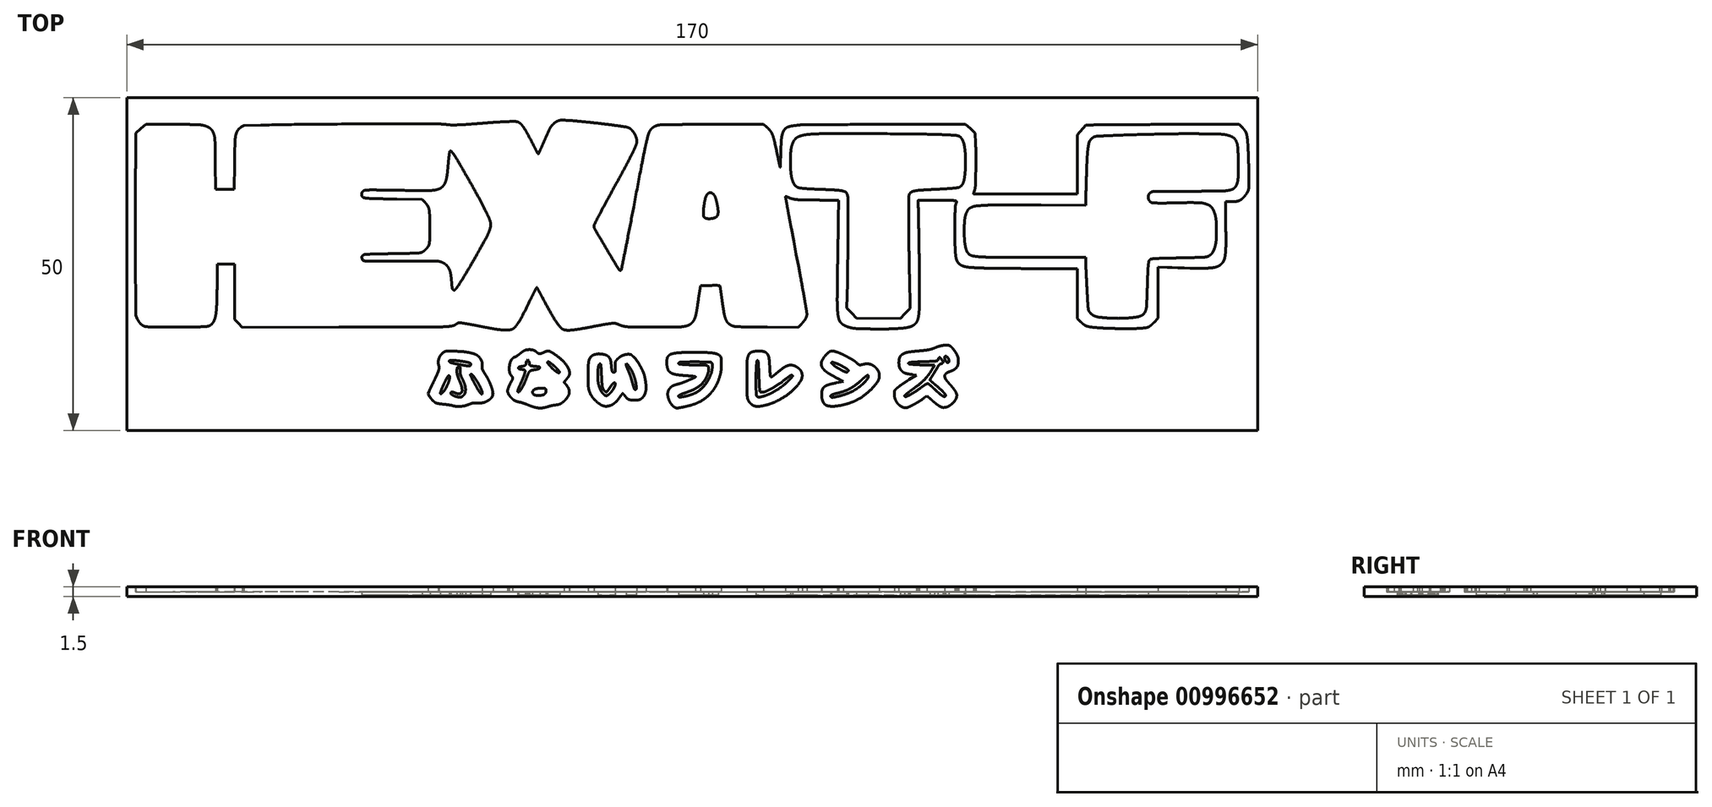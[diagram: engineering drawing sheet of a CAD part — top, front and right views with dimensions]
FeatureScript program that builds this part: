
annotation { "Feature Type Name" : "Feature", "Feature Type Description" : "" }
export const myFeature = defineFeature(function(context is Context, id is Id, definition is map)
    precondition{}
    {
        {
            var Q0;
            Q0=qCreatedBy(makeId("Top.planeOp"),FACE);
            var sketch = newSketch(context, id + "F0", { "sketchPlane" : qUnion([Q0])});
            skArc(sketch, "E0", {"start": v(-16.39, 21.41) * mm, "mid": v(-15.05, 21.27) * mm, "end": v(-13.72, 21.12) * mm});
            skArc(sketch, "E1", {"start": v(-13.72, 21.12) * mm, "mid": v(-12.67, 21) * mm, "end": v(-11.61, 20.86) * mm});
            skArc(sketch, "E2", {"start": v(-11.61, 20.86) * mm, "mid": v(-10.8, 20.74) * mm, "end": v(-9.97, 20.62) * mm});
            skArc(sketch, "E3", {"start": v(-9.97, 20.62) * mm, "mid": v(-9.73, 20.56) * mm, "end": v(-9.5, 20.47) * mm});
            skArc(sketch, "E4", {"start": v(-9.5, 20.47) * mm, "mid": v(-9.28, 20.34) * mm, "end": v(-9.1, 20.17) * mm});
            skArc(sketch, "E5", {"start": v(-9.1, 20.17) * mm, "mid": v(-8.9, 19.95) * mm, "end": v(-8.73, 19.7) * mm});
            skArc(sketch, "E6", {"start": v(-8.73, 19.7) * mm, "mid": v(-8.58, 19.45) * mm, "end": v(-8.45, 19.17) * mm});
            skArc(sketch, "E7", {"start": v(-8.45, 19.17) * mm, "mid": v(-8.37, 18.9) * mm, "end": v(-8.33, 18.63) * mm});
            skArc(sketch, "E8", {"start": v(-8.33, 18.63) * mm, "mid": v(-8.32, 18.52) * mm, "end": v(-8.32, 18.42) * mm});
            skArc(sketch, "E9", {"start": v(-8.32, 18.42) * mm, "mid": v(-8.32, 18.33) * mm, "end": v(-8.33, 18.24) * mm});
            skArc(sketch, "E10", {"start": v(-8.33, 18.24) * mm, "mid": v(-8.36, 18.14) * mm, "end": v(-8.38, 18.04) * mm});
            skArc(sketch, "E11", {"start": v(-8.38, 18.04) * mm, "mid": v(-8.43, 17.9) * mm, "end": v(-8.48, 17.77) * mm});
            skArc(sketch, "E12", {"start": v(-8.48, 17.77) * mm, "mid": v(-8.64, 17.4) * mm, "end": v(-8.8, 17.04) * mm});
            skArc(sketch, "E13", {"start": v(-8.8, 17.04) * mm, "mid": v(-9.11, 16.42) * mm, "end": v(-9.43, 15.8) * mm});
            skArc(sketch, "E14", {"start": v(-9.43, 15.8) * mm, "mid": v(-9.8, 15.06) * mm, "end": v(-10.2, 14.33) * mm});
            skArc(sketch, "E15", {"start": v(-10.2, 14.33) * mm, "mid": v(-10.61, 13.55) * mm, "end": v(-11.04, 12.77) * mm});
            skArc(sketch, "E16", {"start": v(-11.04, 12.77) * mm, "mid": v(-11.9, 11.22) * mm, "end": v(-12.74, 9.67) * mm});
            skArc(sketch, "E17", {"start": v(-12.74, 9.67) * mm, "mid": v(-13.3, 8.62) * mm, "end": v(-13.86, 7.57) * mm});
            skArc(sketch, "E18", {"start": v(-13.86, 7.57) * mm, "mid": v(-14.27, 6.8) * mm, "end": v(-14.67, 6.02) * mm});
            skArc(sketch, "E19", {"start": v(-14.67, 6.02) * mm, "mid": v(-14.73, 5.88) * mm, "end": v(-14.74, 5.72) * mm});
            skArc(sketch, "E20", {"start": v(-14.74, 5.72) * mm, "mid": v(-14.7, 5.46) * mm, "end": v(-14.6, 5.22) * mm});
            skArc(sketch, "E21", {"start": v(-14.6, 5.22) * mm, "mid": v(-13.73, 3.73) * mm, "end": v(-12.84, 2.24) * mm});
            skArc(sketch, "E22", {"start": v(-12.84, 2.24) * mm, "mid": v(-11.93, 0.71) * mm, "end": v(-11.02, -0.8) * mm});
            skArc(sketch, "E23", {"start": v(-11.02, -0.8) * mm, "mid": v(-10.9, -0.91) * mm, "end": v(-10.76, -0.95) * mm});
            skArc(sketch, "E24", {"start": v(-10.76, -0.95) * mm, "mid": v(-10.7, -0.93) * mm, "end": v(-10.66, -0.87) * mm});
            skArc(sketch, "E25", {"start": v(-10.66, -0.87) * mm, "mid": v(-10.44, 0.14) * mm, "end": v(-10.24, 1.15) * mm});
            skArc(sketch, "E26", {"start": v(-10.24, 1.15) * mm, "mid": v(-9.95, 2.55) * mm, "end": v(-9.68, 3.94) * mm});
            skArc(sketch, "E27", {"start": v(-9.68, 3.94) * mm, "mid": v(-9.23, 6.26) * mm, "end": v(-8.8, 8.58) * mm});
            skArc(sketch, "E28", {"start": v(-8.8, 8.58) * mm, "mid": v(-8.22, 11.62) * mm, "end": v(-7.63, 14.66) * mm});
            skArc(sketch, "E29", {"start": v(-7.63, 14.66) * mm, "mid": v(-7.35, 16.1) * mm, "end": v(-7.05, 17.54) * mm});
            skArc(sketch, "E30", {"start": v(-7.05, 17.54) * mm, "mid": v(-6.87, 18.38) * mm, "end": v(-6.66, 19.23) * mm});
            skArc(sketch, "E31", {"start": v(-6.66, 19.23) * mm, "mid": v(-6.54, 19.62) * mm, "end": v(-6.37, 20) * mm});
            skArc(sketch, "E32", {"start": v(-6.37, 20) * mm, "mid": v(-6.26, 20.16) * mm, "end": v(-6.14, 20.31) * mm});
            skArc(sketch, "E33", {"start": v(-6.14, 20.31) * mm, "mid": v(-6, 20.45) * mm, "end": v(-5.85, 20.57) * mm});
            skArc(sketch, "E34", {"start": v(-5.85, 20.57) * mm, "mid": v(-5.67, 20.68) * mm, "end": v(-5.49, 20.77) * mm});
            skArc(sketch, "E35", {"start": v(-5.49, 20.77) * mm, "mid": v(-5.28, 20.84) * mm, "end": v(-5.07, 20.9) * mm});
            skArc(sketch, "E36", {"start": v(-5.07, 20.9) * mm, "mid": v(-4.86, 20.93) * mm, "end": v(-4.64, 20.94) * mm});
            skArc(sketch, "E37", {"start": v(-4.64, 20.94) * mm, "mid": v(-3.87, 20.96) * mm, "end": v(-3.1, 20.97) * mm});
            skArc(sketch, "E38", {"start": v(-3.1, 20.97) * mm, "mid": v(-1.96, 20.98) * mm, "end": v(-0.81, 21) * mm});
            skArc(sketch, "E39", {"start": v(-0.81, 21) * mm, "mid": v(1.12, 21) * mm, "end": v(3.05, 21.01) * mm});
            skLineSegment(sketch, "E40", {"start": v(3.05, 21.01) * mm, "end": v(10.73, 21.04) * mm});
            skLineSegment(sketch, "E41", {"start": v(10.73, 21.04) * mm, "end": v(11.19, 20.64) * mm});
            skArc(sketch, "E42", {"start": v(11.19, 20.64) * mm, "mid": v(11.47, 20.36) * mm, "end": v(11.73, 20.06) * mm});
            skArc(sketch, "E43", {"start": v(11.73, 20.06) * mm, "mid": v(11.92, 19.77) * mm, "end": v(12.07, 19.45) * mm});
            skArc(sketch, "E44", {"start": v(12.07, 19.45) * mm, "mid": v(12.23, 19) * mm, "end": v(12.36, 18.52) * mm});
            skArc(sketch, "E45", {"start": v(12.36, 18.52) * mm, "mid": v(12.58, 17.5) * mm, "end": v(12.8, 16.48) * mm});
            skArc(sketch, "E46", {"start": v(12.8, 16.48) * mm, "mid": v(12.89, 16.08) * mm, "end": v(12.97, 15.67) * mm});
            skArc(sketch, "E47", {"start": v(12.97, 15.67) * mm, "mid": v(13.04, 15.35) * mm, "end": v(13.12, 15.03) * mm});
            skArc(sketch, "E48", {"start": v(13.12, 15.03) * mm, "mid": v(13.17, 14.8) * mm, "end": v(13.23, 14.55) * mm});
            skArc(sketch, "E49", {"start": v(13.23, 14.55) * mm, "mid": v(13.24, 14.54) * mm, "end": v(13.25, 14.55) * mm});
            skArc(sketch, "E50", {"start": v(13.25, 14.55) * mm, "mid": v(13.26, 14.63) * mm, "end": v(13.26, 14.7) * mm});
            skArc(sketch, "E51", {"start": v(13.26, 14.7) * mm, "mid": v(13.27, 15) * mm, "end": v(13.28, 15.29) * mm});
            skArc(sketch, "E52", {"start": v(13.28, 15.29) * mm, "mid": v(13.29, 15.63) * mm, "end": v(13.3, 15.98) * mm});
            skArc(sketch, "E53", {"start": v(13.3, 15.98) * mm, "mid": v(13.31, 16.37) * mm, "end": v(13.32, 16.76) * mm});
            skArc(sketch, "E54", {"start": v(13.32, 16.76) * mm, "mid": v(13.35, 17.49) * mm, "end": v(13.38, 18.21) * mm});
            skArc(sketch, "E55", {"start": v(13.38, 18.21) * mm, "mid": v(13.4, 18.6) * mm, "end": v(13.45, 19) * mm});
            skArc(sketch, "E56", {"start": v(13.45, 19) * mm, "mid": v(13.5, 19.26) * mm, "end": v(13.55, 19.52) * mm});
            skArc(sketch, "E57", {"start": v(13.55, 19.52) * mm, "mid": v(13.63, 19.75) * mm, "end": v(13.73, 19.98) * mm});
            skArc(sketch, "E58", {"start": v(13.73, 19.98) * mm, "mid": v(13.85, 20.18) * mm, "end": v(14, 20.35) * mm});
            skArc(sketch, "E59", {"start": v(14, 20.35) * mm, "mid": v(14.17, 20.5) * mm, "end": v(14.36, 20.6) * mm});
            skArc(sketch, "E60", {"start": v(14.36, 20.6) * mm, "mid": v(14.64, 20.7) * mm, "end": v(14.94, 20.76) * mm});
            skArc(sketch, "E61", {"start": v(14.94, 20.76) * mm, "mid": v(15.46, 20.83) * mm, "end": v(15.99, 20.9) * mm});
            skArc(sketch, "E62", {"start": v(15.99, 20.9) * mm, "mid": v(16.28, 20.93) * mm, "end": v(16.58, 20.94) * mm});
            skArc(sketch, "E63", {"start": v(16.58, 20.94) * mm, "mid": v(18.06, 20.95) * mm, "end": v(19.55, 20.96) * mm});
            skArc(sketch, "E64", {"start": v(19.55, 20.96) * mm, "mid": v(21.5, 20.98) * mm, "end": v(23.44, 20.99) * mm});
            skArc(sketch, "E65", {"start": v(23.44, 20.99) * mm, "mid": v(26.15, 21) * mm, "end": v(28.87, 21) * mm});
            skLineSegment(sketch, "E66", {"start": v(28.87, 21) * mm, "end": v(41.08, 21.04) * mm});
            skLineSegment(sketch, "E67", {"start": v(41.08, 21.04) * mm, "end": v(41.82, 20.37) * mm});
            skLineSegment(sketch, "E68", {"start": v(41.82, 20.37) * mm, "end": v(42.57, 19.7) * mm});
            skLineSegment(sketch, "E69", {"start": v(42.57, 19.7) * mm, "end": v(42.62, 18.14) * mm});
            skArc(sketch, "E70", {"start": v(42.62, 18.14) * mm, "mid": v(42.63, 17.76) * mm, "end": v(42.64, 17.37) * mm});
            skArc(sketch, "E71", {"start": v(42.64, 17.37) * mm, "mid": v(42.64, 16.84) * mm, "end": v(42.65, 16.3) * mm});
            skArc(sketch, "E72", {"start": v(42.65, 16.3) * mm, "mid": v(42.65, 15.72) * mm, "end": v(42.65, 15.14) * mm});
            skArc(sketch, "E73", {"start": v(42.65, 15.14) * mm, "mid": v(42.64, 14.6) * mm, "end": v(42.64, 14.06) * mm});
            skArc(sketch, "E74", {"start": v(42.64, 14.06) * mm, "mid": v(42.63, 13.3) * mm, "end": v(42.62, 12.54) * mm});
            skArc(sketch, "E75", {"start": v(42.62, 12.54) * mm, "mid": v(42.6, 12.2) * mm, "end": v(42.59, 11.86) * mm});
            skArc(sketch, "E76", {"start": v(42.59, 11.86) * mm, "mid": v(42.57, 11.65) * mm, "end": v(42.54, 11.44) * mm});
            skArc(sketch, "E77", {"start": v(42.54, 11.44) * mm, "mid": v(42.5, 11.26) * mm, "end": v(42.46, 11.09) * mm});
            skArc(sketch, "E78", {"start": v(42.46, 11.09) * mm, "mid": v(42.43, 11) * mm, "end": v(42.4, 10.91) * mm});
            skArc(sketch, "E79", {"start": v(42.4, 10.91) * mm, "mid": v(42.37, 10.83) * mm, "end": v(42.35, 10.75) * mm});
            skArc(sketch, "E80", {"start": v(42.35, 10.75) * mm, "mid": v(42.33, 10.69) * mm, "end": v(42.31, 10.62) * mm});
            skArc(sketch, "E81", {"start": v(42.31, 10.62) * mm, "mid": v(42.3, 10.6) * mm, "end": v(42.3, 10.58) * mm});
            skArc(sketch, "E82", {"start": v(42.3, 10.58) * mm, "mid": v(42.31, 10.57) * mm, "end": v(42.33, 10.56) * mm});
            skArc(sketch, "E83", {"start": v(42.33, 10.56) * mm, "mid": v(43.46, 10.55) * mm, "end": v(44.6, 10.54) * mm});
            skArc(sketch, "E84", {"start": v(44.6, 10.54) * mm, "mid": v(45.86, 10.54) * mm, "end": v(47.12, 10.53) * mm});
            skArc(sketch, "E85", {"start": v(47.12, 10.53) * mm, "mid": v(48.61, 10.53) * mm, "end": v(50.11, 10.53) * mm});
            skLineSegment(sketch, "E86", {"start": v(50.11, 10.53) * mm, "end": v(57.92, 10.53) * mm});
            skLineSegment(sketch, "E87", {"start": v(57.92, 10.53) * mm, "end": v(57.92, 14.98) * mm});
            skLineSegment(sketch, "E88", {"start": v(57.92, 14.98) * mm, "end": v(57.92, 19.43) * mm});
            skLineSegment(sketch, "E89", {"start": v(57.92, 19.43) * mm, "end": v(58.56, 20.15) * mm});
            skLineSegment(sketch, "E90", {"start": v(58.56, 20.15) * mm, "end": v(59.2, 20.88) * mm});
            skLineSegment(sketch, "E91", {"start": v(59.2, 20.88) * mm, "end": v(60.08, 20.92) * mm});
            skArc(sketch, "E92", {"start": v(60.08, 20.92) * mm, "mid": v(60.4, 20.93) * mm, "end": v(60.73, 20.93) * mm});
            skArc(sketch, "E93", {"start": v(60.73, 20.93) * mm, "mid": v(62.28, 20.95) * mm, "end": v(63.83, 20.96) * mm});
            skArc(sketch, "E94", {"start": v(63.83, 20.96) * mm, "mid": v(65.65, 20.97) * mm, "end": v(67.46, 20.98) * mm});
            skArc(sketch, "E95", {"start": v(67.46, 20.98) * mm, "mid": v(69.53, 21) * mm, "end": v(71.6, 21) * mm});
            skLineSegment(sketch, "E96", {"start": v(71.6, 21) * mm, "end": v(82.25, 21.05) * mm});
            skLineSegment(sketch, "E97", {"start": v(82.25, 21.05) * mm, "end": v(82.7, 20.57) * mm});
            skArc(sketch, "E98", {"start": v(82.7, 20.57) * mm, "mid": v(82.87, 20.36) * mm, "end": v(83.04, 20.15) * mm});
            skArc(sketch, "E99", {"start": v(83.04, 20.15) * mm, "mid": v(83.15, 19.98) * mm, "end": v(83.25, 19.8) * mm});
            skArc(sketch, "E100", {"start": v(83.25, 19.8) * mm, "mid": v(83.32, 19.62) * mm, "end": v(83.37, 19.42) * mm});
            skArc(sketch, "E101", {"start": v(83.37, 19.42) * mm, "mid": v(83.42, 19.16) * mm, "end": v(83.46, 18.9) * mm});
            skArc(sketch, "E102", {"start": v(83.46, 18.9) * mm, "mid": v(83.5, 18.42) * mm, "end": v(83.54, 17.94) * mm});
            skArc(sketch, "E103", {"start": v(83.54, 17.94) * mm, "mid": v(83.58, 17.18) * mm, "end": v(83.61, 16.43) * mm});
            skArc(sketch, "E104", {"start": v(83.61, 16.43) * mm, "mid": v(83.64, 15.59) * mm, "end": v(83.67, 14.75) * mm});
            skArc(sketch, "E105", {"start": v(83.67, 14.75) * mm, "mid": v(83.68, 13.95) * mm, "end": v(83.69, 13.14) * mm});
            skArc(sketch, "E106", {"start": v(83.69, 13.14) * mm, "mid": v(83.69, 12.54) * mm, "end": v(83.69, 11.93) * mm});
            skArc(sketch, "E107", {"start": v(83.69, 11.93) * mm, "mid": v(83.68, 11.7) * mm, "end": v(83.67, 11.46) * mm});
            skArc(sketch, "E108", {"start": v(83.67, 11.46) * mm, "mid": v(83.65, 11.32) * mm, "end": v(83.63, 11.18) * mm});
            skArc(sketch, "E109", {"start": v(83.63, 11.18) * mm, "mid": v(83.59, 11.05) * mm, "end": v(83.53, 10.93) * mm});
            skArc(sketch, "E110", {"start": v(83.53, 10.93) * mm, "mid": v(83.42, 10.72) * mm, "end": v(83.3, 10.52) * mm});
            skArc(sketch, "E111", {"start": v(83.3, 10.52) * mm, "mid": v(83.14, 10.32) * mm, "end": v(82.98, 10.13) * mm});
            skArc(sketch, "E112", {"start": v(82.98, 10.13) * mm, "mid": v(82.82, 9.96) * mm, "end": v(82.65, 9.8) * mm});
            skArc(sketch, "E113", {"start": v(82.65, 9.8) * mm, "mid": v(82.5, 9.69) * mm, "end": v(82.33, 9.6) * mm});
            skArc(sketch, "E114", {"start": v(82.33, 9.6) * mm, "mid": v(82.22, 9.54) * mm, "end": v(82.1, 9.49) * mm});
            skArc(sketch, "E115", {"start": v(82.1, 9.49) * mm, "mid": v(82, 9.46) * mm, "end": v(81.89, 9.44) * mm});
            skArc(sketch, "E116", {"start": v(81.89, 9.44) * mm, "mid": v(81.75, 9.42) * mm, "end": v(81.6, 9.41) * mm});
            skArc(sketch, "E117", {"start": v(81.6, 9.41) * mm, "mid": v(81.34, 9.41) * mm, "end": v(81.07, 9.4) * mm});
            skLineSegment(sketch, "E118", {"start": v(81.07, 9.4) * mm, "end": v(80.17, 9.4) * mm});
            skLineSegment(sketch, "E119", {"start": v(80.17, 9.4) * mm, "end": v(80.22, 5.86) * mm});
            skArc(sketch, "E120", {"start": v(80.22, 5.86) * mm, "mid": v(80.23, 4.63) * mm, "end": v(80.24, 3.4) * mm});
            skArc(sketch, "E121", {"start": v(80.24, 3.4) * mm, "mid": v(80.23, 2.75) * mm, "end": v(80.2, 2.1) * mm});
            skArc(sketch, "E122", {"start": v(80.2, 2.1) * mm, "mid": v(80.18, 1.68) * mm, "end": v(80.12, 1.26) * mm});
            skArc(sketch, "E123", {"start": v(80.12, 1.26) * mm, "mid": v(80.06, 0.94) * mm, "end": v(79.96, 0.62) * mm});
            skArc(sketch, "E124", {"start": v(79.96, 0.62) * mm, "mid": v(79.88, 0.45) * mm, "end": v(79.78, 0.29) * mm});
            skArc(sketch, "E125", {"start": v(79.78, 0.29) * mm, "mid": v(79.66, 0.13) * mm, "end": v(79.52, -0.02) * mm});
            skArc(sketch, "E126", {"start": v(79.52, -0.02) * mm, "mid": v(79.36, -0.14) * mm, "end": v(79.2, -0.26) * mm});
            skArc(sketch, "E127", {"start": v(79.2, -0.26) * mm, "mid": v(79.01, -0.35) * mm, "end": v(78.82, -0.42) * mm});
            skArc(sketch, "E128", {"start": v(78.82, -0.42) * mm, "mid": v(78.53, -0.5) * mm, "end": v(78.24, -0.54) * mm});
            skArc(sketch, "E129", {"start": v(78.24, -0.54) * mm, "mid": v(77.82, -0.59) * mm, "end": v(77.4, -0.61) * mm});
            skArc(sketch, "E130", {"start": v(77.4, -0.61) * mm, "mid": v(76.86, -0.63) * mm, "end": v(76.3, -0.63) * mm});
            skArc(sketch, "E131", {"start": v(76.3, -0.63) * mm, "mid": v(75.58, -0.62) * mm, "end": v(74.86, -0.6) * mm});
            skArc(sketch, "E132", {"start": v(74.86, -0.6) * mm, "mid": v(74.42, -0.59) * mm, "end": v(73.99, -0.57) * mm});
            skArc(sketch, "E133", {"start": v(73.99, -0.57) * mm, "mid": v(73.5, -0.56) * mm, "end": v(73.03, -0.54) * mm});
            skArc(sketch, "E134", {"start": v(73.03, -0.54) * mm, "mid": v(72.58, -0.53) * mm, "end": v(72.13, -0.51) * mm});
            skArc(sketch, "E135", {"start": v(72.13, -0.51) * mm, "mid": v(71.78, -0.5) * mm, "end": v(71.44, -0.49) * mm});
            skLineSegment(sketch, "E136", {"start": v(71.44, -0.49) * mm, "end": v(70.03, -0.44) * mm});
            skLineSegment(sketch, "E137", {"start": v(70.03, -0.44) * mm, "end": v(70.03, -4.29) * mm});
            skLineSegment(sketch, "E138", {"start": v(70.03, -4.29) * mm, "end": v(70.03, -8.13) * mm});
            skLineSegment(sketch, "E139", {"start": v(70.03, -8.13) * mm, "end": v(69.45, -8.74) * mm});
            skArc(sketch, "E140", {"start": v(69.45, -8.74) * mm, "mid": v(69.33, -8.86) * mm, "end": v(69.2, -8.98) * mm});
            skArc(sketch, "E141", {"start": v(69.2, -8.98) * mm, "mid": v(69.09, -9.1) * mm, "end": v(68.96, -9.2) * mm});
            skArc(sketch, "E142", {"start": v(68.96, -9.2) * mm, "mid": v(68.86, -9.29) * mm, "end": v(68.75, -9.37) * mm});
            skArc(sketch, "E143", {"start": v(68.75, -9.37) * mm, "mid": v(68.69, -9.42) * mm, "end": v(68.62, -9.45) * mm});
            skArc(sketch, "E144", {"start": v(68.62, -9.45) * mm, "mid": v(68.4, -9.52) * mm, "end": v(68.19, -9.57) * mm});
            skArc(sketch, "E145", {"start": v(68.19, -9.57) * mm, "mid": v(67.85, -9.61) * mm, "end": v(67.52, -9.64) * mm});
            skArc(sketch, "E146", {"start": v(67.52, -9.64) * mm, "mid": v(67.05, -9.67) * mm, "end": v(66.58, -9.69) * mm});
            skArc(sketch, "E147", {"start": v(66.58, -9.69) * mm, "mid": v(65.92, -9.7) * mm, "end": v(65.26, -9.7) * mm});
            skArc(sketch, "E148", {"start": v(65.26, -9.7) * mm, "mid": v(64.18, -9.7) * mm, "end": v(63.1, -9.67) * mm});
            skArc(sketch, "E149", {"start": v(63.1, -9.67) * mm, "mid": v(62.18, -9.64) * mm, "end": v(61.28, -9.58) * mm});
            skArc(sketch, "E150", {"start": v(61.28, -9.58) * mm, "mid": v(60.56, -9.53) * mm, "end": v(59.86, -9.45) * mm});
            skArc(sketch, "E151", {"start": v(59.86, -9.45) * mm, "mid": v(59.5, -9.39) * mm, "end": v(59.18, -9.27) * mm});
            skArc(sketch, "E152", {"start": v(59.18, -9.27) * mm, "mid": v(59.1, -9.23) * mm, "end": v(59.02, -9.19) * mm});
            skArc(sketch, "E153", {"start": v(59.02, -9.19) * mm, "mid": v(58.92, -9.11) * mm, "end": v(58.81, -9.04) * mm});
            skArc(sketch, "E154", {"start": v(58.81, -9.04) * mm, "mid": v(58.7, -8.95) * mm, "end": v(58.6, -8.86) * mm});
            skArc(sketch, "E155", {"start": v(58.6, -8.86) * mm, "mid": v(58.49, -8.76) * mm, "end": v(58.39, -8.67) * mm});
            skLineSegment(sketch, "E156", {"start": v(58.39, -8.67) * mm, "end": v(57.92, -8.2) * mm});
            skLineSegment(sketch, "E157", {"start": v(57.92, -8.2) * mm, "end": v(57.92, -4.44) * mm});
            skLineSegment(sketch, "E158", {"start": v(57.92, -4.44) * mm, "end": v(57.92, -0.67) * mm});
            skLineSegment(sketch, "E159", {"start": v(57.92, -0.67) * mm, "end": v(51.95, -0.67) * mm});
            skArc(sketch, "E160", {"start": v(51.95, -0.67) * mm, "mid": v(50.73, -0.67) * mm, "end": v(49.51, -0.66) * mm});
            skArc(sketch, "E161", {"start": v(49.51, -0.66) * mm, "mid": v(48.32, -0.66) * mm, "end": v(47.13, -0.65) * mm});
            skArc(sketch, "E162", {"start": v(47.13, -0.65) * mm, "mid": v(46.1, -0.64) * mm, "end": v(45.07, -0.63) * mm});
            skArc(sketch, "E163", {"start": v(45.07, -0.63) * mm, "mid": v(44.5, -0.62) * mm, "end": v(43.92, -0.6) * mm});
            skArc(sketch, "E164", {"start": v(43.92, -0.6) * mm, "mid": v(42.95, -0.57) * mm, "end": v(42, -0.51) * mm});
            skArc(sketch, "E165", {"start": v(42, -0.51) * mm, "mid": v(41.47, -0.46) * mm, "end": v(40.96, -0.37) * mm});
            skArc(sketch, "E166", {"start": v(40.96, -0.37) * mm, "mid": v(40.64, -0.26) * mm, "end": v(40.33, -0.11) * mm});
            skArc(sketch, "E167", {"start": v(40.33, -0.11) * mm, "mid": v(40.1, 0.07) * mm, "end": v(39.91, 0.3) * mm});
            skArc(sketch, "E168", {"start": v(39.91, 0.3) * mm, "mid": v(39.81, 0.5) * mm, "end": v(39.74, 0.7) * mm});
            skArc(sketch, "E169", {"start": v(39.74, 0.7) * mm, "mid": v(39.68, 0.92) * mm, "end": v(39.63, 1.16) * mm});
            skArc(sketch, "E170", {"start": v(39.63, 1.16) * mm, "mid": v(39.59, 1.52) * mm, "end": v(39.56, 1.89) * mm});
            skArc(sketch, "E171", {"start": v(39.56, 1.89) * mm, "mid": v(39.53, 2.57) * mm, "end": v(39.5, 3.25) * mm});
            skArc(sketch, "E172", {"start": v(39.5, 3.25) * mm, "mid": v(39.47, 4.22) * mm, "end": v(39.46, 5.19) * mm});
            skArc(sketch, "E173", {"start": v(39.46, 5.19) * mm, "mid": v(39.47, 6.13) * mm, "end": v(39.5, 7.07) * mm});
            skArc(sketch, "E174", {"start": v(39.5, 7.07) * mm, "mid": v(39.53, 7.89) * mm, "end": v(39.58, 8.7) * mm});
            skArc(sketch, "E175", {"start": v(39.58, 8.7) * mm, "mid": v(39.62, 8.97) * mm, "end": v(39.72, 9.21) * mm});
            skArc(sketch, "E176", {"start": v(39.72, 9.21) * mm, "mid": v(39.74, 9.25) * mm, "end": v(39.75, 9.29) * mm});
            skArc(sketch, "E177", {"start": v(39.75, 9.29) * mm, "mid": v(39.76, 9.32) * mm, "end": v(39.76, 9.35) * mm});
            skArc(sketch, "E178", {"start": v(39.76, 9.35) * mm, "mid": v(39.75, 9.38) * mm, "end": v(39.74, 9.4) * mm});
            skArc(sketch, "E179", {"start": v(39.74, 9.4) * mm, "mid": v(39.71, 9.44) * mm, "end": v(39.68, 9.47) * mm});
            skArc(sketch, "E180", {"start": v(39.68, 9.47) * mm, "mid": v(39.62, 9.52) * mm, "end": v(39.54, 9.54) * mm});
            skArc(sketch, "E181", {"start": v(39.54, 9.54) * mm, "mid": v(39.33, 9.56) * mm, "end": v(39.11, 9.57) * mm});
            skArc(sketch, "E182", {"start": v(39.11, 9.57) * mm, "mid": v(38.74, 9.58) * mm, "end": v(38.37, 9.6) * mm});
            skArc(sketch, "E183", {"start": v(38.37, 9.6) * mm, "mid": v(37.55, 9.6) * mm, "end": v(36.73, 9.6) * mm});
            skArc(sketch, "E184", {"start": v(36.73, 9.6) * mm, "mid": v(35.83, 9.61) * mm, "end": v(34.93, 9.62) * mm});
            skArc(sketch, "E185", {"start": v(34.93, 9.62) * mm, "mid": v(34.61, 9.62) * mm, "end": v(34.3, 9.6) * mm});
            skArc(sketch, "E186", {"start": v(34.3, 9.6) * mm, "mid": v(34.14, 9.6) * mm, "end": v(33.98, 9.58) * mm});
            skArc(sketch, "E187", {"start": v(33.98, 9.58) * mm, "mid": v(33.94, 9.55) * mm, "end": v(33.93, 9.5) * mm});
            skArc(sketch, "E188", {"start": v(33.93, 9.5) * mm, "mid": v(33.97, 9.35) * mm, "end": v(33.98, 9.2) * mm});
            skArc(sketch, "E189", {"start": v(33.98, 9.2) * mm, "mid": v(34.02, 7.57) * mm, "end": v(34.05, 5.93) * mm});
            skArc(sketch, "E190", {"start": v(34.05, 5.93) * mm, "mid": v(34.09, 4.16) * mm, "end": v(34.12, 2.39) * mm});
            skArc(sketch, "E191", {"start": v(34.12, 2.39) * mm, "mid": v(34.14, 0.5) * mm, "end": v(34.16, -1.4) * mm});
            skArc(sketch, "E192", {"start": v(34.16, -1.4) * mm, "mid": v(34.17, -3.38) * mm, "end": v(34.18, -5.36) * mm});
            skArc(sketch, "E193", {"start": v(34.18, -5.36) * mm, "mid": v(34.16, -6.27) * mm, "end": v(34.11, -7.2) * mm});
            skArc(sketch, "E194", {"start": v(34.11, -7.2) * mm, "mid": v(34.05, -7.73) * mm, "end": v(33.95, -8.25) * mm});
            skArc(sketch, "E195", {"start": v(33.95, -8.25) * mm, "mid": v(33.82, -8.6) * mm, "end": v(33.61, -8.9) * mm});
            skArc(sketch, "E196", {"start": v(33.61, -8.9) * mm, "mid": v(33.42, -9.09) * mm, "end": v(33.2, -9.24) * mm});
            skArc(sketch, "E197", {"start": v(33.2, -9.24) * mm, "mid": v(32.92, -9.37) * mm, "end": v(32.64, -9.47) * mm});
            skArc(sketch, "E198", {"start": v(32.64, -9.47) * mm, "mid": v(32.24, -9.55) * mm, "end": v(31.83, -9.6) * mm});
            skArc(sketch, "E199", {"start": v(31.83, -9.6) * mm, "mid": v(31.17, -9.67) * mm, "end": v(30.51, -9.7) * mm});
            skArc(sketch, "E200", {"start": v(30.51, -9.7) * mm, "mid": v(29.72, -9.74) * mm, "end": v(28.93, -9.76) * mm});
            skArc(sketch, "E201", {"start": v(28.93, -9.76) * mm, "mid": v(27.9, -9.76) * mm, "end": v(26.87, -9.75) * mm});
            skArc(sketch, "E202", {"start": v(26.87, -9.75) * mm, "mid": v(25.89, -9.73) * mm, "end": v(24.9, -9.7) * mm});
            skArc(sketch, "E203", {"start": v(24.9, -9.7) * mm, "mid": v(24.46, -9.67) * mm, "end": v(24.03, -9.6) * mm});
            skArc(sketch, "E204", {"start": v(24.03, -9.6) * mm, "mid": v(23.78, -9.55) * mm, "end": v(23.53, -9.48) * mm});
            skArc(sketch, "E205", {"start": v(23.53, -9.48) * mm, "mid": v(23.29, -9.4) * mm, "end": v(23.05, -9.29) * mm});
            skArc(sketch, "E206", {"start": v(23.05, -9.29) * mm, "mid": v(22.84, -9.18) * mm, "end": v(22.64, -9.06) * mm});
            skArc(sketch, "E207", {"start": v(22.64, -9.06) * mm, "mid": v(22.5, -8.95) * mm, "end": v(22.37, -8.83) * mm});
            skArc(sketch, "E208", {"start": v(22.37, -8.83) * mm, "mid": v(22.15, -8.51) * mm, "end": v(22.03, -8.15) * mm});
            skArc(sketch, "E209", {"start": v(22.03, -8.15) * mm, "mid": v(21.92, -7.58) * mm, "end": v(21.86, -7) * mm});
            skArc(sketch, "E210", {"start": v(21.86, -7) * mm, "mid": v(21.82, -6.02) * mm, "end": v(21.8, -5.03) * mm});
            skArc(sketch, "E211", {"start": v(21.8, -5.03) * mm, "mid": v(21.83, -3) * mm, "end": v(21.85, -0.95) * mm});
            skArc(sketch, "E212", {"start": v(21.85, -0.95) * mm, "mid": v(21.87, 0.08) * mm, "end": v(21.89, 1.12) * mm});
            skArc(sketch, "E213", {"start": v(21.89, 1.12) * mm, "mid": v(21.9, 2.22) * mm, "end": v(21.93, 3.32) * mm});
            skArc(sketch, "E214", {"start": v(21.93, 3.32) * mm, "mid": v(21.94, 4.33) * mm, "end": v(21.96, 5.34) * mm});
            skArc(sketch, "E215", {"start": v(21.96, 5.34) * mm, "mid": v(21.97, 6.05) * mm, "end": v(21.98, 6.77) * mm});
            skLineSegment(sketch, "E216", {"start": v(21.98, 6.77) * mm, "end": v(22.03, 9.62) * mm});
            skLineSegment(sketch, "E217", {"start": v(22.03, 9.62) * mm, "end": v(19.23, 9.62) * mm});
            skArc(sketch, "E218", {"start": v(19.23, 9.62) * mm, "mid": v(18.14, 9.62) * mm, "end": v(17.04, 9.63) * mm});
            skArc(sketch, "E219", {"start": v(17.04, 9.63) * mm, "mid": v(16.47, 9.65) * mm, "end": v(15.9, 9.69) * mm});
            skArc(sketch, "E220", {"start": v(15.9, 9.69) * mm, "mid": v(15.52, 9.73) * mm, "end": v(15.15, 9.79) * mm});
            skArc(sketch, "E221", {"start": v(15.15, 9.79) * mm, "mid": v(14.86, 9.87) * mm, "end": v(14.57, 9.98) * mm});
            skArc(sketch, "E222", {"start": v(14.57, 9.98) * mm, "mid": v(14.48, 10.02) * mm, "end": v(14.39, 10.06) * mm});
            skArc(sketch, "E223", {"start": v(14.39, 10.06) * mm, "mid": v(14.3, 10.1) * mm, "end": v(14.22, 10.12) * mm});
            skArc(sketch, "E224", {"start": v(14.22, 10.12) * mm, "mid": v(14.15, 10.14) * mm, "end": v(14.08, 10.16) * mm});
            skArc(sketch, "E225", {"start": v(14.08, 10.16) * mm, "mid": v(14.07, 10.17) * mm, "end": v(14.05, 10.16) * mm});
            skArc(sketch, "E226", {"start": v(14.05, 10.16) * mm, "mid": v(14.04, 10.14) * mm, "end": v(14.03, 10.11) * mm});
            skArc(sketch, "E227", {"start": v(14.03, 10.11) * mm, "mid": v(14.16, 9.43) * mm, "end": v(14.28, 8.74) * mm});
            skArc(sketch, "E228", {"start": v(14.28, 8.74) * mm, "mid": v(14.42, 7.98) * mm, "end": v(14.56, 7.21) * mm});
            skArc(sketch, "E229", {"start": v(14.56, 7.21) * mm, "mid": v(14.73, 6.3) * mm, "end": v(14.9, 5.4) * mm});
            skArc(sketch, "E230", {"start": v(14.9, 5.4) * mm, "mid": v(15.08, 4.43) * mm, "end": v(15.27, 3.45) * mm});
            skArc(sketch, "E231", {"start": v(15.27, 3.45) * mm, "mid": v(15.45, 2.47) * mm, "end": v(15.64, 1.5) * mm});
            skArc(sketch, "E232", {"start": v(15.64, 1.5) * mm, "mid": v(15.8, 0.63) * mm, "end": v(15.97, -0.23) * mm});
            skArc(sketch, "E233", {"start": v(15.97, -0.23) * mm, "mid": v(16.07, -0.77) * mm, "end": v(16.17, -1.3) * mm});
            skArc(sketch, "E234", {"start": v(16.17, -1.3) * mm, "mid": v(16.37, -2.39) * mm, "end": v(16.57, -3.47) * mm});
            skArc(sketch, "E235", {"start": v(16.57, -3.47) * mm, "mid": v(16.75, -4.46) * mm, "end": v(16.92, -5.44) * mm});
            skArc(sketch, "E236", {"start": v(16.92, -5.44) * mm, "mid": v(17.07, -6.3) * mm, "end": v(17.21, -7.15) * mm});
            skArc(sketch, "E237", {"start": v(17.21, -7.15) * mm, "mid": v(17.24, -7.35) * mm, "end": v(17.25, -7.56) * mm});
            skArc(sketch, "E238", {"start": v(17.25, -7.56) * mm, "mid": v(17.23, -7.72) * mm, "end": v(17.2, -7.87) * mm});
            skArc(sketch, "E239", {"start": v(17.2, -7.87) * mm, "mid": v(17.14, -8.04) * mm, "end": v(17.06, -8.2) * mm});
            skArc(sketch, "E240", {"start": v(17.06, -8.2) * mm, "mid": v(16.94, -8.4) * mm, "end": v(16.81, -8.57) * mm});
            skArc(sketch, "E241", {"start": v(16.81, -8.57) * mm, "mid": v(16.63, -8.78) * mm, "end": v(16.45, -8.98) * mm});
            skLineSegment(sketch, "E242", {"start": v(16.45, -8.98) * mm, "end": v(15.96, -9.5) * mm});
            skLineSegment(sketch, "E243", {"start": v(15.96, -9.5) * mm, "end": v(11.3, -9.47) * mm});
            skArc(sketch, "E244", {"start": v(11.3, -9.47) * mm, "mid": v(10.04, -9.46) * mm, "end": v(8.77, -9.45) * mm});
            skArc(sketch, "E245", {"start": v(8.77, -9.45) * mm, "mid": v(8.1, -9.44) * mm, "end": v(7.44, -9.43) * mm});
            skArc(sketch, "E246", {"start": v(7.44, -9.43) * mm, "mid": v(7.03, -9.42) * mm, "end": v(6.62, -9.4) * mm});
            skArc(sketch, "E247", {"start": v(6.62, -9.4) * mm, "mid": v(6.43, -9.38) * mm, "end": v(6.25, -9.34) * mm});
            skArc(sketch, "E248", {"start": v(6.25, -9.34) * mm, "mid": v(5.88, -9.2) * mm, "end": v(5.55, -9) * mm});
            skArc(sketch, "E249", {"start": v(5.55, -9) * mm, "mid": v(5.3, -8.74) * mm, "end": v(5.11, -8.44) * mm});
            skArc(sketch, "E250", {"start": v(5.11, -8.44) * mm, "mid": v(4.93, -7.94) * mm, "end": v(4.8, -7.42) * mm});
            skArc(sketch, "E251", {"start": v(4.8, -7.42) * mm, "mid": v(4.63, -6.34) * mm, "end": v(4.47, -5.26) * mm});
            skArc(sketch, "E252", {"start": v(4.47, -5.26) * mm, "mid": v(4.42, -4.9) * mm, "end": v(4.37, -4.55) * mm});
            skArc(sketch, "E253", {"start": v(4.37, -4.55) * mm, "mid": v(4.33, -4.24) * mm, "end": v(4.28, -3.93) * mm});
            skArc(sketch, "E254", {"start": v(4.28, -3.93) * mm, "mid": v(4.24, -3.67) * mm, "end": v(4.2, -3.4) * mm});
            skArc(sketch, "E255", {"start": v(4.2, -3.4) * mm, "mid": v(4.2, -3.36) * mm, "end": v(4.18, -3.31) * mm});
            skArc(sketch, "E256", {"start": v(4.18, -3.31) * mm, "mid": v(4.16, -3.27) * mm, "end": v(4.11, -3.24) * mm});
            skArc(sketch, "E257", {"start": v(4.11, -3.24) * mm, "mid": v(4.02, -3.22) * mm, "end": v(3.93, -3.21) * mm});
            skArc(sketch, "E258", {"start": v(3.93, -3.21) * mm, "mid": v(3.75, -3.2) * mm, "end": v(3.57, -3.2) * mm});
            skArc(sketch, "E259", {"start": v(3.57, -3.2) * mm, "mid": v(3.13, -3.2) * mm, "end": v(2.7, -3.2) * mm});
            skLineSegment(sketch, "E260", {"start": v(2.7, -3.2) * mm, "end": v(1.25, -3.23) * mm});
            skLineSegment(sketch, "E261", {"start": v(1.25, -3.23) * mm, "end": v(0.96, -5.19) * mm});
            skArc(sketch, "E262", {"start": v(0.96, -5.19) * mm, "mid": v(0.85, -5.94) * mm, "end": v(0.74, -6.7) * mm});
            skArc(sketch, "E263", {"start": v(0.74, -6.7) * mm, "mid": v(0.68, -7.06) * mm, "end": v(0.6, -7.42) * mm});
            skArc(sketch, "E264", {"start": v(0.6, -7.42) * mm, "mid": v(0.56, -7.66) * mm, "end": v(0.5, -7.88) * mm});
            skArc(sketch, "E265", {"start": v(0.5, -7.88) * mm, "mid": v(0.43, -8.08) * mm, "end": v(0.35, -8.27) * mm});
            skArc(sketch, "E266", {"start": v(0.35, -8.27) * mm, "mid": v(0.22, -8.51) * mm, "end": v(0.06, -8.74) * mm});
            skArc(sketch, "E267", {"start": v(0.06, -8.74) * mm, "mid": v(-0.11, -8.91) * mm, "end": v(-0.31, -9.06) * mm});
            skArc(sketch, "E268", {"start": v(-0.31, -9.06) * mm, "mid": v(-0.56, -9.19) * mm, "end": v(-0.82, -9.28) * mm});
            skArc(sketch, "E269", {"start": v(-0.82, -9.28) * mm, "mid": v(-1.16, -9.36) * mm, "end": v(-1.51, -9.42) * mm});
            skArc(sketch, "E270", {"start": v(-1.51, -9.42) * mm, "mid": v(-1.95, -9.46) * mm, "end": v(-2.4, -9.48) * mm});
            skArc(sketch, "E271", {"start": v(-2.4, -9.48) * mm, "mid": v(-3.99, -9.48) * mm, "end": v(-5.58, -9.49) * mm});
            skArc(sketch, "E272", {"start": v(-5.58, -9.49) * mm, "mid": v(-7.15, -9.48) * mm, "end": v(-8.73, -9.48) * mm});
            skArc(sketch, "E273", {"start": v(-8.73, -9.48) * mm, "mid": v(-9.25, -9.46) * mm, "end": v(-9.76, -9.42) * mm});
            skArc(sketch, "E274", {"start": v(-9.76, -9.42) * mm, "mid": v(-9.92, -9.4) * mm, "end": v(-10.08, -9.38) * mm});
            skArc(sketch, "E275", {"start": v(-10.08, -9.38) * mm, "mid": v(-10.23, -9.35) * mm, "end": v(-10.37, -9.32) * mm});
            skArc(sketch, "E276", {"start": v(-10.37, -9.32) * mm, "mid": v(-10.5, -9.28) * mm, "end": v(-10.64, -9.24) * mm});
            skArc(sketch, "E277", {"start": v(-10.64, -9.24) * mm, "mid": v(-10.76, -9.2) * mm, "end": v(-10.88, -9.15) * mm});
            skArc(sketch, "E278", {"start": v(-10.88, -9.15) * mm, "mid": v(-10.98, -9.1) * mm, "end": v(-11.08, -9.07) * mm});
            skArc(sketch, "E279", {"start": v(-11.08, -9.07) * mm, "mid": v(-11.18, -9.03) * mm, "end": v(-11.27, -9) * mm});
            skArc(sketch, "E280", {"start": v(-11.27, -9) * mm, "mid": v(-11.36, -8.96) * mm, "end": v(-11.45, -8.93) * mm});
            skArc(sketch, "E281", {"start": v(-11.45, -8.93) * mm, "mid": v(-11.5, -8.91) * mm, "end": v(-11.56, -8.9) * mm});
            skArc(sketch, "E282", {"start": v(-11.56, -8.9) * mm, "mid": v(-11.72, -8.88) * mm, "end": v(-11.88, -8.89) * mm});
            skArc(sketch, "E283", {"start": v(-11.88, -8.89) * mm, "mid": v(-12.24, -8.93) * mm, "end": v(-12.6, -8.98) * mm});
            skArc(sketch, "E284", {"start": v(-12.6, -8.98) * mm, "mid": v(-13.1, -9.06) * mm, "end": v(-13.6, -9.14) * mm});
            skArc(sketch, "E285", {"start": v(-13.6, -9.14) * mm, "mid": v(-14.31, -9.27) * mm, "end": v(-15.02, -9.41) * mm});
            skArc(sketch, "E286", {"start": v(-15.02, -9.41) * mm, "mid": v(-15.9, -9.58) * mm, "end": v(-16.78, -9.74) * mm});
            skArc(sketch, "E287", {"start": v(-16.78, -9.74) * mm, "mid": v(-17.32, -9.83) * mm, "end": v(-17.86, -9.9) * mm});
            skArc(sketch, "E288", {"start": v(-17.86, -9.9) * mm, "mid": v(-18.23, -9.93) * mm, "end": v(-18.6, -9.95) * mm});
            skArc(sketch, "E289", {"start": v(-18.6, -9.95) * mm, "mid": v(-18.9, -9.93) * mm, "end": v(-19.18, -9.89) * mm});
            skArc(sketch, "E290", {"start": v(-19.18, -9.89) * mm, "mid": v(-19.47, -9.78) * mm, "end": v(-19.72, -9.58) * mm});
            skArc(sketch, "E291", {"start": v(-19.72, -9.58) * mm, "mid": v(-20.05, -9.2) * mm, "end": v(-20.36, -8.79) * mm});
            skArc(sketch, "E292", {"start": v(-20.36, -8.79) * mm, "mid": v(-20.8, -8.12) * mm, "end": v(-21.2, -7.42) * mm});
            skArc(sketch, "E293", {"start": v(-21.2, -7.42) * mm, "mid": v(-21.86, -6.23) * mm, "end": v(-22.5, -5.03) * mm});
            skArc(sketch, "E294", {"start": v(-22.5, -5.03) * mm, "mid": v(-22.66, -4.74) * mm, "end": v(-22.82, -4.46) * mm});
            skArc(sketch, "E295", {"start": v(-22.82, -4.46) * mm, "mid": v(-22.95, -4.21) * mm, "end": v(-23.08, -3.97) * mm});
            skArc(sketch, "E296", {"start": v(-23.08, -3.97) * mm, "mid": v(-23.2, -3.75) * mm, "end": v(-23.32, -3.54) * mm});
            skArc(sketch, "E297", {"start": v(-23.32, -3.54) * mm, "mid": v(-23.33, -3.52) * mm, "end": v(-23.35, -3.5) * mm});
            skArc(sketch, "E298", {"start": v(-23.35, -3.5) * mm, "mid": v(-23.37, -3.5) * mm, "end": v(-23.38, -3.52) * mm});
            skArc(sketch, "E299", {"start": v(-23.38, -3.52) * mm, "mid": v(-23.53, -3.8) * mm, "end": v(-23.67, -4.07) * mm});
            skArc(sketch, "E300", {"start": v(-23.67, -4.07) * mm, "mid": v(-23.83, -4.39) * mm, "end": v(-24, -4.7) * mm});
            skArc(sketch, "E301", {"start": v(-24, -4.7) * mm, "mid": v(-24.18, -5.09) * mm, "end": v(-24.37, -5.47) * mm});
            skArc(sketch, "E302", {"start": v(-24.37, -5.47) * mm, "mid": v(-24.9, -6.56) * mm, "end": v(-25.46, -7.65) * mm});
            skArc(sketch, "E303", {"start": v(-25.46, -7.65) * mm, "mid": v(-25.79, -8.26) * mm, "end": v(-26.14, -8.85) * mm});
            skArc(sketch, "E304", {"start": v(-26.14, -8.85) * mm, "mid": v(-26.4, -9.2) * mm, "end": v(-26.68, -9.53) * mm});
            skArc(sketch, "E305", {"start": v(-26.68, -9.53) * mm, "mid": v(-26.9, -9.72) * mm, "end": v(-27.17, -9.83) * mm});
            skArc(sketch, "E306", {"start": v(-27.17, -9.83) * mm, "mid": v(-27.36, -9.87) * mm, "end": v(-27.55, -9.9) * mm});
            skArc(sketch, "E307", {"start": v(-27.55, -9.9) * mm, "mid": v(-27.83, -9.9) * mm, "end": v(-28.12, -9.9) * mm});
            skArc(sketch, "E308", {"start": v(-28.12, -9.9) * mm, "mid": v(-28.44, -9.9) * mm, "end": v(-28.76, -9.88) * mm});
            skArc(sketch, "E309", {"start": v(-28.76, -9.88) * mm, "mid": v(-29.08, -9.85) * mm, "end": v(-29.4, -9.8) * mm});
            skArc(sketch, "E310", {"start": v(-29.4, -9.8) * mm, "mid": v(-29.6, -9.77) * mm, "end": v(-29.8, -9.74) * mm});
            skArc(sketch, "E311", {"start": v(-29.8, -9.74) * mm, "mid": v(-30.16, -9.67) * mm, "end": v(-30.53, -9.6) * mm});
            skArc(sketch, "E312", {"start": v(-30.53, -9.6) * mm, "mid": v(-30.95, -9.52) * mm, "end": v(-31.37, -9.44) * mm});
            skArc(sketch, "E313", {"start": v(-31.37, -9.44) * mm, "mid": v(-31.8, -9.36) * mm, "end": v(-32.24, -9.27) * mm});
            skArc(sketch, "E314", {"start": v(-32.24, -9.27) * mm, "mid": v(-32.67, -9.19) * mm, "end": v(-33.1, -9.1) * mm});
            skArc(sketch, "E315", {"start": v(-33.1, -9.1) * mm, "mid": v(-33.49, -9.04) * mm, "end": v(-33.88, -8.97) * mm});
            skArc(sketch, "E316", {"start": v(-33.88, -8.97) * mm, "mid": v(-34.2, -8.91) * mm, "end": v(-34.54, -8.86) * mm});
            skArc(sketch, "E317", {"start": v(-34.54, -8.86) * mm, "mid": v(-34.67, -8.84) * mm, "end": v(-34.8, -8.84) * mm});
            skArc(sketch, "E318", {"start": v(-34.8, -8.84) * mm, "mid": v(-34.92, -8.84) * mm, "end": v(-35.04, -8.84) * mm});
            skArc(sketch, "E319", {"start": v(-35.04, -8.84) * mm, "mid": v(-35.12, -8.85) * mm, "end": v(-35.2, -8.86) * mm});
            skArc(sketch, "E320", {"start": v(-35.2, -8.86) * mm, "mid": v(-35.26, -8.88) * mm, "end": v(-35.32, -8.91) * mm});
            skArc(sketch, "E321", {"start": v(-35.32, -8.91) * mm, "mid": v(-35.39, -8.96) * mm, "end": v(-35.45, -9.02) * mm});
            skArc(sketch, "E322", {"start": v(-35.45, -9.02) * mm, "mid": v(-35.58, -9.11) * mm, "end": v(-35.72, -9.19) * mm});
            skArc(sketch, "E323", {"start": v(-35.72, -9.19) * mm, "mid": v(-35.88, -9.25) * mm, "end": v(-36.05, -9.3) * mm});
            skArc(sketch, "E324", {"start": v(-36.05, -9.3) * mm, "mid": v(-36.3, -9.34) * mm, "end": v(-36.54, -9.36) * mm});
            skArc(sketch, "E325", {"start": v(-36.54, -9.36) * mm, "mid": v(-36.96, -9.4) * mm, "end": v(-37.38, -9.42) * mm});
            skArc(sketch, "E326", {"start": v(-37.38, -9.42) * mm, "mid": v(-37.8, -9.44) * mm, "end": v(-38.21, -9.45) * mm});
            skArc(sketch, "E327", {"start": v(-38.21, -9.45) * mm, "mid": v(-40.33, -9.46) * mm, "end": v(-42.45, -9.47) * mm});
            skArc(sketch, "E328", {"start": v(-42.45, -9.47) * mm, "mid": v(-44.93, -9.48) * mm, "end": v(-47.4, -9.48) * mm});
            skArc(sketch, "E329", {"start": v(-47.4, -9.48) * mm, "mid": v(-50.24, -9.49) * mm, "end": v(-53.07, -9.49) * mm});
            skLineSegment(sketch, "E330", {"start": v(-53.07, -9.49) * mm, "end": v(-67.63, -9.5) * mm});
            skLineSegment(sketch, "E331", {"start": v(-67.63, -9.5) * mm, "end": v(-68.2, -8.91) * mm});
            skLineSegment(sketch, "E332", {"start": v(-68.2, -8.91) * mm, "end": v(-68.78, -8.34) * mm});
            skLineSegment(sketch, "E333", {"start": v(-68.78, -8.34) * mm, "end": v(-68.78, -4.15) * mm});
            skLineSegment(sketch, "E334", {"start": v(-68.78, -4.15) * mm, "end": v(-68.78, 0.03) * mm});
            skLineSegment(sketch, "E335", {"start": v(-68.78, 0.03) * mm, "end": v(-70.07, 0.03) * mm});
            skLineSegment(sketch, "E336", {"start": v(-70.07, 0.03) * mm, "end": v(-71.35, 0.03) * mm});
            skLineSegment(sketch, "E337", {"start": v(-71.35, 0.03) * mm, "end": v(-71.4, -3.14) * mm});
            skArc(sketch, "E338", {"start": v(-71.4, -3.14) * mm, "mid": v(-71.42, -4.4) * mm, "end": v(-71.45, -5.67) * mm});
            skArc(sketch, "E339", {"start": v(-71.45, -5.67) * mm, "mid": v(-71.48, -6.35) * mm, "end": v(-71.53, -7.04) * mm});
            skArc(sketch, "E340", {"start": v(-71.53, -7.04) * mm, "mid": v(-71.59, -7.48) * mm, "end": v(-71.67, -7.92) * mm});
            skArc(sketch, "E341", {"start": v(-71.67, -7.92) * mm, "mid": v(-71.77, -8.26) * mm, "end": v(-71.9, -8.58) * mm});
            skArc(sketch, "E342", {"start": v(-71.9, -8.58) * mm, "mid": v(-71.97, -8.7) * mm, "end": v(-72.05, -8.83) * mm});
            skArc(sketch, "E343", {"start": v(-72.05, -8.83) * mm, "mid": v(-72.12, -8.93) * mm, "end": v(-72.2, -9.03) * mm});
            skArc(sketch, "E344", {"start": v(-72.2, -9.03) * mm, "mid": v(-72.3, -9.1) * mm, "end": v(-72.39, -9.17) * mm});
            skArc(sketch, "E345", {"start": v(-72.39, -9.17) * mm, "mid": v(-72.48, -9.23) * mm, "end": v(-72.59, -9.28) * mm});
            skArc(sketch, "E346", {"start": v(-72.59, -9.28) * mm, "mid": v(-72.83, -9.35) * mm, "end": v(-73.09, -9.38) * mm});
            skArc(sketch, "E347", {"start": v(-73.09, -9.38) * mm, "mid": v(-73.7, -9.42) * mm, "end": v(-74.33, -9.45) * mm});
            skArc(sketch, "E348", {"start": v(-74.33, -9.45) * mm, "mid": v(-75.18, -9.47) * mm, "end": v(-76.04, -9.48) * mm});
            skArc(sketch, "E349", {"start": v(-76.04, -9.48) * mm, "mid": v(-77.24, -9.48) * mm, "end": v(-78.44, -9.48) * mm});
            skArc(sketch, "E350", {"start": v(-78.44, -9.48) * mm, "mid": v(-79.62, -9.47) * mm, "end": v(-80.79, -9.46) * mm});
            skArc(sketch, "E351", {"start": v(-80.79, -9.46) * mm, "mid": v(-81.22, -9.45) * mm, "end": v(-81.66, -9.44) * mm});
            skArc(sketch, "E352", {"start": v(-81.66, -9.44) * mm, "mid": v(-81.9, -9.42) * mm, "end": v(-82.13, -9.4) * mm});
            skArc(sketch, "E353", {"start": v(-82.13, -9.4) * mm, "mid": v(-82.29, -9.36) * mm, "end": v(-82.43, -9.31) * mm});
            skArc(sketch, "E354", {"start": v(-82.43, -9.31) * mm, "mid": v(-82.58, -9.23) * mm, "end": v(-82.72, -9.13) * mm});
            skArc(sketch, "E355", {"start": v(-82.72, -9.13) * mm, "mid": v(-82.86, -9.02) * mm, "end": v(-82.98, -8.89) * mm});
            skArc(sketch, "E356", {"start": v(-82.98, -8.89) * mm, "mid": v(-83.11, -8.73) * mm, "end": v(-83.22, -8.56) * mm});
            skArc(sketch, "E357", {"start": v(-83.22, -8.56) * mm, "mid": v(-83.34, -8.37) * mm, "end": v(-83.44, -8.16) * mm});
            skLineSegment(sketch, "E358", {"start": v(-83.44, -8.16) * mm, "end": v(-83.66, -7.7) * mm});
            skLineSegment(sketch, "E359", {"start": v(-83.66, -7.7) * mm, "end": v(-83.68, 1.7) * mm});
            skArc(sketch, "E360", {"start": v(-83.68, 1.7) * mm, "mid": v(-83.69, 3.67) * mm, "end": v(-83.69, 5.63) * mm});
            skArc(sketch, "E361", {"start": v(-83.69, 5.63) * mm, "mid": v(-83.69, 7.62) * mm, "end": v(-83.68, 9.62) * mm});
            skArc(sketch, "E362", {"start": v(-83.68, 9.62) * mm, "mid": v(-83.68, 11.38) * mm, "end": v(-83.67, 13.15) * mm});
            skArc(sketch, "E363", {"start": v(-83.67, 13.15) * mm, "mid": v(-83.67, 14.28) * mm, "end": v(-83.66, 15.41) * mm});
            skLineSegment(sketch, "E364", {"start": v(-83.66, 15.41) * mm, "end": v(-83.6, 19.7) * mm});
            skLineSegment(sketch, "E365", {"start": v(-83.6, 19.7) * mm, "end": v(-82.86, 20.37) * mm});
            skLineSegment(sketch, "E366", {"start": v(-82.86, 20.37) * mm, "end": v(-82.12, 21.04) * mm});
            skLineSegment(sketch, "E367", {"start": v(-82.12, 21.04) * mm, "end": v(-78.02, 21.01) * mm});
            skArc(sketch, "E368", {"start": v(-78.02, 21.01) * mm, "mid": v(-76.72, 21) * mm, "end": v(-75.42, 21) * mm});
            skArc(sketch, "E369", {"start": v(-75.42, 21) * mm, "mid": v(-74.92, 20.98) * mm, "end": v(-74.42, 20.97) * mm});
            skArc(sketch, "E370", {"start": v(-74.42, 20.97) * mm, "mid": v(-74.13, 20.95) * mm, "end": v(-73.83, 20.92) * mm});
            skArc(sketch, "E371", {"start": v(-73.83, 20.92) * mm, "mid": v(-73.6, 20.88) * mm, "end": v(-73.37, 20.83) * mm});
            skArc(sketch, "E372", {"start": v(-73.37, 20.83) * mm, "mid": v(-73.06, 20.73) * mm, "end": v(-72.75, 20.6) * mm});
            skArc(sketch, "E373", {"start": v(-72.75, 20.6) * mm, "mid": v(-72.53, 20.47) * mm, "end": v(-72.33, 20.3) * mm});
            skArc(sketch, "E374", {"start": v(-72.33, 20.3) * mm, "mid": v(-72.17, 20.11) * mm, "end": v(-72.04, 19.9) * mm});
            skArc(sketch, "E375", {"start": v(-72.04, 19.9) * mm, "mid": v(-71.92, 19.59) * mm, "end": v(-71.82, 19.28) * mm});
            skArc(sketch, "E376", {"start": v(-71.82, 19.28) * mm, "mid": v(-71.78, 19.08) * mm, "end": v(-71.76, 18.89) * mm});
            skArc(sketch, "E377", {"start": v(-71.76, 18.89) * mm, "mid": v(-71.73, 18.56) * mm, "end": v(-71.72, 18.24) * mm});
            skArc(sketch, "E378", {"start": v(-71.72, 18.24) * mm, "mid": v(-71.7, 17.7) * mm, "end": v(-71.7, 17.17) * mm});
            skArc(sketch, "E379", {"start": v(-71.7, 17.17) * mm, "mid": v(-71.68, 16.1) * mm, "end": v(-71.67, 15.03) * mm});
            skLineSegment(sketch, "E380", {"start": v(-71.67, 15.03) * mm, "end": v(-71.64, 11.23) * mm});
            skLineSegment(sketch, "E381", {"start": v(-71.64, 11.23) * mm, "end": v(-70.23, 11.25) * mm});
            skLineSegment(sketch, "E382", {"start": v(-70.23, 11.25) * mm, "end": v(-68.82, 11.26) * mm});
            skLineSegment(sketch, "E383", {"start": v(-68.82, 11.26) * mm, "end": v(-68.78, 15.04) * mm});
            skArc(sketch, "E384", {"start": v(-68.78, 15.04) * mm, "mid": v(-68.77, 16.08) * mm, "end": v(-68.75, 17.1) * mm});
            skArc(sketch, "E385", {"start": v(-68.75, 17.1) * mm, "mid": v(-68.74, 17.66) * mm, "end": v(-68.72, 18.21) * mm});
            skArc(sketch, "E386", {"start": v(-68.72, 18.21) * mm, "mid": v(-68.7, 18.56) * mm, "end": v(-68.68, 18.9) * mm});
            skArc(sketch, "E387", {"start": v(-68.68, 18.9) * mm, "mid": v(-68.66, 19.1) * mm, "end": v(-68.62, 19.31) * mm});
            skArc(sketch, "E388", {"start": v(-68.62, 19.31) * mm, "mid": v(-68.56, 19.55) * mm, "end": v(-68.48, 19.78) * mm});
            skArc(sketch, "E389", {"start": v(-68.48, 19.78) * mm, "mid": v(-68.4, 19.97) * mm, "end": v(-68.3, 20.14) * mm});
            skArc(sketch, "E390", {"start": v(-68.3, 20.14) * mm, "mid": v(-68.18, 20.29) * mm, "end": v(-68.05, 20.42) * mm});
            skArc(sketch, "E391", {"start": v(-68.05, 20.42) * mm, "mid": v(-67.9, 20.53) * mm, "end": v(-67.73, 20.62) * mm});
            skLineSegment(sketch, "E392", {"start": v(-67.73, 20.62) * mm, "end": v(-67.35, 20.82) * mm});
            skLineSegment(sketch, "E393", {"start": v(-67.35, 20.82) * mm, "end": v(-64.86, 20.89) * mm});
            skArc(sketch, "E394", {"start": v(-64.86, 20.89) * mm, "mid": v(-61.49, 20.97) * mm, "end": v(-58.1, 21.01) * mm});
            skArc(sketch, "E395", {"start": v(-58.1, 21.01) * mm, "mid": v(-53.33, 21.05) * mm, "end": v(-48.56, 21.07) * mm});
            skArc(sketch, "E396", {"start": v(-48.56, 21.07) * mm, "mid": v(-43.64, 21.08) * mm, "end": v(-38.73, 21.08) * mm});
            skArc(sketch, "E397", {"start": v(-38.73, 21.08) * mm, "mid": v(-37.67, 21.04) * mm, "end": v(-36.62, 20.95) * mm});
            skArc(sketch, "E398", {"start": v(-36.62, 20.95) * mm, "mid": v(-36.28, 20.92) * mm, "end": v(-35.94, 20.91) * mm});
            skArc(sketch, "E399", {"start": v(-35.94, 20.91) * mm, "mid": v(-35.42, 20.92) * mm, "end": v(-34.9, 20.94) * mm});
            skArc(sketch, "E400", {"start": v(-34.9, 20.94) * mm, "mid": v(-34.14, 20.98) * mm, "end": v(-33.4, 21.03) * mm});
            skArc(sketch, "E401", {"start": v(-33.4, 21.03) * mm, "mid": v(-32.26, 21.12) * mm, "end": v(-31.12, 21.2) * mm});
            skArc(sketch, "E402", {"start": v(-31.12, 21.2) * mm, "mid": v(-30.2, 21.28) * mm, "end": v(-29.28, 21.35) * mm});
            skArc(sketch, "E403", {"start": v(-29.28, 21.35) * mm, "mid": v(-28.55, 21.39) * mm, "end": v(-27.82, 21.42) * mm});
            skArc(sketch, "E404", {"start": v(-27.82, 21.42) * mm, "mid": v(-27.27, 21.44) * mm, "end": v(-26.7, 21.45) * mm});
            skArc(sketch, "E405", {"start": v(-26.7, 21.45) * mm, "mid": v(-26.48, 21.43) * mm, "end": v(-26.25, 21.39) * mm});
            skArc(sketch, "E406", {"start": v(-26.25, 21.39) * mm, "mid": v(-26.01, 21.29) * mm, "end": v(-25.81, 21.13) * mm});
            skArc(sketch, "E407", {"start": v(-25.81, 21.13) * mm, "mid": v(-25.57, 20.87) * mm, "end": v(-25.35, 20.58) * mm});
            skArc(sketch, "E408", {"start": v(-25.35, 20.58) * mm, "mid": v(-25.05, 20.11) * mm, "end": v(-24.77, 19.63) * mm});
            skArc(sketch, "E409", {"start": v(-24.77, 19.63) * mm, "mid": v(-24.33, 18.8) * mm, "end": v(-23.9, 17.98) * mm});
            skArc(sketch, "E410", {"start": v(-23.9, 17.98) * mm, "mid": v(-23.77, 17.7) * mm, "end": v(-23.62, 17.43) * mm});
            skArc(sketch, "E411", {"start": v(-23.62, 17.43) * mm, "mid": v(-23.5, 17.2) * mm, "end": v(-23.38, 16.97) * mm});
            skArc(sketch, "E412", {"start": v(-23.38, 16.97) * mm, "mid": v(-23.27, 16.77) * mm, "end": v(-23.16, 16.57) * mm});
            skArc(sketch, "E413", {"start": v(-23.16, 16.57) * mm, "mid": v(-23.15, 16.55) * mm, "end": v(-23.14, 16.55) * mm});
            skArc(sketch, "E414", {"start": v(-23.14, 16.55) * mm, "mid": v(-23.12, 16.55) * mm, "end": v(-23.11, 16.57) * mm});
            skArc(sketch, "E415", {"start": v(-23.11, 16.57) * mm, "mid": v(-23, 16.79) * mm, "end": v(-22.9, 17) * mm});
            skArc(sketch, "E416", {"start": v(-22.9, 17) * mm, "mid": v(-22.8, 17.26) * mm, "end": v(-22.68, 17.5) * mm});
            skArc(sketch, "E417", {"start": v(-22.68, 17.5) * mm, "mid": v(-22.54, 17.8) * mm, "end": v(-22.41, 18.1) * mm});
            skArc(sketch, "E418", {"start": v(-22.41, 18.1) * mm, "mid": v(-22.27, 18.42) * mm, "end": v(-22.13, 18.74) * mm});
            skArc(sketch, "E419", {"start": v(-22.13, 18.74) * mm, "mid": v(-22, 19.05) * mm, "end": v(-21.86, 19.35) * mm});
            skArc(sketch, "E420", {"start": v(-21.86, 19.35) * mm, "mid": v(-21.74, 19.62) * mm, "end": v(-21.63, 19.88) * mm});
            skArc(sketch, "E421", {"start": v(-21.63, 19.88) * mm, "mid": v(-21.56, 20.02) * mm, "end": v(-21.5, 20.17) * mm});
            skArc(sketch, "E422", {"start": v(-21.5, 20.17) * mm, "mid": v(-21.36, 20.43) * mm, "end": v(-21.2, 20.67) * mm});
            skArc(sketch, "E423", {"start": v(-21.2, 20.67) * mm, "mid": v(-21.04, 20.9) * mm, "end": v(-20.84, 21.1) * mm});
            skArc(sketch, "E424", {"start": v(-20.84, 21.1) * mm, "mid": v(-20.64, 21.26) * mm, "end": v(-20.42, 21.4) * mm});
            skArc(sketch, "E425", {"start": v(-20.42, 21.4) * mm, "mid": v(-20.2, 21.52) * mm, "end": v(-19.96, 21.6) * mm});
            skArc(sketch, "E426", {"start": v(-19.96, 21.6) * mm, "mid": v(-19.78, 21.63) * mm, "end": v(-19.6, 21.64) * mm});
            skArc(sketch, "E427", {"start": v(-19.6, 21.64) * mm, "mid": v(-19.2, 21.63) * mm, "end": v(-18.8, 21.61) * mm});
            skArc(sketch, "E428", {"start": v(-18.8, 21.61) * mm, "mid": v(-18.27, 21.58) * mm, "end": v(-17.74, 21.54) * mm});
            skArc(sketch, "E429", {"start": v(-17.74, 21.54) * mm, "mid": v(-17.06, 21.48) * mm, "end": v(-16.39, 21.41) * mm});
            skArc(sketch, "E430", {"start": v(38.81, -12.33) * mm, "mid": v(38.94, -12.43) * mm, "end": v(39.06, -12.55) * mm});
            skArc(sketch, "E431", {"start": v(39.06, -12.55) * mm, "mid": v(39.2, -12.72) * mm, "end": v(39.34, -12.89) * mm});
            skArc(sketch, "E432", {"start": v(39.34, -12.89) * mm, "mid": v(39.48, -13.07) * mm, "end": v(39.6, -13.26) * mm});
            skArc(sketch, "E433", {"start": v(39.6, -13.26) * mm, "mid": v(39.71, -13.44) * mm, "end": v(39.8, -13.62) * mm});
            skArc(sketch, "E434", {"start": v(39.8, -13.62) * mm, "mid": v(39.87, -13.75) * mm, "end": v(39.92, -13.88) * mm});
            skArc(sketch, "E435", {"start": v(39.92, -13.88) * mm, "mid": v(39.96, -13.98) * mm, "end": v(39.99, -14.08) * mm});
            skArc(sketch, "E436", {"start": v(39.99, -14.08) * mm, "mid": v(40, -14.18) * mm, "end": v(40.02, -14.29) * mm});
            skArc(sketch, "E437", {"start": v(40.02, -14.29) * mm, "mid": v(40.03, -14.43) * mm, "end": v(40.03, -14.56) * mm});
            skArc(sketch, "E438", {"start": v(40.03, -14.56) * mm, "mid": v(40.01, -14.85) * mm, "end": v(39.96, -15.13) * mm});
            skArc(sketch, "E439", {"start": v(39.96, -15.13) * mm, "mid": v(39.87, -15.35) * mm, "end": v(39.75, -15.55) * mm});
            skArc(sketch, "E440", {"start": v(39.75, -15.55) * mm, "mid": v(39.57, -15.74) * mm, "end": v(39.36, -15.88) * mm});
            skArc(sketch, "E441", {"start": v(39.36, -15.88) * mm, "mid": v(39.07, -16.02) * mm, "end": v(38.77, -16.14) * mm});
            skArc(sketch, "E442", {"start": v(38.77, -16.14) * mm, "mid": v(38.53, -16.23) * mm, "end": v(38.3, -16.34) * mm});
            skArc(sketch, "E443", {"start": v(38.3, -16.34) * mm, "mid": v(38.16, -16.44) * mm, "end": v(38.05, -16.58) * mm});
            skArc(sketch, "E444", {"start": v(38.05, -16.58) * mm, "mid": v(37.99, -16.71) * mm, "end": v(37.98, -16.86) * mm});
            skArc(sketch, "E445", {"start": v(37.98, -16.86) * mm, "mid": v(38, -17.05) * mm, "end": v(38.07, -17.22) * mm});
            skArc(sketch, "E446", {"start": v(38.07, -17.22) * mm, "mid": v(38.1, -17.28) * mm, "end": v(38.14, -17.34) * mm});
            skArc(sketch, "E447", {"start": v(38.14, -17.34) * mm, "mid": v(38.22, -17.45) * mm, "end": v(38.3, -17.55) * mm});
            skArc(sketch, "E448", {"start": v(38.3, -17.55) * mm, "mid": v(38.4, -17.67) * mm, "end": v(38.5, -17.8) * mm});
            skArc(sketch, "E449", {"start": v(38.5, -17.8) * mm, "mid": v(38.6, -17.92) * mm, "end": v(38.71, -18.04) * mm});
            skArc(sketch, "E450", {"start": v(38.71, -18.04) * mm, "mid": v(38.95, -18.31) * mm, "end": v(39.19, -18.6) * mm});
            skArc(sketch, "E451", {"start": v(39.19, -18.6) * mm, "mid": v(39.36, -18.82) * mm, "end": v(39.52, -19.05) * mm});
            skArc(sketch, "E452", {"start": v(39.52, -19.05) * mm, "mid": v(39.63, -19.23) * mm, "end": v(39.72, -19.43) * mm});
            skArc(sketch, "E453", {"start": v(39.72, -19.43) * mm, "mid": v(39.77, -19.56) * mm, "end": v(39.78, -19.7) * mm});
            skArc(sketch, "E454", {"start": v(39.78, -19.7) * mm, "mid": v(39.74, -20.03) * mm, "end": v(39.62, -20.33) * mm});
            skArc(sketch, "E455", {"start": v(39.62, -20.33) * mm, "mid": v(39.4, -20.65) * mm, "end": v(39.14, -20.94) * mm});
            skArc(sketch, "E456", {"start": v(39.14, -20.94) * mm, "mid": v(38.83, -21.2) * mm, "end": v(38.48, -21.4) * mm});
            skArc(sketch, "E457", {"start": v(38.48, -21.4) * mm, "mid": v(38.16, -21.52) * mm, "end": v(37.82, -21.56) * mm});
            skArc(sketch, "E458", {"start": v(37.82, -21.56) * mm, "mid": v(37.72, -21.56) * mm, "end": v(37.62, -21.55) * mm});
            skArc(sketch, "E459", {"start": v(37.62, -21.55) * mm, "mid": v(37.54, -21.53) * mm, "end": v(37.46, -21.5) * mm});
            skArc(sketch, "E460", {"start": v(37.46, -21.5) * mm, "mid": v(37.36, -21.46) * mm, "end": v(37.27, -21.4) * mm});
            skArc(sketch, "E461", {"start": v(37.27, -21.4) * mm, "mid": v(37.13, -21.31) * mm, "end": v(36.98, -21.22) * mm});
            skArc(sketch, "E462", {"start": v(36.98, -21.22) * mm, "mid": v(36.86, -21.13) * mm, "end": v(36.75, -21.05) * mm});
            skArc(sketch, "E463", {"start": v(36.75, -21.05) * mm, "mid": v(36.6, -20.93) * mm, "end": v(36.45, -20.81) * mm});
            skArc(sketch, "E464", {"start": v(36.45, -20.81) * mm, "mid": v(36.3, -20.69) * mm, "end": v(36.16, -20.56) * mm});
            skArc(sketch, "E465", {"start": v(36.16, -20.56) * mm, "mid": v(36.03, -20.45) * mm, "end": v(35.9, -20.33) * mm});
            skLineSegment(sketch, "E466", {"start": v(35.9, -20.33) * mm, "end": v(35.33, -19.78) * mm});
            skLineSegment(sketch, "E467", {"start": v(35.33, -19.78) * mm, "end": v(34.95, -20.07) * mm});
            skArc(sketch, "E468", {"start": v(34.95, -20.07) * mm, "mid": v(34.56, -20.35) * mm, "end": v(34.16, -20.61) * mm});
            skArc(sketch, "E469", {"start": v(34.16, -20.61) * mm, "mid": v(33.73, -20.87) * mm, "end": v(33.3, -21.12) * mm});
            skArc(sketch, "E470", {"start": v(33.3, -21.12) * mm, "mid": v(32.9, -21.32) * mm, "end": v(32.5, -21.5) * mm});
            skArc(sketch, "E471", {"start": v(32.5, -21.5) * mm, "mid": v(32.3, -21.58) * mm, "end": v(32.09, -21.6) * mm});
            skArc(sketch, "E472", {"start": v(32.09, -21.6) * mm, "mid": v(31.85, -21.58) * mm, "end": v(31.62, -21.5) * mm});
            skArc(sketch, "E473", {"start": v(31.62, -21.5) * mm, "mid": v(31.38, -21.37) * mm, "end": v(31.16, -21.2) * mm});
            skArc(sketch, "E474", {"start": v(31.16, -21.2) * mm, "mid": v(30.95, -21) * mm, "end": v(30.76, -20.78) * mm});
            skArc(sketch, "E475", {"start": v(30.76, -20.78) * mm, "mid": v(30.62, -20.53) * mm, "end": v(30.51, -20.27) * mm});
            skArc(sketch, "E476", {"start": v(30.51, -20.27) * mm, "mid": v(30.46, -20.1) * mm, "end": v(30.42, -19.92) * mm});
            skArc(sketch, "E477", {"start": v(30.42, -19.92) * mm, "mid": v(30.4, -19.74) * mm, "end": v(30.39, -19.55) * mm});
            skArc(sketch, "E478", {"start": v(30.39, -19.55) * mm, "mid": v(30.39, -19.38) * mm, "end": v(30.4, -19.21) * mm});
            skArc(sketch, "E479", {"start": v(30.4, -19.21) * mm, "mid": v(30.42, -19.1) * mm, "end": v(30.47, -18.98) * mm});
            skArc(sketch, "E480", {"start": v(30.47, -18.98) * mm, "mid": v(30.55, -18.86) * mm, "end": v(30.65, -18.76) * mm});
            skArc(sketch, "E481", {"start": v(30.65, -18.76) * mm, "mid": v(30.88, -18.58) * mm, "end": v(31.1, -18.4) * mm});
            skArc(sketch, "E482", {"start": v(31.1, -18.4) * mm, "mid": v(31.42, -18.17) * mm, "end": v(31.75, -17.94) * mm});
            skArc(sketch, "E483", {"start": v(31.75, -17.94) * mm, "mid": v(32.2, -17.65) * mm, "end": v(32.64, -17.36) * mm});
            skLineSegment(sketch, "E484", {"start": v(32.64, -17.36) * mm, "end": v(33.72, -16.67) * mm});
            skLineSegment(sketch, "E485", {"start": v(33.72, -16.67) * mm, "end": v(33.2, -16.61) * mm});
            skArc(sketch, "E486", {"start": v(33.2, -16.61) * mm, "mid": v(32.8, -16.56) * mm, "end": v(32.4, -16.5) * mm});
            skArc(sketch, "E487", {"start": v(32.4, -16.5) * mm, "mid": v(32.12, -16.43) * mm, "end": v(31.87, -16.32) * mm});
            skArc(sketch, "E488", {"start": v(31.87, -16.32) * mm, "mid": v(31.68, -16.2) * mm, "end": v(31.5, -16.06) * mm});
            skArc(sketch, "E489", {"start": v(31.5, -16.06) * mm, "mid": v(31.36, -15.88) * mm, "end": v(31.24, -15.68) * mm});
            skArc(sketch, "E490", {"start": v(31.24, -15.68) * mm, "mid": v(31.2, -15.59) * mm, "end": v(31.16, -15.49) * mm});
            skArc(sketch, "E491", {"start": v(31.16, -15.49) * mm, "mid": v(31.14, -15.4) * mm, "end": v(31.11, -15.3) * mm});
            skArc(sketch, "E492", {"start": v(31.11, -15.3) * mm, "mid": v(31.1, -15.2) * mm, "end": v(31.09, -15.1) * mm});
            skArc(sketch, "E493", {"start": v(31.09, -15.1) * mm, "mid": v(31.08, -14.95) * mm, "end": v(31.08, -14.82) * mm});
            skArc(sketch, "E494", {"start": v(31.08, -14.82) * mm, "mid": v(31.09, -14.53) * mm, "end": v(31.13, -14.25) * mm});
            skArc(sketch, "E495", {"start": v(31.13, -14.25) * mm, "mid": v(31.2, -14.03) * mm, "end": v(31.32, -13.83) * mm});
            skArc(sketch, "E496", {"start": v(31.32, -13.83) * mm, "mid": v(31.47, -13.66) * mm, "end": v(31.66, -13.53) * mm});
            skArc(sketch, "E497", {"start": v(31.66, -13.53) * mm, "mid": v(31.9, -13.4) * mm, "end": v(32.17, -13.3) * mm});
            skArc(sketch, "E498", {"start": v(32.17, -13.3) * mm, "mid": v(32.32, -13.27) * mm, "end": v(32.47, -13.24) * mm});
            skArc(sketch, "E499", {"start": v(32.47, -13.24) * mm, "mid": v(32.67, -13.2) * mm, "end": v(32.88, -13.18) * mm});
            skArc(sketch, "E500", {"start": v(32.88, -13.18) * mm, "mid": v(33.2, -13.14) * mm, "end": v(33.53, -13.1) * mm});
            skArc(sketch, "E501", {"start": v(33.53, -13.1) * mm, "mid": v(34.12, -13.05) * mm, "end": v(34.71, -13) * mm});
            skArc(sketch, "E502", {"start": v(34.71, -13) * mm, "mid": v(35, -12.96) * mm, "end": v(35.28, -12.92) * mm});
            skArc(sketch, "E503", {"start": v(35.28, -12.92) * mm, "mid": v(35.5, -12.89) * mm, "end": v(35.73, -12.84) * mm});
            skArc(sketch, "E504", {"start": v(35.73, -12.84) * mm, "mid": v(35.94, -12.78) * mm, "end": v(36.15, -12.72) * mm});
            skArc(sketch, "E505", {"start": v(36.15, -12.72) * mm, "mid": v(36.39, -12.63) * mm, "end": v(36.63, -12.54) * mm});
            skArc(sketch, "E506", {"start": v(36.63, -12.54) * mm, "mid": v(36.95, -12.41) * mm, "end": v(37.29, -12.3) * mm});
            skArc(sketch, "E507", {"start": v(37.29, -12.3) * mm, "mid": v(37.6, -12.24) * mm, "end": v(37.93, -12.2) * mm});
            skArc(sketch, "E508", {"start": v(37.93, -12.2) * mm, "mid": v(38.2, -12.18) * mm, "end": v(38.47, -12.2) * mm});
            skArc(sketch, "E509", {"start": v(38.47, -12.2) * mm, "mid": v(38.65, -12.24) * mm, "end": v(38.81, -12.33) * mm});
            skArc(sketch, "E510", {"start": v(-23.74, -12.98) * mm, "mid": v(-23.68, -13.01) * mm, "end": v(-23.62, -13.05) * mm});
            skArc(sketch, "E511", {"start": v(-23.62, -13.05) * mm, "mid": v(-23.56, -13.09) * mm, "end": v(-23.5, -13.13) * mm});
            skArc(sketch, "E512", {"start": v(-23.5, -13.13) * mm, "mid": v(-23.43, -13.17) * mm, "end": v(-23.38, -13.22) * mm});
            skArc(sketch, "E513", {"start": v(-23.38, -13.22) * mm, "mid": v(-23.33, -13.26) * mm, "end": v(-23.3, -13.3) * mm});
            skArc(sketch, "E514", {"start": v(-23.3, -13.3) * mm, "mid": v(-23.2, -13.37) * mm, "end": v(-23.11, -13.43) * mm});
            skArc(sketch, "E515", {"start": v(-23.11, -13.43) * mm, "mid": v(-23.01, -13.46) * mm, "end": v(-22.9, -13.47) * mm});
            skArc(sketch, "E516", {"start": v(-22.9, -13.47) * mm, "mid": v(-22.78, -13.46) * mm, "end": v(-22.65, -13.42) * mm});
            skArc(sketch, "E517", {"start": v(-22.65, -13.42) * mm, "mid": v(-22.48, -13.35) * mm, "end": v(-22.3, -13.27) * mm});
            skArc(sketch, "E518", {"start": v(-22.3, -13.27) * mm, "mid": v(-22.22, -13.23) * mm, "end": v(-22.13, -13.2) * mm});
            skArc(sketch, "E519", {"start": v(-22.13, -13.2) * mm, "mid": v(-22.05, -13.16) * mm, "end": v(-21.96, -13.12) * mm});
            skArc(sketch, "E520", {"start": v(-21.96, -13.12) * mm, "mid": v(-21.88, -13.1) * mm, "end": v(-21.8, -13.07) * mm});
            skArc(sketch, "E521", {"start": v(-21.8, -13.07) * mm, "mid": v(-21.76, -13.06) * mm, "end": v(-21.7, -13.06) * mm});
            skArc(sketch, "E522", {"start": v(-21.7, -13.06) * mm, "mid": v(-21.44, -13.1) * mm, "end": v(-21.2, -13.2) * mm});
            skArc(sketch, "E523", {"start": v(-21.2, -13.2) * mm, "mid": v(-20.77, -13.48) * mm, "end": v(-20.36, -13.77) * mm});
            skArc(sketch, "E524", {"start": v(-20.36, -13.77) * mm, "mid": v(-19.93, -14.12) * mm, "end": v(-19.52, -14.48) * mm});
            skArc(sketch, "E525", {"start": v(-19.52, -14.48) * mm, "mid": v(-19.2, -14.82) * mm, "end": v(-18.9, -15.19) * mm});
            skArc(sketch, "E526", {"start": v(-18.9, -15.19) * mm, "mid": v(-18.83, -15.28) * mm, "end": v(-18.77, -15.37) * mm});
            skArc(sketch, "E527", {"start": v(-18.77, -15.37) * mm, "mid": v(-18.71, -15.48) * mm, "end": v(-18.65, -15.59) * mm});
            skArc(sketch, "E528", {"start": v(-18.65, -15.59) * mm, "mid": v(-18.6, -15.7) * mm, "end": v(-18.55, -15.8) * mm});
            skArc(sketch, "E529", {"start": v(-18.55, -15.8) * mm, "mid": v(-18.51, -15.88) * mm, "end": v(-18.49, -15.97) * mm});
            skArc(sketch, "E530", {"start": v(-18.49, -15.97) * mm, "mid": v(-18.44, -16.15) * mm, "end": v(-18.42, -16.33) * mm});
            skArc(sketch, "E531", {"start": v(-18.42, -16.33) * mm, "mid": v(-18.43, -16.49) * mm, "end": v(-18.46, -16.64) * mm});
            skArc(sketch, "E532", {"start": v(-18.46, -16.64) * mm, "mid": v(-18.52, -16.8) * mm, "end": v(-18.6, -16.95) * mm});
            skArc(sketch, "E533", {"start": v(-18.6, -16.95) * mm, "mid": v(-18.73, -17.13) * mm, "end": v(-18.88, -17.3) * mm});
            skArc(sketch, "E534", {"start": v(-18.88, -17.3) * mm, "mid": v(-18.95, -17.37) * mm, "end": v(-19.01, -17.45) * mm});
            skArc(sketch, "E535", {"start": v(-19.01, -17.45) * mm, "mid": v(-19.07, -17.52) * mm, "end": v(-19.12, -17.59) * mm});
            skArc(sketch, "E536", {"start": v(-19.12, -17.59) * mm, "mid": v(-19.17, -17.65) * mm, "end": v(-19.21, -17.7) * mm});
            skArc(sketch, "E537", {"start": v(-19.21, -17.7) * mm, "mid": v(-19.22, -17.73) * mm, "end": v(-19.22, -17.75) * mm});
            skArc(sketch, "E538", {"start": v(-19.22, -17.75) * mm, "mid": v(-19.22, -17.77) * mm, "end": v(-19.21, -17.79) * mm});
            skArc(sketch, "E539", {"start": v(-19.21, -17.79) * mm, "mid": v(-19.18, -17.84) * mm, "end": v(-19.14, -17.89) * mm});
            skArc(sketch, "E540", {"start": v(-19.14, -17.89) * mm, "mid": v(-19.1, -17.95) * mm, "end": v(-19.05, -18) * mm});
            skArc(sketch, "E541", {"start": v(-19.05, -18) * mm, "mid": v(-19, -18.07) * mm, "end": v(-18.94, -18.14) * mm});
            skArc(sketch, "E542", {"start": v(-18.94, -18.14) * mm, "mid": v(-18.73, -18.42) * mm, "end": v(-18.56, -18.73) * mm});
            skArc(sketch, "E543", {"start": v(-18.56, -18.73) * mm, "mid": v(-18.47, -19) * mm, "end": v(-18.46, -19.28) * mm});
            skArc(sketch, "E544", {"start": v(-18.46, -19.28) * mm, "mid": v(-18.51, -19.57) * mm, "end": v(-18.64, -19.84) * mm});
            skArc(sketch, "E545", {"start": v(-18.64, -19.84) * mm, "mid": v(-18.86, -20.17) * mm, "end": v(-19.1, -20.47) * mm});
            skArc(sketch, "E546", {"start": v(-19.1, -20.47) * mm, "mid": v(-19.27, -20.63) * mm, "end": v(-19.45, -20.78) * mm});
            skArc(sketch, "E547", {"start": v(-19.45, -20.78) * mm, "mid": v(-19.6, -20.9) * mm, "end": v(-19.77, -20.99) * mm});
            skArc(sketch, "E548", {"start": v(-19.77, -20.99) * mm, "mid": v(-19.94, -21.06) * mm, "end": v(-20.12, -21.11) * mm});
            skArc(sketch, "E549", {"start": v(-20.12, -21.11) * mm, "mid": v(-20.36, -21.16) * mm, "end": v(-20.59, -21.19) * mm});
            skArc(sketch, "E550", {"start": v(-20.59, -21.19) * mm, "mid": v(-20.72, -21.2) * mm, "end": v(-20.84, -21.22) * mm});
            skArc(sketch, "E551", {"start": v(-20.84, -21.22) * mm, "mid": v(-20.98, -21.25) * mm, "end": v(-21.13, -21.28) * mm});
            skArc(sketch, "E552", {"start": v(-21.13, -21.28) * mm, "mid": v(-21.27, -21.31) * mm, "end": v(-21.41, -21.35) * mm});
            skArc(sketch, "E553", {"start": v(-21.41, -21.35) * mm, "mid": v(-21.53, -21.38) * mm, "end": v(-21.64, -21.42) * mm});
            skArc(sketch, "E554", {"start": v(-21.64, -21.42) * mm, "mid": v(-22, -21.53) * mm, "end": v(-22.39, -21.6) * mm});
            skArc(sketch, "E555", {"start": v(-22.39, -21.6) * mm, "mid": v(-22.73, -21.64) * mm, "end": v(-23.07, -21.63) * mm});
            skArc(sketch, "E556", {"start": v(-23.07, -21.63) * mm, "mid": v(-23.44, -21.58) * mm, "end": v(-23.8, -21.49) * mm});
            skArc(sketch, "E557", {"start": v(-23.8, -21.49) * mm, "mid": v(-24.25, -21.33) * mm, "end": v(-24.7, -21.16) * mm});
            skArc(sketch, "E558", {"start": v(-24.7, -21.16) * mm, "mid": v(-24.86, -21.09) * mm, "end": v(-25.02, -21.03) * mm});
            skArc(sketch, "E559", {"start": v(-25.02, -21.03) * mm, "mid": v(-25.2, -20.97) * mm, "end": v(-25.37, -20.9) * mm});
            skArc(sketch, "E560", {"start": v(-25.37, -20.9) * mm, "mid": v(-25.53, -20.86) * mm, "end": v(-25.7, -20.8) * mm});
            skArc(sketch, "E561", {"start": v(-25.7, -20.8) * mm, "mid": v(-25.8, -20.78) * mm, "end": v(-25.92, -20.76) * mm});
            skArc(sketch, "E562", {"start": v(-25.92, -20.76) * mm, "mid": v(-26.03, -20.74) * mm, "end": v(-26.13, -20.71) * mm});
            skArc(sketch, "E563", {"start": v(-26.13, -20.71) * mm, "mid": v(-26.24, -20.68) * mm, "end": v(-26.34, -20.65) * mm});
            skArc(sketch, "E564", {"start": v(-26.34, -20.65) * mm, "mid": v(-26.44, -20.62) * mm, "end": v(-26.54, -20.58) * mm});
            skArc(sketch, "E565", {"start": v(-26.54, -20.58) * mm, "mid": v(-26.61, -20.55) * mm, "end": v(-26.68, -20.51) * mm});
            skArc(sketch, "E566", {"start": v(-26.68, -20.51) * mm, "mid": v(-26.84, -20.42) * mm, "end": v(-26.98, -20.3) * mm});
            skArc(sketch, "E567", {"start": v(-26.98, -20.3) * mm, "mid": v(-27.13, -20.17) * mm, "end": v(-27.26, -20.02) * mm});
            skArc(sketch, "E568", {"start": v(-27.26, -20.02) * mm, "mid": v(-27.39, -19.87) * mm, "end": v(-27.5, -19.7) * mm});
            skArc(sketch, "E569", {"start": v(-27.5, -19.7) * mm, "mid": v(-27.59, -19.56) * mm, "end": v(-27.66, -19.4) * mm});
            skArc(sketch, "E570", {"start": v(-27.66, -19.4) * mm, "mid": v(-27.7, -19.3) * mm, "end": v(-27.73, -19.2) * mm});
            skArc(sketch, "E571", {"start": v(-27.73, -19.2) * mm, "mid": v(-27.74, -19.13) * mm, "end": v(-27.75, -19.06) * mm});
            skArc(sketch, "E572", {"start": v(-27.75, -19.06) * mm, "mid": v(-27.74, -19) * mm, "end": v(-27.73, -18.92) * mm});
            skArc(sketch, "E573", {"start": v(-27.73, -18.92) * mm, "mid": v(-27.68, -18.78) * mm, "end": v(-27.64, -18.64) * mm});
            skArc(sketch, "E574", {"start": v(-27.64, -18.64) * mm, "mid": v(-27.6, -18.54) * mm, "end": v(-27.57, -18.44) * mm});
            skArc(sketch, "E575", {"start": v(-27.57, -18.44) * mm, "mid": v(-27.52, -18.32) * mm, "end": v(-27.46, -18.2) * mm});
            skArc(sketch, "E576", {"start": v(-27.46, -18.2) * mm, "mid": v(-27.41, -18.08) * mm, "end": v(-27.36, -17.97) * mm});
            skArc(sketch, "E577", {"start": v(-27.36, -17.97) * mm, "mid": v(-27.3, -17.87) * mm, "end": v(-27.25, -17.78) * mm});
            skArc(sketch, "E578", {"start": v(-27.25, -17.78) * mm, "mid": v(-27.14, -17.58) * mm, "end": v(-27.03, -17.37) * mm});
            skArc(sketch, "E579", {"start": v(-27.03, -17.37) * mm, "mid": v(-26.99, -17.28) * mm, "end": v(-26.97, -17.17) * mm});
            skArc(sketch, "E580", {"start": v(-26.97, -17.17) * mm, "mid": v(-26.97, -17.1) * mm, "end": v(-27, -17.02) * mm});
            skArc(sketch, "E581", {"start": v(-27, -17.02) * mm, "mid": v(-27.06, -16.92) * mm, "end": v(-27.13, -16.82) * mm});
            skArc(sketch, "E582", {"start": v(-27.13, -16.82) * mm, "mid": v(-27.22, -16.7) * mm, "end": v(-27.31, -16.58) * mm});
            skArc(sketch, "E583", {"start": v(-27.31, -16.58) * mm, "mid": v(-27.37, -16.47) * mm, "end": v(-27.42, -16.35) * mm});
            skArc(sketch, "E584", {"start": v(-27.42, -16.35) * mm, "mid": v(-27.45, -16.22) * mm, "end": v(-27.47, -16.08) * mm});
            skArc(sketch, "E585", {"start": v(-27.47, -16.08) * mm, "mid": v(-27.48, -15.88) * mm, "end": v(-27.48, -15.68) * mm});
            skArc(sketch, "E586", {"start": v(-27.48, -15.68) * mm, "mid": v(-27.47, -15.38) * mm, "end": v(-27.43, -15.07) * mm});
            skArc(sketch, "E587", {"start": v(-27.43, -15.07) * mm, "mid": v(-27.36, -14.8) * mm, "end": v(-27.25, -14.55) * mm});
            skArc(sketch, "E588", {"start": v(-27.25, -14.55) * mm, "mid": v(-27.14, -14.35) * mm, "end": v(-26.99, -14.17) * mm});
            skArc(sketch, "E589", {"start": v(-26.99, -14.17) * mm, "mid": v(-26.83, -14.05) * mm, "end": v(-26.65, -13.97) * mm});
            skArc(sketch, "E590", {"start": v(-26.65, -13.97) * mm, "mid": v(-26.59, -13.95) * mm, "end": v(-26.52, -13.92) * mm});
            skArc(sketch, "E591", {"start": v(-26.52, -13.92) * mm, "mid": v(-26.43, -13.87) * mm, "end": v(-26.34, -13.81) * mm});
            skArc(sketch, "E592", {"start": v(-26.34, -13.81) * mm, "mid": v(-26.24, -13.74) * mm, "end": v(-26.14, -13.67) * mm});
            skArc(sketch, "E593", {"start": v(-26.14, -13.67) * mm, "mid": v(-26.04, -13.6) * mm, "end": v(-25.95, -13.52) * mm});
            skArc(sketch, "E594", {"start": v(-25.95, -13.52) * mm, "mid": v(-25.86, -13.44) * mm, "end": v(-25.76, -13.36) * mm});
            skArc(sketch, "E595", {"start": v(-25.76, -13.36) * mm, "mid": v(-25.66, -13.29) * mm, "end": v(-25.55, -13.21) * mm});
            skArc(sketch, "E596", {"start": v(-25.55, -13.21) * mm, "mid": v(-25.46, -13.14) * mm, "end": v(-25.36, -13.08) * mm});
            skArc(sketch, "E597", {"start": v(-25.36, -13.08) * mm, "mid": v(-25.3, -13.04) * mm, "end": v(-25.22, -13) * mm});
            skArc(sketch, "E598", {"start": v(-25.22, -13) * mm, "mid": v(-25.06, -12.93) * mm, "end": v(-24.9, -12.9) * mm});
            skArc(sketch, "E599", {"start": v(-24.9, -12.9) * mm, "mid": v(-24.69, -12.86) * mm, "end": v(-24.48, -12.85) * mm});
            skArc(sketch, "E600", {"start": v(-24.48, -12.85) * mm, "mid": v(-24.27, -12.86) * mm, "end": v(-24.07, -12.88) * mm});
            skArc(sketch, "E601", {"start": v(-24.07, -12.88) * mm, "mid": v(-23.9, -12.92) * mm, "end": v(-23.74, -12.98) * mm});
            skArc(sketch, "E602", {"start": v(-33.89, -13.23) * mm, "mid": v(-33.43, -13.32) * mm, "end": v(-32.97, -13.43) * mm});
            skArc(sketch, "E603", {"start": v(-32.97, -13.43) * mm, "mid": v(-32.68, -13.53) * mm, "end": v(-32.4, -13.66) * mm});
            skArc(sketch, "E604", {"start": v(-32.4, -13.66) * mm, "mid": v(-32.2, -13.8) * mm, "end": v(-32.02, -13.97) * mm});
            skArc(sketch, "E605", {"start": v(-32.02, -13.97) * mm, "mid": v(-31.85, -14.19) * mm, "end": v(-31.72, -14.43) * mm});
            skArc(sketch, "E606", {"start": v(-31.72, -14.43) * mm, "mid": v(-31.66, -14.54) * mm, "end": v(-31.61, -14.66) * mm});
            skArc(sketch, "E607", {"start": v(-31.61, -14.66) * mm, "mid": v(-31.59, -14.74) * mm, "end": v(-31.57, -14.82) * mm});
            skArc(sketch, "E608", {"start": v(-31.57, -14.82) * mm, "mid": v(-31.56, -14.9) * mm, "end": v(-31.56, -14.99) * mm});
            skArc(sketch, "E609", {"start": v(-31.56, -14.99) * mm, "mid": v(-31.56, -15.1) * mm, "end": v(-31.57, -15.23) * mm});
            skArc(sketch, "E610", {"start": v(-31.57, -15.23) * mm, "mid": v(-31.59, -15.4) * mm, "end": v(-31.58, -15.55) * mm});
            skArc(sketch, "E611", {"start": v(-31.58, -15.55) * mm, "mid": v(-31.56, -15.68) * mm, "end": v(-31.53, -15.8) * mm});
            skArc(sketch, "E612", {"start": v(-31.53, -15.8) * mm, "mid": v(-31.45, -15.97) * mm, "end": v(-31.37, -16.13) * mm});
            skArc(sketch, "E613", {"start": v(-31.37, -16.13) * mm, "mid": v(-31.17, -16.46) * mm, "end": v(-30.96, -16.8) * mm});
            skArc(sketch, "E614", {"start": v(-30.96, -16.8) * mm, "mid": v(-30.74, -17.18) * mm, "end": v(-30.53, -17.57) * mm});
            skArc(sketch, "E615", {"start": v(-30.53, -17.57) * mm, "mid": v(-30.35, -17.99) * mm, "end": v(-30.2, -18.41) * mm});
            skArc(sketch, "E616", {"start": v(-30.2, -18.41) * mm, "mid": v(-30.07, -18.8) * mm, "end": v(-29.98, -19.18) * mm});
            skArc(sketch, "E617", {"start": v(-29.98, -19.18) * mm, "mid": v(-29.95, -19.43) * mm, "end": v(-29.97, -19.68) * mm});
            skArc(sketch, "E618", {"start": v(-29.97, -19.68) * mm, "mid": v(-30, -19.82) * mm, "end": v(-30.06, -19.94) * mm});
            skArc(sketch, "E619", {"start": v(-30.06, -19.94) * mm, "mid": v(-30.15, -20.07) * mm, "end": v(-30.26, -20.2) * mm});
            skArc(sketch, "E620", {"start": v(-30.26, -20.2) * mm, "mid": v(-30.4, -20.32) * mm, "end": v(-30.54, -20.43) * mm});
            skArc(sketch, "E621", {"start": v(-30.54, -20.43) * mm, "mid": v(-30.72, -20.54) * mm, "end": v(-30.9, -20.64) * mm});
            skArc(sketch, "E622", {"start": v(-30.9, -20.64) * mm, "mid": v(-31.05, -20.7) * mm, "end": v(-31.2, -20.77) * mm});
            skArc(sketch, "E623", {"start": v(-31.2, -20.77) * mm, "mid": v(-31.31, -20.8) * mm, "end": v(-31.42, -20.83) * mm});
            skArc(sketch, "E624", {"start": v(-31.42, -20.83) * mm, "mid": v(-31.56, -20.85) * mm, "end": v(-31.7, -20.86) * mm});
            skArc(sketch, "E625", {"start": v(-31.7, -20.86) * mm, "mid": v(-31.96, -20.87) * mm, "end": v(-32.23, -20.88) * mm});
            skArc(sketch, "E626", {"start": v(-32.23, -20.88) * mm, "mid": v(-32.48, -20.88) * mm, "end": v(-32.73, -20.89) * mm});
            skArc(sketch, "E627", {"start": v(-32.73, -20.89) * mm, "mid": v(-32.87, -20.9) * mm, "end": v(-33.02, -20.91) * mm});
            skArc(sketch, "E628", {"start": v(-33.02, -20.91) * mm, "mid": v(-33.13, -20.94) * mm, "end": v(-33.24, -20.97) * mm});
            skArc(sketch, "E629", {"start": v(-33.24, -20.97) * mm, "mid": v(-33.37, -21.02) * mm, "end": v(-33.5, -21.07) * mm});
            skArc(sketch, "E630", {"start": v(-33.5, -21.07) * mm, "mid": v(-33.6, -21.1) * mm, "end": v(-33.68, -21.14) * mm});
            skArc(sketch, "E631", {"start": v(-33.68, -21.14) * mm, "mid": v(-33.8, -21.18) * mm, "end": v(-33.9, -21.22) * mm});
            skArc(sketch, "E632", {"start": v(-33.9, -21.22) * mm, "mid": v(-34, -21.25) * mm, "end": v(-34.1, -21.28) * mm});
            skArc(sketch, "E633", {"start": v(-34.1, -21.28) * mm, "mid": v(-34.2, -21.3) * mm, "end": v(-34.28, -21.32) * mm});
            skArc(sketch, "E634", {"start": v(-34.28, -21.32) * mm, "mid": v(-34.5, -21.36) * mm, "end": v(-34.73, -21.38) * mm});
            skArc(sketch, "E635", {"start": v(-34.73, -21.38) * mm, "mid": v(-34.98, -21.39) * mm, "end": v(-35.24, -21.39) * mm});
            skArc(sketch, "E636", {"start": v(-35.24, -21.39) * mm, "mid": v(-35.48, -21.38) * mm, "end": v(-35.71, -21.36) * mm});
            skArc(sketch, "E637", {"start": v(-35.71, -21.36) * mm, "mid": v(-35.86, -21.33) * mm, "end": v(-36, -21.28) * mm});
            skArc(sketch, "E638", {"start": v(-36, -21.28) * mm, "mid": v(-36.08, -21.26) * mm, "end": v(-36.16, -21.24) * mm});
            skArc(sketch, "E639", {"start": v(-36.16, -21.24) * mm, "mid": v(-36.32, -21.2) * mm, "end": v(-36.48, -21.18) * mm});
            skArc(sketch, "E640", {"start": v(-36.48, -21.18) * mm, "mid": v(-36.66, -21.15) * mm, "end": v(-36.85, -21.13) * mm});
            skArc(sketch, "E641", {"start": v(-36.85, -21.13) * mm, "mid": v(-37.05, -21.1) * mm, "end": v(-37.25, -21.08) * mm});
            skArc(sketch, "E642", {"start": v(-37.25, -21.08) * mm, "mid": v(-37.45, -21.06) * mm, "end": v(-37.64, -21.04) * mm});
            skArc(sketch, "E643", {"start": v(-37.64, -21.04) * mm, "mid": v(-37.83, -21.01) * mm, "end": v(-38.02, -20.98) * mm});
            skArc(sketch, "E644", {"start": v(-38.02, -20.98) * mm, "mid": v(-38.17, -20.96) * mm, "end": v(-38.33, -20.93) * mm});
            skArc(sketch, "E645", {"start": v(-38.33, -20.93) * mm, "mid": v(-38.41, -20.9) * mm, "end": v(-38.49, -20.88) * mm});
            skArc(sketch, "E646", {"start": v(-38.49, -20.88) * mm, "mid": v(-38.62, -20.81) * mm, "end": v(-38.74, -20.73) * mm});
            skArc(sketch, "E647", {"start": v(-38.74, -20.73) * mm, "mid": v(-38.88, -20.61) * mm, "end": v(-39.01, -20.49) * mm});
            skArc(sketch, "E648", {"start": v(-39.01, -20.49) * mm, "mid": v(-39.15, -20.34) * mm, "end": v(-39.27, -20.18) * mm});
            skArc(sketch, "E649", {"start": v(-39.27, -20.18) * mm, "mid": v(-39.38, -20.02) * mm, "end": v(-39.48, -19.85) * mm});
            skLineSegment(sketch, "E650", {"start": v(-39.48, -19.85) * mm, "end": v(-39.68, -19.49) * mm});
            skLineSegment(sketch, "E651", {"start": v(-39.68, -19.49) * mm, "end": v(-39.56, -19.16) * mm});
            skArc(sketch, "E652", {"start": v(-39.56, -19.16) * mm, "mid": v(-39.52, -19.07) * mm, "end": v(-39.47, -18.97) * mm});
            skArc(sketch, "E653", {"start": v(-39.47, -18.97) * mm, "mid": v(-39.39, -18.78) * mm, "end": v(-39.3, -18.58) * mm});
            skArc(sketch, "E654", {"start": v(-39.3, -18.58) * mm, "mid": v(-39.19, -18.35) * mm, "end": v(-39.08, -18.13) * mm});
            skArc(sketch, "E655", {"start": v(-39.08, -18.13) * mm, "mid": v(-38.96, -17.89) * mm, "end": v(-38.85, -17.65) * mm});
            skArc(sketch, "E656", {"start": v(-38.85, -17.65) * mm, "mid": v(-38.73, -17.4) * mm, "end": v(-38.61, -17.16) * mm});
            skArc(sketch, "E657", {"start": v(-38.61, -17.16) * mm, "mid": v(-38.5, -16.92) * mm, "end": v(-38.4, -16.67) * mm});
            skArc(sketch, "E658", {"start": v(-38.4, -16.67) * mm, "mid": v(-38.3, -16.46) * mm, "end": v(-38.21, -16.25) * mm});
            skArc(sketch, "E659", {"start": v(-38.21, -16.25) * mm, "mid": v(-38.16, -16.13) * mm, "end": v(-38.12, -16) * mm});
            skArc(sketch, "E660", {"start": v(-38.12, -16) * mm, "mid": v(-38.08, -15.87) * mm, "end": v(-38.04, -15.73) * mm});
            skArc(sketch, "E661", {"start": v(-38.04, -15.73) * mm, "mid": v(-38.03, -15.65) * mm, "end": v(-38.02, -15.57) * mm});
            skArc(sketch, "E662", {"start": v(-38.02, -15.57) * mm, "mid": v(-38.02, -15.5) * mm, "end": v(-38.03, -15.43) * mm});
            skArc(sketch, "E663", {"start": v(-38.03, -15.43) * mm, "mid": v(-38.06, -15.32) * mm, "end": v(-38.1, -15.21) * mm});
            skArc(sketch, "E664", {"start": v(-38.1, -15.21) * mm, "mid": v(-38.16, -14.91) * mm, "end": v(-38.16, -14.6) * mm});
            skArc(sketch, "E665", {"start": v(-38.16, -14.6) * mm, "mid": v(-38.09, -14.28) * mm, "end": v(-37.97, -13.97) * mm});
            skArc(sketch, "E666", {"start": v(-37.97, -13.97) * mm, "mid": v(-37.8, -13.68) * mm, "end": v(-37.58, -13.43) * mm});
            skArc(sketch, "E667", {"start": v(-37.58, -13.43) * mm, "mid": v(-37.35, -13.25) * mm, "end": v(-37.08, -13.12) * mm});
            skArc(sketch, "E668", {"start": v(-37.08, -13.12) * mm, "mid": v(-36.9, -13.08) * mm, "end": v(-36.73, -13.07) * mm});
            skArc(sketch, "E669", {"start": v(-36.73, -13.07) * mm, "mid": v(-36.19, -13.08) * mm, "end": v(-35.65, -13.1) * mm});
            skArc(sketch, "E670", {"start": v(-35.65, -13.1) * mm, "mid": v(-35.1, -13.12) * mm, "end": v(-34.57, -13.15) * mm});
            skArc(sketch, "E671", {"start": v(-34.57, -13.15) * mm, "mid": v(-34.23, -13.18) * mm, "end": v(-33.89, -13.23) * mm});
            skArc(sketch, "E672", {"start": v(11.01, -13.24) * mm, "mid": v(11.17, -13.35) * mm, "end": v(11.3, -13.49) * mm});
            skArc(sketch, "E673", {"start": v(11.3, -13.49) * mm, "mid": v(11.4, -13.65) * mm, "end": v(11.48, -13.82) * mm});
            skArc(sketch, "E674", {"start": v(11.48, -13.82) * mm, "mid": v(11.54, -14.09) * mm, "end": v(11.58, -14.35) * mm});
            skArc(sketch, "E675", {"start": v(11.58, -14.35) * mm, "mid": v(11.62, -14.81) * mm, "end": v(11.65, -15.28) * mm});
            skArc(sketch, "E676", {"start": v(11.65, -15.28) * mm, "mid": v(11.67, -15.73) * mm, "end": v(11.7, -16.2) * mm});
            skArc(sketch, "E677", {"start": v(11.7, -16.2) * mm, "mid": v(11.72, -16.42) * mm, "end": v(11.74, -16.66) * mm});
            skArc(sketch, "E678", {"start": v(11.74, -16.66) * mm, "mid": v(11.77, -16.79) * mm, "end": v(11.8, -16.92) * mm});
            skArc(sketch, "E679", {"start": v(11.8, -16.92) * mm, "mid": v(11.82, -16.96) * mm, "end": v(11.87, -16.98) * mm});
            skArc(sketch, "E680", {"start": v(11.87, -16.98) * mm, "mid": v(11.92, -16.97) * mm, "end": v(11.97, -16.95) * mm});
            skArc(sketch, "E681", {"start": v(11.97, -16.95) * mm, "mid": v(12.08, -16.87) * mm, "end": v(12.2, -16.8) * mm});
            skArc(sketch, "E682", {"start": v(12.2, -16.8) * mm, "mid": v(12.36, -16.67) * mm, "end": v(12.52, -16.54) * mm});
            skArc(sketch, "E683", {"start": v(12.52, -16.54) * mm, "mid": v(12.78, -16.33) * mm, "end": v(13.04, -16.12) * mm});
            skArc(sketch, "E684", {"start": v(13.04, -16.12) * mm, "mid": v(13.41, -15.82) * mm, "end": v(13.8, -15.54) * mm});
            skArc(sketch, "E685", {"start": v(13.8, -15.54) * mm, "mid": v(14.1, -15.38) * mm, "end": v(14.4, -15.25) * mm});
            skArc(sketch, "E686", {"start": v(14.4, -15.25) * mm, "mid": v(14.66, -15.2) * mm, "end": v(14.93, -15.19) * mm});
            skArc(sketch, "E687", {"start": v(14.93, -15.19) * mm, "mid": v(15.2, -15.23) * mm, "end": v(15.46, -15.33) * mm});
            skArc(sketch, "E688", {"start": v(15.46, -15.33) * mm, "mid": v(15.7, -15.45) * mm, "end": v(15.94, -15.6) * mm});
            skArc(sketch, "E689", {"start": v(15.94, -15.6) * mm, "mid": v(16.12, -15.76) * mm, "end": v(16.28, -15.94) * mm});
            skArc(sketch, "E690", {"start": v(16.28, -15.94) * mm, "mid": v(16.4, -16.12) * mm, "end": v(16.48, -16.33) * mm});
            skArc(sketch, "E691", {"start": v(16.48, -16.33) * mm, "mid": v(16.53, -16.55) * mm, "end": v(16.55, -16.77) * mm});
            skArc(sketch, "E692", {"start": v(16.55, -16.77) * mm, "mid": v(16.54, -16.93) * mm, "end": v(16.5, -17.1) * mm});
            skArc(sketch, "E693", {"start": v(16.5, -17.1) * mm, "mid": v(16.46, -17.25) * mm, "end": v(16.4, -17.4) * mm});
            skArc(sketch, "E694", {"start": v(16.4, -17.4) * mm, "mid": v(16.3, -17.59) * mm, "end": v(16.2, -17.75) * mm});
            skArc(sketch, "E695", {"start": v(16.2, -17.75) * mm, "mid": v(16.03, -17.98) * mm, "end": v(15.86, -18.2) * mm});
            skArc(sketch, "E696", {"start": v(15.86, -18.2) * mm, "mid": v(15.37, -18.74) * mm, "end": v(14.83, -19.24) * mm});
            skArc(sketch, "E697", {"start": v(14.83, -19.24) * mm, "mid": v(14.19, -19.72) * mm, "end": v(13.52, -20.16) * mm});
            skArc(sketch, "E698", {"start": v(13.52, -20.16) * mm, "mid": v(12.81, -20.55) * mm, "end": v(12.08, -20.88) * mm});
            skArc(sketch, "E699", {"start": v(12.08, -20.88) * mm, "mid": v(11.39, -21.12) * mm, "end": v(10.68, -21.3) * mm});
            skArc(sketch, "E700", {"start": v(10.68, -21.3) * mm, "mid": v(10.34, -21.35) * mm, "end": v(10, -21.39) * mm});
            skArc(sketch, "E701", {"start": v(10, -21.39) * mm, "mid": v(9.75, -21.4) * mm, "end": v(9.5, -21.36) * mm});
            skArc(sketch, "E702", {"start": v(9.5, -21.36) * mm, "mid": v(9.3, -21.3) * mm, "end": v(9.12, -21.21) * mm});
            skArc(sketch, "E703", {"start": v(9.12, -21.21) * mm, "mid": v(8.93, -21.08) * mm, "end": v(8.76, -20.93) * mm});
            skArc(sketch, "E704", {"start": v(8.76, -20.93) * mm, "mid": v(8.6, -20.73) * mm, "end": v(8.46, -20.52) * mm});
            skArc(sketch, "E705", {"start": v(8.46, -20.52) * mm, "mid": v(8.37, -20.32) * mm, "end": v(8.31, -20.1) * mm});
            skArc(sketch, "E706", {"start": v(8.31, -20.1) * mm, "mid": v(8.27, -19.77) * mm, "end": v(8.25, -19.44) * mm});
            skArc(sketch, "E707", {"start": v(8.25, -19.44) * mm, "mid": v(8.24, -18.5) * mm, "end": v(8.23, -17.58) * mm});
            skArc(sketch, "E708", {"start": v(8.23, -17.58) * mm, "mid": v(8.23, -16.18) * mm, "end": v(8.25, -14.77) * mm});
            skArc(sketch, "E709", {"start": v(8.25, -14.77) * mm, "mid": v(8.3, -14.23) * mm, "end": v(8.46, -13.7) * mm});
            skArc(sketch, "E710", {"start": v(8.46, -13.7) * mm, "mid": v(8.66, -13.4) * mm, "end": v(8.98, -13.22) * mm});
            skArc(sketch, "E711", {"start": v(8.98, -13.22) * mm, "mid": v(9.48, -13.1) * mm, "end": v(10, -13.08) * mm});
            skArc(sketch, "E712", {"start": v(10, -13.08) * mm, "mid": v(10.2, -13.08) * mm, "end": v(10.4, -13.1) * mm});
            skArc(sketch, "E713", {"start": v(10.4, -13.1) * mm, "mid": v(10.54, -13.1) * mm, "end": v(10.67, -13.12) * mm});
            skArc(sketch, "E714", {"start": v(10.67, -13.12) * mm, "mid": v(10.76, -13.14) * mm, "end": v(10.85, -13.17) * mm});
            skArc(sketch, "E715", {"start": v(10.85, -13.17) * mm, "mid": v(10.93, -13.2) * mm, "end": v(11.01, -13.24) * mm});
            skArc(sketch, "E716", {"start": v(21.68, -13.2) * mm, "mid": v(22.1, -13.36) * mm, "end": v(22.52, -13.53) * mm});
            skArc(sketch, "E717", {"start": v(22.52, -13.53) * mm, "mid": v(22.99, -13.76) * mm, "end": v(23.45, -14) * mm});
            skArc(sketch, "E718", {"start": v(23.45, -14) * mm, "mid": v(23.88, -14.25) * mm, "end": v(24.3, -14.5) * mm});
            skArc(sketch, "E719", {"start": v(24.3, -14.5) * mm, "mid": v(24.54, -14.67) * mm, "end": v(24.77, -14.88) * mm});
            skArc(sketch, "E720", {"start": v(24.77, -14.88) * mm, "mid": v(24.87, -14.98) * mm, "end": v(24.98, -15.07) * mm});
            skArc(sketch, "E721", {"start": v(24.98, -15.07) * mm, "mid": v(25.07, -15.12) * mm, "end": v(25.17, -15.14) * mm});
            skArc(sketch, "E722", {"start": v(25.17, -15.14) * mm, "mid": v(25.28, -15.15) * mm, "end": v(25.4, -15.14) * mm});
            skArc(sketch, "E723", {"start": v(25.4, -15.14) * mm, "mid": v(25.6, -15.1) * mm, "end": v(25.8, -15.05) * mm});
            skArc(sketch, "E724", {"start": v(25.8, -15.05) * mm, "mid": v(25.96, -15.02) * mm, "end": v(26.13, -15) * mm});
            skArc(sketch, "E725", {"start": v(26.13, -15) * mm, "mid": v(26.3, -15) * mm, "end": v(26.46, -15) * mm});
            skArc(sketch, "E726", {"start": v(26.46, -15) * mm, "mid": v(26.62, -15.02) * mm, "end": v(26.78, -15.06) * mm});
            skArc(sketch, "E727", {"start": v(26.78, -15.06) * mm, "mid": v(26.93, -15.1) * mm, "end": v(27.07, -15.17) * mm});
            skArc(sketch, "E728", {"start": v(27.07, -15.17) * mm, "mid": v(27.2, -15.25) * mm, "end": v(27.33, -15.34) * mm});
            skArc(sketch, "E729", {"start": v(27.33, -15.34) * mm, "mid": v(27.47, -15.45) * mm, "end": v(27.6, -15.57) * mm});
            skArc(sketch, "E730", {"start": v(27.6, -15.57) * mm, "mid": v(27.71, -15.7) * mm, "end": v(27.82, -15.83) * mm});
            skArc(sketch, "E731", {"start": v(27.82, -15.83) * mm, "mid": v(27.9, -15.95) * mm, "end": v(27.98, -16.08) * mm});
            skArc(sketch, "E732", {"start": v(27.98, -16.08) * mm, "mid": v(28.1, -16.37) * mm, "end": v(28.15, -16.67) * mm});
            skArc(sketch, "E733", {"start": v(28.15, -16.67) * mm, "mid": v(28.14, -16.97) * mm, "end": v(28.08, -17.25) * mm});
            skArc(sketch, "E734", {"start": v(28.08, -17.25) * mm, "mid": v(27.93, -17.58) * mm, "end": v(27.73, -17.89) * mm});
            skArc(sketch, "E735", {"start": v(27.73, -17.89) * mm, "mid": v(27.41, -18.28) * mm, "end": v(27.07, -18.66) * mm});
            skArc(sketch, "E736", {"start": v(27.07, -18.66) * mm, "mid": v(26.6, -19.12) * mm, "end": v(26.1, -19.55) * mm});
            skArc(sketch, "E737", {"start": v(26.1, -19.55) * mm, "mid": v(25.62, -19.91) * mm, "end": v(25.1, -20.24) * mm});
            skArc(sketch, "E738", {"start": v(25.1, -20.24) * mm, "mid": v(24.57, -20.52) * mm, "end": v(24.01, -20.76) * mm});
            skArc(sketch, "E739", {"start": v(24.01, -20.76) * mm, "mid": v(23.4, -20.97) * mm, "end": v(22.77, -21.14) * mm});
            skArc(sketch, "E740", {"start": v(22.77, -21.14) * mm, "mid": v(22.32, -21.24) * mm, "end": v(21.87, -21.32) * mm});
            skArc(sketch, "E741", {"start": v(21.87, -21.32) * mm, "mid": v(21.48, -21.36) * mm, "end": v(21.1, -21.38) * mm});
            skArc(sketch, "E742", {"start": v(21.1, -21.38) * mm, "mid": v(20.77, -21.37) * mm, "end": v(20.46, -21.33) * mm});
            skArc(sketch, "E743", {"start": v(20.46, -21.33) * mm, "mid": v(20.24, -21.26) * mm, "end": v(20.03, -21.16) * mm});
            skArc(sketch, "E744", {"start": v(20.03, -21.16) * mm, "mid": v(19.9, -21.05) * mm, "end": v(19.8, -20.93) * mm});
            skArc(sketch, "E745", {"start": v(19.8, -20.93) * mm, "mid": v(19.7, -20.76) * mm, "end": v(19.63, -20.58) * mm});
            skArc(sketch, "E746", {"start": v(19.63, -20.58) * mm, "mid": v(19.56, -20.36) * mm, "end": v(19.5, -20.15) * mm});
            skArc(sketch, "E747", {"start": v(19.5, -20.15) * mm, "mid": v(19.48, -19.91) * mm, "end": v(19.46, -19.68) * mm});
            skArc(sketch, "E748", {"start": v(19.46, -19.68) * mm, "mid": v(19.47, -19.48) * mm, "end": v(19.48, -19.28) * mm});
            skArc(sketch, "E749", {"start": v(19.48, -19.28) * mm, "mid": v(19.5, -19.12) * mm, "end": v(19.54, -18.96) * mm});
            skArc(sketch, "E750", {"start": v(19.54, -18.96) * mm, "mid": v(19.6, -18.83) * mm, "end": v(19.65, -18.7) * mm});
            skArc(sketch, "E751", {"start": v(19.65, -18.7) * mm, "mid": v(19.73, -18.6) * mm, "end": v(19.82, -18.5) * mm});
            skArc(sketch, "E752", {"start": v(19.82, -18.5) * mm, "mid": v(19.94, -18.4) * mm, "end": v(20.07, -18.32) * mm});
            skArc(sketch, "E753", {"start": v(20.07, -18.32) * mm, "mid": v(20.23, -18.24) * mm, "end": v(20.4, -18.17) * mm});
            skArc(sketch, "E754", {"start": v(20.4, -18.17) * mm, "mid": v(20.63, -18.1) * mm, "end": v(20.87, -18.03) * mm});
            skArc(sketch, "E755", {"start": v(20.87, -18.03) * mm, "mid": v(21.26, -17.94) * mm, "end": v(21.65, -17.86) * mm});
            skLineSegment(sketch, "E756", {"start": v(21.65, -17.86) * mm, "end": v(22.73, -17.64) * mm});
            skLineSegment(sketch, "E757", {"start": v(22.73, -17.64) * mm, "end": v(21.76, -17.13) * mm});
            skArc(sketch, "E758", {"start": v(21.76, -17.13) * mm, "mid": v(21.18, -16.81) * mm, "end": v(20.6, -16.48) * mm});
            skArc(sketch, "E759", {"start": v(20.6, -16.48) * mm, "mid": v(20.25, -16.24) * mm, "end": v(19.92, -15.97) * mm});
            skArc(sketch, "E760", {"start": v(19.92, -15.97) * mm, "mid": v(19.71, -15.75) * mm, "end": v(19.54, -15.5) * mm});
            skArc(sketch, "E761", {"start": v(19.54, -15.5) * mm, "mid": v(19.45, -15.25) * mm, "end": v(19.42, -14.99) * mm});
            skArc(sketch, "E762", {"start": v(19.42, -14.99) * mm, "mid": v(19.45, -14.7) * mm, "end": v(19.56, -14.43) * mm});
            skArc(sketch, "E763", {"start": v(19.56, -14.43) * mm, "mid": v(19.77, -14.09) * mm, "end": v(20.02, -13.77) * mm});
            skArc(sketch, "E764", {"start": v(20.02, -13.77) * mm, "mid": v(20.29, -13.48) * mm, "end": v(20.58, -13.23) * mm});
            skArc(sketch, "E765", {"start": v(20.58, -13.23) * mm, "mid": v(20.8, -13.1) * mm, "end": v(21.06, -13.06) * mm});
            skArc(sketch, "E766", {"start": v(21.06, -13.06) * mm, "mid": v(21.12, -13.06) * mm, "end": v(21.17, -13.07) * mm});
            skArc(sketch, "E767", {"start": v(21.17, -13.07) * mm, "mid": v(21.25, -13.08) * mm, "end": v(21.34, -13.1) * mm});
            skArc(sketch, "E768", {"start": v(21.34, -13.1) * mm, "mid": v(21.43, -13.12) * mm, "end": v(21.51, -13.15) * mm});
            skArc(sketch, "E769", {"start": v(21.51, -13.15) * mm, "mid": v(21.6, -13.17) * mm, "end": v(21.68, -13.2) * mm});
            skArc(sketch, "E770", {"start": v(2.9, -13.34) * mm, "mid": v(3.16, -13.38) * mm, "end": v(3.42, -13.43) * mm});
            skArc(sketch, "E771", {"start": v(3.42, -13.43) * mm, "mid": v(3.63, -13.48) * mm, "end": v(3.83, -13.55) * mm});
            skArc(sketch, "E772", {"start": v(3.83, -13.55) * mm, "mid": v(3.98, -13.63) * mm, "end": v(4.12, -13.72) * mm});
            skArc(sketch, "E773", {"start": v(4.12, -13.72) * mm, "mid": v(4.22, -13.82) * mm, "end": v(4.3, -13.94) * mm});
            skArc(sketch, "E774", {"start": v(4.3, -13.94) * mm, "mid": v(4.36, -14.1) * mm, "end": v(4.39, -14.3) * mm});
            skArc(sketch, "E775", {"start": v(4.39, -14.3) * mm, "mid": v(4.4, -14.67) * mm, "end": v(4.4, -15.04) * mm});
            skArc(sketch, "E776", {"start": v(4.4, -15.04) * mm, "mid": v(4.4, -15.44) * mm, "end": v(4.37, -15.83) * mm});
            skArc(sketch, "E777", {"start": v(4.37, -15.83) * mm, "mid": v(4.33, -16.15) * mm, "end": v(4.27, -16.46) * mm});
            skArc(sketch, "E778", {"start": v(4.27, -16.46) * mm, "mid": v(4.15, -16.9) * mm, "end": v(4, -17.35) * mm});
            skArc(sketch, "E779", {"start": v(4, -17.35) * mm, "mid": v(3.84, -17.76) * mm, "end": v(3.65, -18.16) * mm});
            skArc(sketch, "E780", {"start": v(3.65, -18.16) * mm, "mid": v(3.44, -18.53) * mm, "end": v(3.2, -18.89) * mm});
            skArc(sketch, "E781", {"start": v(3.2, -18.89) * mm, "mid": v(2.95, -19.23) * mm, "end": v(2.67, -19.55) * mm});
            skArc(sketch, "E782", {"start": v(2.67, -19.55) * mm, "mid": v(2.28, -19.92) * mm, "end": v(1.86, -20.26) * mm});
            skArc(sketch, "E783", {"start": v(1.86, -20.26) * mm, "mid": v(1.43, -20.54) * mm, "end": v(0.97, -20.79) * mm});
            skArc(sketch, "E784", {"start": v(0.97, -20.79) * mm, "mid": v(0.43, -21.01) * mm, "end": v(-0.13, -21.2) * mm});
            skArc(sketch, "E785", {"start": v(-0.13, -21.2) * mm, "mid": v(-0.84, -21.38) * mm, "end": v(-1.56, -21.53) * mm});
            skArc(sketch, "E786", {"start": v(-1.56, -21.53) * mm, "mid": v(-1.8, -21.57) * mm, "end": v(-2.02, -21.61) * mm});
            skArc(sketch, "E787", {"start": v(-2.02, -21.61) * mm, "mid": v(-2.14, -21.63) * mm, "end": v(-2.25, -21.64) * mm});
            skArc(sketch, "E788", {"start": v(-2.25, -21.64) * mm, "mid": v(-2.33, -21.64) * mm, "end": v(-2.4, -21.63) * mm});
            skArc(sketch, "E789", {"start": v(-2.4, -21.63) * mm, "mid": v(-2.48, -21.6) * mm, "end": v(-2.55, -21.58) * mm});
            skArc(sketch, "E790", {"start": v(-2.55, -21.58) * mm, "mid": v(-2.82, -21.4) * mm, "end": v(-3.05, -21.17) * mm});
            skArc(sketch, "E791", {"start": v(-3.05, -21.17) * mm, "mid": v(-3.26, -20.86) * mm, "end": v(-3.44, -20.53) * mm});
            skArc(sketch, "E792", {"start": v(-3.44, -20.53) * mm, "mid": v(-3.57, -20.17) * mm, "end": v(-3.65, -19.8) * mm});
            skArc(sketch, "E793", {"start": v(-3.65, -19.8) * mm, "mid": v(-3.67, -19.48) * mm, "end": v(-3.62, -19.16) * mm});
            skArc(sketch, "E794", {"start": v(-3.62, -19.16) * mm, "mid": v(-3.57, -19.03) * mm, "end": v(-3.51, -18.9) * mm});
            skArc(sketch, "E795", {"start": v(-3.51, -18.9) * mm, "mid": v(-3.43, -18.77) * mm, "end": v(-3.34, -18.65) * mm});
            skArc(sketch, "E796", {"start": v(-3.34, -18.65) * mm, "mid": v(-3.23, -18.53) * mm, "end": v(-3.11, -18.43) * mm});
            skArc(sketch, "E797", {"start": v(-3.11, -18.43) * mm, "mid": v(-3, -18.34) * mm, "end": v(-2.87, -18.27) * mm});
            skArc(sketch, "E798", {"start": v(-2.87, -18.27) * mm, "mid": v(-2.8, -18.24) * mm, "end": v(-2.73, -18.22) * mm});
            skArc(sketch, "E799", {"start": v(-2.73, -18.22) * mm, "mid": v(-2.6, -18.18) * mm, "end": v(-2.5, -18.14) * mm});
            skArc(sketch, "E800", {"start": v(-2.5, -18.14) * mm, "mid": v(-2.36, -18.1) * mm, "end": v(-2.22, -18.06) * mm});
            skArc(sketch, "E801", {"start": v(-2.22, -18.06) * mm, "mid": v(-2.09, -18.02) * mm, "end": v(-1.95, -17.99) * mm});
            skArc(sketch, "E802", {"start": v(-1.95, -17.99) * mm, "mid": v(-1.66, -17.9) * mm, "end": v(-1.37, -17.8) * mm});
            skArc(sketch, "E803", {"start": v(-1.37, -17.8) * mm, "mid": v(-0.93, -17.63) * mm, "end": v(-0.49, -17.44) * mm});
            skArc(sketch, "E804", {"start": v(-0.49, -17.44) * mm, "mid": v(-0.02, -17.23) * mm, "end": v(0.44, -17.02) * mm});
            skArc(sketch, "E805", {"start": v(0.44, -17.02) * mm, "mid": v(0.5, -16.98) * mm, "end": v(0.52, -16.91) * mm});
            skArc(sketch, "E806", {"start": v(0.52, -16.91) * mm, "mid": v(0.51, -16.9) * mm, "end": v(0.5, -16.9) * mm});
            skArc(sketch, "E807", {"start": v(0.5, -16.9) * mm, "mid": v(0.32, -16.87) * mm, "end": v(0.15, -16.86) * mm});
            skArc(sketch, "E808", {"start": v(0.15, -16.86) * mm, "mid": v(-0.05, -16.84) * mm, "end": v(-0.25, -16.82) * mm});
            skArc(sketch, "E809", {"start": v(-0.25, -16.82) * mm, "mid": v(-0.49, -16.8) * mm, "end": v(-0.73, -16.78) * mm});
            skArc(sketch, "E810", {"start": v(-0.73, -16.78) * mm, "mid": v(-1.55, -16.71) * mm, "end": v(-2.37, -16.62) * mm});
            skArc(sketch, "E811", {"start": v(-2.37, -16.62) * mm, "mid": v(-2.8, -16.52) * mm, "end": v(-3.2, -16.34) * mm});
            skArc(sketch, "E812", {"start": v(-3.2, -16.34) * mm, "mid": v(-3.46, -16.14) * mm, "end": v(-3.63, -15.86) * mm});
            skArc(sketch, "E813", {"start": v(-3.63, -15.86) * mm, "mid": v(-3.75, -15.46) * mm, "end": v(-3.81, -15.06) * mm});
            skArc(sketch, "E814", {"start": v(-3.81, -15.06) * mm, "mid": v(-3.81, -14.66) * mm, "end": v(-3.78, -14.26) * mm});
            skArc(sketch, "E815", {"start": v(-3.78, -14.26) * mm, "mid": v(-3.7, -14) * mm, "end": v(-3.55, -13.78) * mm});
            skArc(sketch, "E816", {"start": v(-3.55, -13.78) * mm, "mid": v(-3.33, -13.6) * mm, "end": v(-3.07, -13.5) * mm});
            skArc(sketch, "E817", {"start": v(-3.07, -13.5) * mm, "mid": v(-2.65, -13.4) * mm, "end": v(-2.21, -13.34) * mm});
            skArc(sketch, "E818", {"start": v(-2.21, -13.34) * mm, "mid": v(-1.79, -13.3) * mm, "end": v(-1.35, -13.3) * mm});
            skArc(sketch, "E819", {"start": v(-1.35, -13.3) * mm, "mid": v(-0.5, -13.29) * mm, "end": v(0.36, -13.28) * mm});
            skArc(sketch, "E820", {"start": v(0.36, -13.28) * mm, "mid": v(1.22, -13.29) * mm, "end": v(2.07, -13.3) * mm});
            skArc(sketch, "E821", {"start": v(2.07, -13.3) * mm, "mid": v(2.48, -13.3) * mm, "end": v(2.9, -13.34) * mm});
            skArc(sketch, "E822", {"start": v(-12.85, -13.72) * mm, "mid": v(-12.7, -13.81) * mm, "end": v(-12.55, -13.93) * mm});
            skArc(sketch, "E823", {"start": v(-12.55, -13.93) * mm, "mid": v(-12.44, -14.06) * mm, "end": v(-12.35, -14.2) * mm});
            skArc(sketch, "E824", {"start": v(-12.35, -14.2) * mm, "mid": v(-12.28, -14.4) * mm, "end": v(-12.23, -14.62) * mm});
            skArc(sketch, "E825", {"start": v(-12.23, -14.62) * mm, "mid": v(-12.18, -14.93) * mm, "end": v(-12.15, -15.24) * mm});
            skArc(sketch, "E826", {"start": v(-12.15, -15.24) * mm, "mid": v(-12.12, -15.52) * mm, "end": v(-12.1, -15.8) * mm});
            skArc(sketch, "E827", {"start": v(-12.1, -15.8) * mm, "mid": v(-12.07, -15.94) * mm, "end": v(-12.03, -16.08) * mm});
            skArc(sketch, "E828", {"start": v(-12.03, -16.08) * mm, "mid": v(-11.98, -16.16) * mm, "end": v(-11.92, -16.23) * mm});
            skArc(sketch, "E829", {"start": v(-11.92, -16.23) * mm, "mid": v(-11.85, -16.27) * mm, "end": v(-11.77, -16.28) * mm});
            skArc(sketch, "E830", {"start": v(-11.77, -16.28) * mm, "mid": v(-11.7, -16.27) * mm, "end": v(-11.64, -16.24) * mm});
            skArc(sketch, "E831", {"start": v(-11.64, -16.24) * mm, "mid": v(-11.6, -16.2) * mm, "end": v(-11.57, -16.13) * mm});
            skArc(sketch, "E832", {"start": v(-11.57, -16.13) * mm, "mid": v(-11.55, -16.02) * mm, "end": v(-11.55, -15.91) * mm});
            skArc(sketch, "E833", {"start": v(-11.55, -15.91) * mm, "mid": v(-11.56, -15.68) * mm, "end": v(-11.57, -15.45) * mm});
            skArc(sketch, "E834", {"start": v(-11.57, -15.45) * mm, "mid": v(-11.58, -15.22) * mm, "end": v(-11.58, -14.98) * mm});
            skArc(sketch, "E835", {"start": v(-11.58, -14.98) * mm, "mid": v(-11.56, -14.82) * mm, "end": v(-11.52, -14.68) * mm});
            skArc(sketch, "E836", {"start": v(-11.52, -14.68) * mm, "mid": v(-11.46, -14.54) * mm, "end": v(-11.37, -14.42) * mm});
            skArc(sketch, "E837", {"start": v(-11.37, -14.42) * mm, "mid": v(-11.22, -14.27) * mm, "end": v(-11.06, -14.12) * mm});
            skArc(sketch, "E838", {"start": v(-11.06, -14.12) * mm, "mid": v(-10.9, -14) * mm, "end": v(-10.74, -13.88) * mm});
            skArc(sketch, "E839", {"start": v(-10.74, -13.88) * mm, "mid": v(-10.56, -13.79) * mm, "end": v(-10.37, -13.7) * mm});
            skArc(sketch, "E840", {"start": v(-10.37, -13.7) * mm, "mid": v(-10.18, -13.64) * mm, "end": v(-9.98, -13.59) * mm});
            skArc(sketch, "E841", {"start": v(-9.98, -13.59) * mm, "mid": v(-9.79, -13.56) * mm, "end": v(-9.6, -13.55) * mm});
            skArc(sketch, "E842", {"start": v(-9.6, -13.55) * mm, "mid": v(-9.48, -13.55) * mm, "end": v(-9.36, -13.56) * mm});
            skArc(sketch, "E843", {"start": v(-9.36, -13.56) * mm, "mid": v(-9.29, -13.57) * mm, "end": v(-9.22, -13.6) * mm});
            skArc(sketch, "E844", {"start": v(-9.22, -13.6) * mm, "mid": v(-9.14, -13.64) * mm, "end": v(-9.08, -13.68) * mm});
            skArc(sketch, "E845", {"start": v(-9.08, -13.68) * mm, "mid": v(-8.97, -13.78) * mm, "end": v(-8.87, -13.87) * mm});
            skArc(sketch, "E846", {"start": v(-8.87, -13.87) * mm, "mid": v(-8.6, -14.14) * mm, "end": v(-8.37, -14.44) * mm});
            skArc(sketch, "E847", {"start": v(-8.37, -14.44) * mm, "mid": v(-8.1, -14.83) * mm, "end": v(-7.85, -15.24) * mm});
            skArc(sketch, "E848", {"start": v(-7.85, -15.24) * mm, "mid": v(-7.62, -15.66) * mm, "end": v(-7.41, -16.1) * mm});
            skArc(sketch, "E849", {"start": v(-7.41, -16.1) * mm, "mid": v(-7.27, -16.46) * mm, "end": v(-7.15, -16.84) * mm});
            skArc(sketch, "E850", {"start": v(-7.15, -16.84) * mm, "mid": v(-7.13, -16.95) * mm, "end": v(-7.1, -17.06) * mm});
            skArc(sketch, "E851", {"start": v(-7.1, -17.06) * mm, "mid": v(-7.08, -17.22) * mm, "end": v(-7.05, -17.37) * mm});
            skArc(sketch, "E852", {"start": v(-7.05, -17.37) * mm, "mid": v(-7.02, -17.53) * mm, "end": v(-7, -17.7) * mm});
            skArc(sketch, "E853", {"start": v(-7, -17.7) * mm, "mid": v(-6.98, -17.85) * mm, "end": v(-6.96, -18) * mm});
            skArc(sketch, "E854", {"start": v(-6.96, -18) * mm, "mid": v(-6.94, -18.2) * mm, "end": v(-6.92, -18.4) * mm});
            skArc(sketch, "E855", {"start": v(-6.92, -18.4) * mm, "mid": v(-6.91, -18.54) * mm, "end": v(-6.91, -18.67) * mm});
            skArc(sketch, "E856", {"start": v(-6.91, -18.67) * mm, "mid": v(-6.92, -18.79) * mm, "end": v(-6.94, -18.9) * mm});
            skArc(sketch, "E857", {"start": v(-6.94, -18.9) * mm, "mid": v(-6.97, -19.05) * mm, "end": v(-7, -19.2) * mm});
            skArc(sketch, "E858", {"start": v(-7, -19.2) * mm, "mid": v(-7.05, -19.38) * mm, "end": v(-7.12, -19.56) * mm});
            skArc(sketch, "E859", {"start": v(-7.12, -19.56) * mm, "mid": v(-7.2, -19.72) * mm, "end": v(-7.28, -19.86) * mm});
            skArc(sketch, "E860", {"start": v(-7.28, -19.86) * mm, "mid": v(-7.38, -20) * mm, "end": v(-7.5, -20.11) * mm});
            skArc(sketch, "E861", {"start": v(-7.5, -20.11) * mm, "mid": v(-7.62, -20.22) * mm, "end": v(-7.75, -20.3) * mm});
            skArc(sketch, "E862", {"start": v(-7.75, -20.3) * mm, "mid": v(-7.83, -20.35) * mm, "end": v(-7.9, -20.38) * mm});
            skArc(sketch, "E863", {"start": v(-7.9, -20.38) * mm, "mid": v(-8, -20.4) * mm, "end": v(-8.08, -20.42) * mm});
            skArc(sketch, "E864", {"start": v(-8.08, -20.42) * mm, "mid": v(-8.2, -20.43) * mm, "end": v(-8.31, -20.44) * mm});
            skArc(sketch, "E865", {"start": v(-8.31, -20.44) * mm, "mid": v(-8.5, -20.44) * mm, "end": v(-8.69, -20.45) * mm});
            skArc(sketch, "E866", {"start": v(-8.69, -20.45) * mm, "mid": v(-8.97, -20.44) * mm, "end": v(-9.24, -20.42) * mm});
            skArc(sketch, "E867", {"start": v(-9.24, -20.42) * mm, "mid": v(-9.42, -20.4) * mm, "end": v(-9.58, -20.33) * mm});
            skArc(sketch, "E868", {"start": v(-9.58, -20.33) * mm, "mid": v(-9.72, -20.25) * mm, "end": v(-9.84, -20.15) * mm});
            skArc(sketch, "E869", {"start": v(-9.84, -20.15) * mm, "mid": v(-9.98, -19.99) * mm, "end": v(-10.1, -19.81) * mm});
            skArc(sketch, "E870", {"start": v(-10.1, -19.81) * mm, "mid": v(-10.15, -19.74) * mm, "end": v(-10.2, -19.67) * mm});
            skArc(sketch, "E871", {"start": v(-10.2, -19.67) * mm, "mid": v(-10.25, -19.6) * mm, "end": v(-10.3, -19.55) * mm});
            skArc(sketch, "E872", {"start": v(-10.3, -19.55) * mm, "mid": v(-10.35, -19.5) * mm, "end": v(-10.4, -19.46) * mm});
            skArc(sketch, "E873", {"start": v(-10.4, -19.46) * mm, "mid": v(-10.41, -19.45) * mm, "end": v(-10.43, -19.45) * mm});
            skArc(sketch, "E874", {"start": v(-10.43, -19.45) * mm, "mid": v(-10.46, -19.46) * mm, "end": v(-10.48, -19.48) * mm});
            skArc(sketch, "E875", {"start": v(-10.48, -19.48) * mm, "mid": v(-10.53, -19.55) * mm, "end": v(-10.58, -19.61) * mm});
            skArc(sketch, "E876", {"start": v(-10.58, -19.61) * mm, "mid": v(-10.65, -19.7) * mm, "end": v(-10.7, -19.77) * mm});
            skArc(sketch, "E877", {"start": v(-10.7, -19.77) * mm, "mid": v(-10.77, -19.87) * mm, "end": v(-10.84, -19.96) * mm});
            skArc(sketch, "E878", {"start": v(-10.84, -19.96) * mm, "mid": v(-11, -20.2) * mm, "end": v(-11.19, -20.42) * mm});
            skArc(sketch, "E879", {"start": v(-11.19, -20.42) * mm, "mid": v(-11.35, -20.61) * mm, "end": v(-11.53, -20.79) * mm});
            skArc(sketch, "E880", {"start": v(-11.53, -20.79) * mm, "mid": v(-11.7, -20.93) * mm, "end": v(-11.89, -21.06) * mm});
            skArc(sketch, "E881", {"start": v(-11.89, -21.06) * mm, "mid": v(-12.06, -21.16) * mm, "end": v(-12.25, -21.24) * mm});
            skArc(sketch, "E882", {"start": v(-12.25, -21.24) * mm, "mid": v(-12.53, -21.33) * mm, "end": v(-12.83, -21.37) * mm});
            skArc(sketch, "E883", {"start": v(-12.83, -21.37) * mm, "mid": v(-13.1, -21.37) * mm, "end": v(-13.35, -21.31) * mm});
            skArc(sketch, "E884", {"start": v(-13.35, -21.31) * mm, "mid": v(-13.63, -21.2) * mm, "end": v(-13.9, -21.04) * mm});
            skArc(sketch, "E885", {"start": v(-13.9, -21.04) * mm, "mid": v(-14.21, -20.8) * mm, "end": v(-14.51, -20.53) * mm});
            skArc(sketch, "E886", {"start": v(-14.51, -20.53) * mm, "mid": v(-14.72, -20.32) * mm, "end": v(-14.92, -20.09) * mm});
            skArc(sketch, "E887", {"start": v(-14.92, -20.09) * mm, "mid": v(-15.08, -19.86) * mm, "end": v(-15.23, -19.63) * mm});
            skArc(sketch, "E888", {"start": v(-15.23, -19.63) * mm, "mid": v(-15.35, -19.38) * mm, "end": v(-15.45, -19.13) * mm});
            skArc(sketch, "E889", {"start": v(-15.45, -19.13) * mm, "mid": v(-15.53, -18.86) * mm, "end": v(-15.58, -18.6) * mm});
            skArc(sketch, "E890", {"start": v(-15.58, -18.6) * mm, "mid": v(-15.63, -18.2) * mm, "end": v(-15.65, -17.81) * mm});
            skArc(sketch, "E891", {"start": v(-15.65, -17.81) * mm, "mid": v(-15.65, -17.1) * mm, "end": v(-15.64, -16.4) * mm});
            skArc(sketch, "E892", {"start": v(-15.64, -16.4) * mm, "mid": v(-15.62, -15.7) * mm, "end": v(-15.6, -14.98) * mm});
            skArc(sketch, "E893", {"start": v(-15.6, -14.98) * mm, "mid": v(-15.56, -14.7) * mm, "end": v(-15.49, -14.41) * mm});
            skArc(sketch, "E894", {"start": v(-15.49, -14.41) * mm, "mid": v(-15.43, -14.26) * mm, "end": v(-15.35, -14.11) * mm});
            skArc(sketch, "E895", {"start": v(-15.35, -14.11) * mm, "mid": v(-15.26, -13.98) * mm, "end": v(-15.15, -13.86) * mm});
            skArc(sketch, "E896", {"start": v(-15.15, -13.86) * mm, "mid": v(-15.03, -13.76) * mm, "end": v(-14.9, -13.68) * mm});
            skArc(sketch, "E897", {"start": v(-14.9, -13.68) * mm, "mid": v(-14.76, -13.62) * mm, "end": v(-14.62, -13.58) * mm});
            skArc(sketch, "E898", {"start": v(-14.62, -13.58) * mm, "mid": v(-14.57, -13.58) * mm, "end": v(-14.52, -13.57) * mm});
            skArc(sketch, "E899", {"start": v(-14.52, -13.57) * mm, "mid": v(-14.46, -13.56) * mm, "end": v(-14.4, -13.55) * mm});
            skArc(sketch, "E900", {"start": v(-14.4, -13.55) * mm, "mid": v(-14.36, -13.54) * mm, "end": v(-14.31, -13.53) * mm});
            skArc(sketch, "E901", {"start": v(-14.31, -13.53) * mm, "mid": v(-14.28, -13.52) * mm, "end": v(-14.25, -13.52) * mm});
            skArc(sketch, "E902", {"start": v(-14.25, -13.52) * mm, "mid": v(-14.12, -13.5) * mm, "end": v(-13.99, -13.5) * mm});
            skArc(sketch, "E903", {"start": v(-13.99, -13.5) * mm, "mid": v(-13.78, -13.5) * mm, "end": v(-13.56, -13.53) * mm});
            skArc(sketch, "E904", {"start": v(-13.56, -13.53) * mm, "mid": v(-13.35, -13.57) * mm, "end": v(-13.14, -13.61) * mm});
            skArc(sketch, "E905", {"start": v(-13.14, -13.61) * mm, "mid": v(-13, -13.66) * mm, "end": v(-12.85, -13.72) * mm});
            skArc(sketch, "E906", {"start": v(-19.13, 19.85) * mm, "mid": v(-19.44, 19.7) * mm, "end": v(-19.73, 19.51) * mm});
            skArc(sketch, "E907", {"start": v(-19.73, 19.51) * mm, "mid": v(-20, 19.25) * mm, "end": v(-20.22, 18.96) * mm});
            skArc(sketch, "E908", {"start": v(-20.22, 18.96) * mm, "mid": v(-20.51, 18.47) * mm, "end": v(-20.77, 17.96) * mm});
            skArc(sketch, "E909", {"start": v(-20.77, 17.96) * mm, "mid": v(-21.26, 16.9) * mm, "end": v(-21.74, 15.85) * mm});
            skArc(sketch, "E910", {"start": v(-21.74, 15.85) * mm, "mid": v(-21.88, 15.54) * mm, "end": v(-22.02, 15.23) * mm});
            skArc(sketch, "E911", {"start": v(-22.02, 15.23) * mm, "mid": v(-22.15, 14.95) * mm, "end": v(-22.28, 14.67) * mm});
            skArc(sketch, "E912", {"start": v(-22.28, 14.67) * mm, "mid": v(-22.4, 14.44) * mm, "end": v(-22.52, 14.2) * mm});
            skArc(sketch, "E913", {"start": v(-22.52, 14.2) * mm, "mid": v(-22.56, 14.12) * mm, "end": v(-22.62, 14.05) * mm});
            skArc(sketch, "E914", {"start": v(-22.62, 14.05) * mm, "mid": v(-22.77, 13.93) * mm, "end": v(-22.96, 13.88) * mm});
            skArc(sketch, "E915", {"start": v(-22.96, 13.88) * mm, "mid": v(-23.15, 13.91) * mm, "end": v(-23.3, 14.03) * mm});
            skArc(sketch, "E916", {"start": v(-23.3, 14.03) * mm, "mid": v(-23.56, 14.33) * mm, "end": v(-23.78, 14.66) * mm});
            skArc(sketch, "E917", {"start": v(-23.78, 14.66) * mm, "mid": v(-24.2, 15.4) * mm, "end": v(-24.62, 16.17) * mm});
            skArc(sketch, "E918", {"start": v(-24.62, 16.17) * mm, "mid": v(-24.9, 16.69) * mm, "end": v(-25.19, 17.2) * mm});
            skArc(sketch, "E919", {"start": v(-25.19, 17.2) * mm, "mid": v(-25.44, 17.64) * mm, "end": v(-25.7, 18.07) * mm});
            skArc(sketch, "E920", {"start": v(-25.7, 18.07) * mm, "mid": v(-25.93, 18.41) * mm, "end": v(-26.16, 18.75) * mm});
            skArc(sketch, "E921", {"start": v(-26.16, 18.75) * mm, "mid": v(-26.32, 18.96) * mm, "end": v(-26.5, 19.16) * mm});
            skArc(sketch, "E922", {"start": v(-26.5, 19.16) * mm, "mid": v(-26.82, 19.43) * mm, "end": v(-27.19, 19.63) * mm});
            skArc(sketch, "E923", {"start": v(-27.19, 19.63) * mm, "mid": v(-27.64, 19.77) * mm, "end": v(-28.12, 19.85) * mm});
            skArc(sketch, "E924", {"start": v(-28.12, 19.85) * mm, "mid": v(-28.84, 19.88) * mm, "end": v(-29.56, 19.85) * mm});
            skArc(sketch, "E925", {"start": v(-29.56, 19.85) * mm, "mid": v(-30.85, 19.75) * mm, "end": v(-32.14, 19.62) * mm});
            skArc(sketch, "E926", {"start": v(-32.14, 19.62) * mm, "mid": v(-32.95, 19.53) * mm, "end": v(-33.76, 19.43) * mm});
            skArc(sketch, "E927", {"start": v(-33.76, 19.43) * mm, "mid": v(-34.22, 19.35) * mm, "end": v(-34.67, 19.24) * mm});
            skArc(sketch, "E928", {"start": v(-34.67, 19.24) * mm, "mid": v(-35, 19.12) * mm, "end": v(-35.3, 18.97) * mm});
            skArc(sketch, "E929", {"start": v(-35.3, 18.97) * mm, "mid": v(-35.6, 18.77) * mm, "end": v(-35.89, 18.54) * mm});
            skArc(sketch, "E930", {"start": v(-35.89, 18.54) * mm, "mid": v(-35.98, 18.45) * mm, "end": v(-36.08, 18.37) * mm});
            skArc(sketch, "E931", {"start": v(-36.08, 18.37) * mm, "mid": v(-36.16, 18.3) * mm, "end": v(-36.25, 18.22) * mm});
            skArc(sketch, "E932", {"start": v(-36.25, 18.22) * mm, "mid": v(-36.33, 18.16) * mm, "end": v(-36.4, 18.1) * mm});
            skArc(sketch, "E933", {"start": v(-36.4, 18.1) * mm, "mid": v(-36.42, 18.1) * mm, "end": v(-36.45, 18.09) * mm});
            skArc(sketch, "E934", {"start": v(-36.45, 18.09) * mm, "mid": v(-36.47, 18.1) * mm, "end": v(-36.49, 18.1) * mm});
            skArc(sketch, "E935", {"start": v(-36.49, 18.1) * mm, "mid": v(-36.56, 18.16) * mm, "end": v(-36.62, 18.23) * mm});
            skArc(sketch, "E936", {"start": v(-36.62, 18.23) * mm, "mid": v(-36.7, 18.3) * mm, "end": v(-36.78, 18.37) * mm});
            skArc(sketch, "E937", {"start": v(-36.78, 18.37) * mm, "mid": v(-36.87, 18.46) * mm, "end": v(-36.95, 18.55) * mm});
            skArc(sketch, "E938", {"start": v(-36.95, 18.55) * mm, "mid": v(-37.19, 18.8) * mm, "end": v(-37.43, 19.02) * mm});
            skArc(sketch, "E939", {"start": v(-37.43, 19.02) * mm, "mid": v(-37.6, 19.16) * mm, "end": v(-37.77, 19.27) * mm});
            skArc(sketch, "E940", {"start": v(-37.77, 19.27) * mm, "mid": v(-37.95, 19.36) * mm, "end": v(-38.14, 19.42) * mm});
            skArc(sketch, "E941", {"start": v(-38.14, 19.42) * mm, "mid": v(-38.39, 19.46) * mm, "end": v(-38.64, 19.5) * mm});
            skArc(sketch, "E942", {"start": v(-38.64, 19.5) * mm, "mid": v(-39.34, 19.55) * mm, "end": v(-40.04, 19.57) * mm});
            skArc(sketch, "E943", {"start": v(-40.04, 19.57) * mm, "mid": v(-42.4, 19.6) * mm, "end": v(-44.74, 19.6) * mm});
            skArc(sketch, "E944", {"start": v(-44.74, 19.6) * mm, "mid": v(-47.04, 19.61) * mm, "end": v(-49.34, 19.6) * mm});
            skArc(sketch, "E945", {"start": v(-49.34, 19.6) * mm, "mid": v(-50.71, 19.6) * mm, "end": v(-52.09, 19.56) * mm});
            skArc(sketch, "E946", {"start": v(-52.09, 19.56) * mm, "mid": v(-53.71, 19.5) * mm, "end": v(-55.34, 19.47) * mm});
            skArc(sketch, "E947", {"start": v(-55.34, 19.47) * mm, "mid": v(-56.5, 19.44) * mm, "end": v(-57.67, 19.43) * mm});
            skArc(sketch, "E948", {"start": v(-57.67, 19.43) * mm, "mid": v(-58.57, 19.43) * mm, "end": v(-59.46, 19.45) * mm});
            skArc(sketch, "E949", {"start": v(-59.46, 19.45) * mm, "mid": v(-60.2, 19.48) * mm, "end": v(-60.93, 19.52) * mm});
            skArc(sketch, "E950", {"start": v(-60.93, 19.52) * mm, "mid": v(-61.94, 19.59) * mm, "end": v(-62.96, 19.61) * mm});
            skArc(sketch, "E951", {"start": v(-62.96, 19.61) * mm, "mid": v(-63.78, 19.59) * mm, "end": v(-64.6, 19.51) * mm});
            skArc(sketch, "E952", {"start": v(-64.6, 19.51) * mm, "mid": v(-65.23, 19.4) * mm, "end": v(-65.84, 19.25) * mm});
            skArc(sketch, "E953", {"start": v(-65.84, 19.25) * mm, "mid": v(-66.26, 19.07) * mm, "end": v(-66.63, 18.8) * mm});
            skArc(sketch, "E954", {"start": v(-66.63, 18.8) * mm, "mid": v(-66.8, 18.63) * mm, "end": v(-66.93, 18.43) * mm});
            skArc(sketch, "E955", {"start": v(-66.93, 18.43) * mm, "mid": v(-67.02, 18.22) * mm, "end": v(-67.07, 18) * mm});
            skArc(sketch, "E956", {"start": v(-67.07, 18) * mm, "mid": v(-67.12, 17.62) * mm, "end": v(-67.14, 17.24) * mm});
            skArc(sketch, "E957", {"start": v(-67.14, 17.24) * mm, "mid": v(-67.16, 16.08) * mm, "end": v(-67.18, 14.92) * mm});
            skArc(sketch, "E958", {"start": v(-67.18, 14.92) * mm, "mid": v(-67.2, 14.3) * mm, "end": v(-67.2, 13.67) * mm});
            skArc(sketch, "E959", {"start": v(-67.2, 13.67) * mm, "mid": v(-67.22, 13.11) * mm, "end": v(-67.24, 12.56) * mm});
            skArc(sketch, "E960", {"start": v(-67.24, 12.56) * mm, "mid": v(-67.26, 12.1) * mm, "end": v(-67.28, 11.64) * mm});
            skArc(sketch, "E961", {"start": v(-67.28, 11.64) * mm, "mid": v(-67.29, 11.48) * mm, "end": v(-67.31, 11.32) * mm});
            skArc(sketch, "E962", {"start": v(-67.31, 11.32) * mm, "mid": v(-67.35, 11.11) * mm, "end": v(-67.4, 10.9) * mm});
            skArc(sketch, "E963", {"start": v(-67.4, 10.9) * mm, "mid": v(-67.47, 10.74) * mm, "end": v(-67.55, 10.58) * mm});
            skArc(sketch, "E964", {"start": v(-67.55, 10.58) * mm, "mid": v(-67.63, 10.45) * mm, "end": v(-67.73, 10.33) * mm});
            skArc(sketch, "E965", {"start": v(-67.73, 10.33) * mm, "mid": v(-67.84, 10.24) * mm, "end": v(-67.95, 10.17) * mm});
            skArc(sketch, "E966", {"start": v(-67.95, 10.17) * mm, "mid": v(-68.14, 10.09) * mm, "end": v(-68.34, 10.04) * mm});
            skArc(sketch, "E967", {"start": v(-68.34, 10.04) * mm, "mid": v(-68.67, 9.99) * mm, "end": v(-69, 9.95) * mm});
            skArc(sketch, "E968", {"start": v(-69, 9.95) * mm, "mid": v(-69.43, 9.93) * mm, "end": v(-69.86, 9.91) * mm});
            skArc(sketch, "E969", {"start": v(-69.86, 9.91) * mm, "mid": v(-70.4, 9.9) * mm, "end": v(-70.95, 9.91) * mm});
            skArc(sketch, "E970", {"start": v(-70.95, 9.91) * mm, "mid": v(-71.45, 9.92) * mm, "end": v(-71.95, 9.94) * mm});
            skArc(sketch, "E971", {"start": v(-71.95, 9.94) * mm, "mid": v(-72.17, 9.96) * mm, "end": v(-72.4, 10) * mm});
            skArc(sketch, "E972", {"start": v(-72.4, 10) * mm, "mid": v(-72.52, 10.03) * mm, "end": v(-72.63, 10.1) * mm});
            skArc(sketch, "E973", {"start": v(-72.63, 10.1) * mm, "mid": v(-72.72, 10.18) * mm, "end": v(-72.77, 10.28) * mm});
            skArc(sketch, "E974", {"start": v(-72.77, 10.28) * mm, "mid": v(-72.83, 10.46) * mm, "end": v(-72.86, 10.64) * mm});
            skArc(sketch, "E975", {"start": v(-72.86, 10.64) * mm, "mid": v(-72.9, 11.03) * mm, "end": v(-72.93, 11.42) * mm});
            skArc(sketch, "E976", {"start": v(-72.93, 11.42) * mm, "mid": v(-72.97, 11.97) * mm, "end": v(-73, 12.52) * mm});
            skArc(sketch, "E977", {"start": v(-73, 12.52) * mm, "mid": v(-73.03, 13.27) * mm, "end": v(-73.05, 14.03) * mm});
            skArc(sketch, "E978", {"start": v(-73.05, 14.03) * mm, "mid": v(-73.1, 15.2) * mm, "end": v(-73.15, 16.38) * mm});
            skArc(sketch, "E979", {"start": v(-73.15, 16.38) * mm, "mid": v(-73.2, 17) * mm, "end": v(-73.29, 17.62) * mm});
            skArc(sketch, "E980", {"start": v(-73.29, 17.62) * mm, "mid": v(-73.38, 18) * mm, "end": v(-73.5, 18.38) * mm});
            skArc(sketch, "E981", {"start": v(-73.5, 18.38) * mm, "mid": v(-73.66, 18.66) * mm, "end": v(-73.86, 18.9) * mm});
            skArc(sketch, "E982", {"start": v(-73.86, 18.9) * mm, "mid": v(-74.02, 19.04) * mm, "end": v(-74.2, 19.16) * mm});
            skArc(sketch, "E983", {"start": v(-74.2, 19.16) * mm, "mid": v(-74.39, 19.25) * mm, "end": v(-74.59, 19.32) * mm});
            skArc(sketch, "E984", {"start": v(-74.59, 19.32) * mm, "mid": v(-74.86, 19.38) * mm, "end": v(-75.13, 19.42) * mm});
            skArc(sketch, "E985", {"start": v(-75.13, 19.42) * mm, "mid": v(-75.58, 19.47) * mm, "end": v(-76.02, 19.5) * mm});
            skArc(sketch, "E986", {"start": v(-76.02, 19.5) * mm, "mid": v(-76.33, 19.53) * mm, "end": v(-76.64, 19.54) * mm});
            skArc(sketch, "E987", {"start": v(-76.64, 19.54) * mm, "mid": v(-76.95, 19.55) * mm, "end": v(-77.26, 19.55) * mm});
            skArc(sketch, "E988", {"start": v(-77.26, 19.55) * mm, "mid": v(-77.6, 19.55) * mm, "end": v(-77.96, 19.54) * mm});
            skArc(sketch, "E989", {"start": v(-77.96, 19.54) * mm, "mid": v(-78.39, 19.52) * mm, "end": v(-78.82, 19.5) * mm});
            skArc(sketch, "E990", {"start": v(-78.82, 19.5) * mm, "mid": v(-79.57, 19.46) * mm, "end": v(-80.32, 19.4) * mm});
            skArc(sketch, "E991", {"start": v(-80.32, 19.4) * mm, "mid": v(-80.7, 19.35) * mm, "end": v(-81.07, 19.25) * mm});
            skArc(sketch, "E992", {"start": v(-81.07, 19.25) * mm, "mid": v(-81.3, 19.14) * mm, "end": v(-81.5, 18.97) * mm});
            skArc(sketch, "E993", {"start": v(-81.5, 18.97) * mm, "mid": v(-81.66, 18.76) * mm, "end": v(-81.77, 18.52) * mm});
            skArc(sketch, "E994", {"start": v(-81.77, 18.52) * mm, "mid": v(-81.88, 18.08) * mm, "end": v(-81.94, 17.63) * mm});
            skArc(sketch, "E995", {"start": v(-81.94, 17.63) * mm, "mid": v(-81.99, 16.86) * mm, "end": v(-82.01, 16.08) * mm});
            skArc(sketch, "E996", {"start": v(-82.01, 16.08) * mm, "mid": v(-82.03, 14.64) * mm, "end": v(-82.04, 13.2) * mm});
            skArc(sketch, "E997", {"start": v(-82.04, 13.2) * mm, "mid": v(-82.05, 9.1) * mm, "end": v(-82.05, 5.01) * mm});
            skLineSegment(sketch, "E998", {"start": v(-82.05, 5.01) * mm, "end": v(-82.04, -6.9) * mm});
            skLineSegment(sketch, "E999", {"start": v(-82.04, -6.9) * mm, "end": v(-81.63, -7.32) * mm});
            skArc(sketch, "E1000", {"start": v(-81.63, -7.32) * mm, "mid": v(-81.4, -7.54) * mm, "end": v(-81.13, -7.73) * mm});
            skArc(sketch, "E1001", {"start": v(-81.13, -7.73) * mm, "mid": v(-80.9, -7.84) * mm, "end": v(-80.66, -7.9) * mm});
            skArc(sketch, "E1002", {"start": v(-80.66, -7.9) * mm, "mid": v(-80.29, -7.96) * mm, "end": v(-79.9, -7.98) * mm});
            skArc(sketch, "E1003", {"start": v(-79.9, -7.98) * mm, "mid": v(-78.77, -7.98) * mm, "end": v(-77.64, -7.99) * mm});
            skArc(sketch, "E1004", {"start": v(-77.64, -7.99) * mm, "mid": v(-76.8, -7.98) * mm, "end": v(-75.95, -7.98) * mm});
            skArc(sketch, "E1005", {"start": v(-75.95, -7.98) * mm, "mid": v(-75.54, -7.98) * mm, "end": v(-75.13, -7.97) * mm});
            skArc(sketch, "E1006", {"start": v(-75.13, -7.97) * mm, "mid": v(-74.88, -7.95) * mm, "end": v(-74.64, -7.93) * mm});
            skArc(sketch, "E1007", {"start": v(-74.64, -7.93) * mm, "mid": v(-74.47, -7.9) * mm, "end": v(-74.3, -7.86) * mm});
            skArc(sketch, "E1008", {"start": v(-74.3, -7.86) * mm, "mid": v(-74.13, -7.8) * mm, "end": v(-73.97, -7.71) * mm});
            skArc(sketch, "E1009", {"start": v(-73.97, -7.71) * mm, "mid": v(-73.81, -7.6) * mm, "end": v(-73.68, -7.48) * mm});
            skArc(sketch, "E1010", {"start": v(-73.68, -7.48) * mm, "mid": v(-73.56, -7.34) * mm, "end": v(-73.46, -7.18) * mm});
            skArc(sketch, "E1011", {"start": v(-73.46, -7.18) * mm, "mid": v(-73.37, -7) * mm, "end": v(-73.3, -6.82) * mm});
            skArc(sketch, "E1012", {"start": v(-73.3, -6.82) * mm, "mid": v(-73.25, -6.6) * mm, "end": v(-73.21, -6.37) * mm});
            skArc(sketch, "E1013", {"start": v(-73.21, -6.37) * mm, "mid": v(-73.17, -5.97) * mm, "end": v(-73.13, -5.57) * mm});
            skArc(sketch, "E1014", {"start": v(-73.13, -5.57) * mm, "mid": v(-73.1, -5.04) * mm, "end": v(-73.07, -4.5) * mm});
            skArc(sketch, "E1015", {"start": v(-73.07, -4.5) * mm, "mid": v(-73.04, -3.83) * mm, "end": v(-73.02, -3.16) * mm});
            skArc(sketch, "E1016", {"start": v(-73.02, -3.16) * mm, "mid": v(-72.99, -2.25) * mm, "end": v(-72.95, -1.35) * mm});
            skArc(sketch, "E1017", {"start": v(-72.95, -1.35) * mm, "mid": v(-72.91, -0.7) * mm, "end": v(-72.85, -0.04) * mm});
            skArc(sketch, "E1018", {"start": v(-72.85, -0.04) * mm, "mid": v(-72.8, 0.43) * mm, "end": v(-72.74, 0.91) * mm});
            skArc(sketch, "E1019", {"start": v(-72.74, 0.91) * mm, "mid": v(-72.69, 1.08) * mm, "end": v(-72.59, 1.23) * mm});
            skArc(sketch, "E1020", {"start": v(-72.59, 1.23) * mm, "mid": v(-72.49, 1.31) * mm, "end": v(-72.36, 1.36) * mm});
            skArc(sketch, "E1021", {"start": v(-72.36, 1.36) * mm, "mid": v(-72.12, 1.42) * mm, "end": v(-71.88, 1.46) * mm});
            skArc(sketch, "E1022", {"start": v(-71.88, 1.46) * mm, "mid": v(-71.54, 1.5) * mm, "end": v(-71.2, 1.51) * mm});
            skArc(sketch, "E1023", {"start": v(-71.2, 1.51) * mm, "mid": v(-70.74, 1.53) * mm, "end": v(-70.29, 1.53) * mm});
            skArc(sketch, "E1024", {"start": v(-70.29, 1.53) * mm, "mid": v(-69.82, 1.53) * mm, "end": v(-69.36, 1.51) * mm});
            skArc(sketch, "E1025", {"start": v(-69.36, 1.51) * mm, "mid": v(-69, 1.49) * mm, "end": v(-68.65, 1.45) * mm});
            skArc(sketch, "E1026", {"start": v(-68.65, 1.45) * mm, "mid": v(-68.4, 1.4) * mm, "end": v(-68.14, 1.35) * mm});
            skArc(sketch, "E1027", {"start": v(-68.14, 1.35) * mm, "mid": v(-67.98, 1.3) * mm, "end": v(-67.84, 1.2) * mm});
            skArc(sketch, "E1028", {"start": v(-67.84, 1.2) * mm, "mid": v(-67.8, 1.18) * mm, "end": v(-67.77, 1.14) * mm});
            skArc(sketch, "E1029", {"start": v(-67.77, 1.14) * mm, "mid": v(-67.73, 1.09) * mm, "end": v(-67.7, 1.04) * mm});
            skArc(sketch, "E1030", {"start": v(-67.7, 1.04) * mm, "mid": v(-67.66, 0.98) * mm, "end": v(-67.63, 0.92) * mm});
            skArc(sketch, "E1031", {"start": v(-67.63, 0.92) * mm, "mid": v(-67.61, 0.87) * mm, "end": v(-67.6, 0.81) * mm});
            skArc(sketch, "E1032", {"start": v(-67.6, 0.81) * mm, "mid": v(-67.57, 0.71) * mm, "end": v(-67.55, 0.6) * mm});
            skArc(sketch, "E1033", {"start": v(-67.55, 0.6) * mm, "mid": v(-67.54, 0.22) * mm, "end": v(-67.52, -0.16) * mm});
            skArc(sketch, "E1034", {"start": v(-67.52, -0.16) * mm, "mid": v(-67.5, -0.64) * mm, "end": v(-67.48, -1.13) * mm});
            skArc(sketch, "E1035", {"start": v(-67.48, -1.13) * mm, "mid": v(-67.47, -1.74) * mm, "end": v(-67.45, -2.35) * mm});
            skArc(sketch, "E1036", {"start": v(-67.45, -2.35) * mm, "mid": v(-67.44, -2.93) * mm, "end": v(-67.43, -3.5) * mm});
            skArc(sketch, "E1037", {"start": v(-67.43, -3.5) * mm, "mid": v(-67.41, -4.04) * mm, "end": v(-67.4, -4.58) * mm});
            skArc(sketch, "E1038", {"start": v(-67.4, -4.58) * mm, "mid": v(-67.37, -5.02) * mm, "end": v(-67.35, -5.47) * mm});
            skArc(sketch, "E1039", {"start": v(-67.35, -5.47) * mm, "mid": v(-67.34, -5.66) * mm, "end": v(-67.32, -5.84) * mm});
            skArc(sketch, "E1040", {"start": v(-67.32, -5.84) * mm, "mid": v(-67.24, -6.26) * mm, "end": v(-67.14, -6.67) * mm});
            skArc(sketch, "E1041", {"start": v(-67.14, -6.67) * mm, "mid": v(-67.03, -6.96) * mm, "end": v(-66.87, -7.24) * mm});
            skArc(sketch, "E1042", {"start": v(-66.87, -7.24) * mm, "mid": v(-66.7, -7.45) * mm, "end": v(-66.47, -7.63) * mm});
            skArc(sketch, "E1043", {"start": v(-66.47, -7.63) * mm, "mid": v(-66.2, -7.78) * mm, "end": v(-65.9, -7.9) * mm});
            skArc(sketch, "E1044", {"start": v(-65.9, -7.9) * mm, "mid": v(-65.72, -7.94) * mm, "end": v(-65.55, -7.98) * mm});
            skArc(sketch, "E1045", {"start": v(-65.55, -7.98) * mm, "mid": v(-65.38, -8.01) * mm, "end": v(-65.21, -8.03) * mm});
            skArc(sketch, "E1046", {"start": v(-65.21, -8.03) * mm, "mid": v(-64.97, -8.04) * mm, "end": v(-64.73, -8.05) * mm});
            skArc(sketch, "E1047", {"start": v(-64.73, -8.05) * mm, "mid": v(-64.24, -8.05) * mm, "end": v(-63.74, -8.05) * mm});
            skArc(sketch, "E1048", {"start": v(-63.74, -8.05) * mm, "mid": v(-63.36, -8.05) * mm, "end": v(-62.97, -8.05) * mm});
            skArc(sketch, "E1049", {"start": v(-62.97, -8.05) * mm, "mid": v(-62.48, -8.04) * mm, "end": v(-61.99, -8.03) * mm});
            skArc(sketch, "E1050", {"start": v(-61.99, -8.03) * mm, "mid": v(-61.48, -8.01) * mm, "end": v(-60.97, -8) * mm});
            skArc(sketch, "E1051", {"start": v(-60.97, -8) * mm, "mid": v(-60.52, -7.98) * mm, "end": v(-60.07, -7.96) * mm});
            skArc(sketch, "E1052", {"start": v(-60.07, -7.96) * mm, "mid": v(-59.38, -7.93) * mm, "end": v(-58.69, -7.9) * mm});
            skArc(sketch, "E1053", {"start": v(-58.69, -7.9) * mm, "mid": v(-57.96, -7.9) * mm, "end": v(-57.22, -7.9) * mm});
            skArc(sketch, "E1054", {"start": v(-57.22, -7.9) * mm, "mid": v(-56.17, -7.9) * mm, "end": v(-55.12, -7.91) * mm});
            skArc(sketch, "E1055", {"start": v(-55.12, -7.91) * mm, "mid": v(-53.17, -7.94) * mm, "end": v(-51.21, -7.98) * mm});
            skArc(sketch, "E1056", {"start": v(-51.21, -7.98) * mm, "mid": v(-48.32, -8.02) * mm, "end": v(-45.43, -8.06) * mm});
            skArc(sketch, "E1057", {"start": v(-45.43, -8.06) * mm, "mid": v(-43.49, -8.08) * mm, "end": v(-41.55, -8.1) * mm});
            skArc(sketch, "E1058", {"start": v(-41.55, -8.1) * mm, "mid": v(-40.15, -8.09) * mm, "end": v(-38.75, -8.08) * mm});
            skArc(sketch, "E1059", {"start": v(-38.75, -8.08) * mm, "mid": v(-38.4, -8.06) * mm, "end": v(-38.03, -7.99) * mm});
            skArc(sketch, "E1060", {"start": v(-38.03, -7.99) * mm, "mid": v(-37.84, -7.93) * mm, "end": v(-37.66, -7.87) * mm});
            skArc(sketch, "E1061", {"start": v(-37.66, -7.87) * mm, "mid": v(-37.49, -7.8) * mm, "end": v(-37.32, -7.72) * mm});
            skArc(sketch, "E1062", {"start": v(-37.32, -7.72) * mm, "mid": v(-37.14, -7.62) * mm, "end": v(-36.96, -7.5) * mm});
            skArc(sketch, "E1063", {"start": v(-36.96, -7.5) * mm, "mid": v(-36.74, -7.36) * mm, "end": v(-36.52, -7.2) * mm});
            skArc(sketch, "E1064", {"start": v(-36.52, -7.2) * mm, "mid": v(-36.34, -7.08) * mm, "end": v(-36.14, -6.96) * mm});
            skArc(sketch, "E1065", {"start": v(-36.14, -6.96) * mm, "mid": v(-36, -6.9) * mm, "end": v(-35.87, -6.85) * mm});
            skArc(sketch, "E1066", {"start": v(-35.87, -6.85) * mm, "mid": v(-35.74, -6.83) * mm, "end": v(-35.6, -6.84) * mm});
            skArc(sketch, "E1067", {"start": v(-35.6, -6.84) * mm, "mid": v(-35.45, -6.88) * mm, "end": v(-35.3, -6.94) * mm});
            skArc(sketch, "E1068", {"start": v(-35.3, -6.94) * mm, "mid": v(-35.07, -7.02) * mm, "end": v(-34.83, -7.1) * mm});
            skArc(sketch, "E1069", {"start": v(-34.83, -7.1) * mm, "mid": v(-34.27, -7.24) * mm, "end": v(-33.71, -7.39) * mm});
            skArc(sketch, "E1070", {"start": v(-33.71, -7.39) * mm, "mid": v(-33.1, -7.54) * mm, "end": v(-32.48, -7.68) * mm});
            skArc(sketch, "E1071", {"start": v(-32.48, -7.68) * mm, "mid": v(-31.93, -7.8) * mm, "end": v(-31.37, -7.92) * mm});
            skArc(sketch, "E1072", {"start": v(-31.37, -7.92) * mm, "mid": v(-31.02, -8) * mm, "end": v(-30.67, -8.06) * mm});
            skArc(sketch, "E1073", {"start": v(-30.67, -8.06) * mm, "mid": v(-30.42, -8.1) * mm, "end": v(-30.18, -8.14) * mm});
            skArc(sketch, "E1074", {"start": v(-30.18, -8.14) * mm, "mid": v(-29.95, -8.16) * mm, "end": v(-29.73, -8.17) * mm});
            skArc(sketch, "E1075", {"start": v(-29.73, -8.17) * mm, "mid": v(-29.46, -8.18) * mm, "end": v(-29.2, -8.19) * mm});
            skArc(sketch, "E1076", {"start": v(-29.2, -8.19) * mm, "mid": v(-28.92, -8.2) * mm, "end": v(-28.64, -8.19) * mm});
            skArc(sketch, "E1077", {"start": v(-28.64, -8.19) * mm, "mid": v(-28.5, -8.18) * mm, "end": v(-28.37, -8.17) * mm});
            skArc(sketch, "E1078", {"start": v(-28.37, -8.17) * mm, "mid": v(-28.26, -8.15) * mm, "end": v(-28.15, -8.11) * mm});
            skArc(sketch, "E1079", {"start": v(-28.15, -8.11) * mm, "mid": v(-28.03, -8.06) * mm, "end": v(-27.9, -8) * mm});
            skArc(sketch, "E1080", {"start": v(-27.9, -8) * mm, "mid": v(-27.67, -7.86) * mm, "end": v(-27.47, -7.68) * mm});
            skArc(sketch, "E1081", {"start": v(-27.47, -7.68) * mm, "mid": v(-27.24, -7.4) * mm, "end": v(-27.03, -7.1) * mm});
            skArc(sketch, "E1082", {"start": v(-27.03, -7.1) * mm, "mid": v(-26.72, -6.6) * mm, "end": v(-26.44, -6.1) * mm});
            skArc(sketch, "E1083", {"start": v(-26.44, -6.1) * mm, "mid": v(-25.9, -5.08) * mm, "end": v(-25.37, -4.07) * mm});
            skArc(sketch, "E1084", {"start": v(-25.37, -4.07) * mm, "mid": v(-24.93, -3.22) * mm, "end": v(-24.48, -2.38) * mm});
            skArc(sketch, "E1085", {"start": v(-24.48, -2.38) * mm, "mid": v(-24.24, -1.95) * mm, "end": v(-23.99, -1.53) * mm});
            skArc(sketch, "E1086", {"start": v(-23.99, -1.53) * mm, "mid": v(-23.83, -1.3) * mm, "end": v(-23.65, -1.07) * mm});
            skArc(sketch, "E1087", {"start": v(-23.65, -1.07) * mm, "mid": v(-23.53, -0.98) * mm, "end": v(-23.4, -0.95) * mm});
            skArc(sketch, "E1088", {"start": v(-23.4, -0.95) * mm, "mid": v(-23.27, -0.98) * mm, "end": v(-23.17, -1.07) * mm});
            skArc(sketch, "E1089", {"start": v(-23.17, -1.07) * mm, "mid": v(-22.9, -1.47) * mm, "end": v(-22.63, -1.88) * mm});
            skArc(sketch, "E1090", {"start": v(-22.63, -1.88) * mm, "mid": v(-22.27, -2.46) * mm, "end": v(-21.92, -3.04) * mm});
            skArc(sketch, "E1091", {"start": v(-21.92, -3.04) * mm, "mid": v(-21.43, -3.9) * mm, "end": v(-20.94, -4.77) * mm});
            skArc(sketch, "E1092", {"start": v(-20.94, -4.77) * mm, "mid": v(-20.61, -5.35) * mm, "end": v(-20.28, -5.93) * mm});
            skArc(sketch, "E1093", {"start": v(-20.28, -5.93) * mm, "mid": v(-20.04, -6.33) * mm, "end": v(-19.8, -6.72) * mm});
            skArc(sketch, "E1094", {"start": v(-19.8, -6.72) * mm, "mid": v(-19.6, -7) * mm, "end": v(-19.4, -7.28) * mm});
            skArc(sketch, "E1095", {"start": v(-19.4, -7.28) * mm, "mid": v(-19.25, -7.46) * mm, "end": v(-19.08, -7.63) * mm});
            skArc(sketch, "E1096", {"start": v(-19.08, -7.63) * mm, "mid": v(-18.92, -7.77) * mm, "end": v(-18.75, -7.88) * mm});
            skArc(sketch, "E1097", {"start": v(-18.75, -7.88) * mm, "mid": v(-18.56, -8) * mm, "end": v(-18.37, -8.09) * mm});
            skArc(sketch, "E1098", {"start": v(-18.37, -8.09) * mm, "mid": v(-18.17, -8.16) * mm, "end": v(-17.97, -8.22) * mm});
            skArc(sketch, "E1099", {"start": v(-17.97, -8.22) * mm, "mid": v(-17.77, -8.27) * mm, "end": v(-17.58, -8.29) * mm});
            skArc(sketch, "E1100", {"start": v(-17.58, -8.29) * mm, "mid": v(-17.18, -8.3) * mm, "end": v(-16.79, -8.25) * mm});
            skArc(sketch, "E1101", {"start": v(-16.79, -8.25) * mm, "mid": v(-16.02, -8.11) * mm, "end": v(-15.26, -7.96) * mm});
            skArc(sketch, "E1102", {"start": v(-15.26, -7.96) * mm, "mid": v(-14.36, -7.77) * mm, "end": v(-13.47, -7.56) * mm});
            skArc(sketch, "E1103", {"start": v(-13.47, -7.56) * mm, "mid": v(-12.53, -7.32) * mm, "end": v(-11.6, -7.06) * mm});
            skLineSegment(sketch, "E1104", {"start": v(-11.6, -7.06) * mm, "end": v(-10.25, -6.67) * mm});
            skLineSegment(sketch, "E1105", {"start": v(-10.25, -6.67) * mm, "end": v(-9.82, -7.13) * mm});
            skArc(sketch, "E1106", {"start": v(-9.82, -7.13) * mm, "mid": v(-9.64, -7.31) * mm, "end": v(-9.45, -7.48) * mm});
            skArc(sketch, "E1107", {"start": v(-9.45, -7.48) * mm, "mid": v(-9.27, -7.61) * mm, "end": v(-9.07, -7.73) * mm});
            skArc(sketch, "E1108", {"start": v(-9.07, -7.73) * mm, "mid": v(-8.87, -7.83) * mm, "end": v(-8.65, -7.9) * mm});
            skArc(sketch, "E1109", {"start": v(-8.65, -7.9) * mm, "mid": v(-8.4, -7.97) * mm, "end": v(-8.14, -8.03) * mm});
            skArc(sketch, "E1110", {"start": v(-8.14, -8.03) * mm, "mid": v(-7.76, -8.07) * mm, "end": v(-7.38, -8.09) * mm});
            skArc(sketch, "E1111", {"start": v(-7.38, -8.09) * mm, "mid": v(-6.28, -8.08) * mm, "end": v(-5.19, -8.07) * mm});
            skArc(sketch, "E1112", {"start": v(-5.19, -8.07) * mm, "mid": v(-4.08, -8.05) * mm, "end": v(-2.97, -8.03) * mm});
            skArc(sketch, "E1113", {"start": v(-2.97, -8.03) * mm, "mid": v(-2.65, -8) * mm, "end": v(-2.32, -7.95) * mm});
            skArc(sketch, "E1114", {"start": v(-2.32, -7.95) * mm, "mid": v(-2.09, -7.86) * mm, "end": v(-1.88, -7.74) * mm});
            skArc(sketch, "E1115", {"start": v(-1.88, -7.74) * mm, "mid": v(-1.64, -7.53) * mm, "end": v(-1.42, -7.3) * mm});
            skArc(sketch, "E1116", {"start": v(-1.42, -7.3) * mm, "mid": v(-1.2, -7.04) * mm, "end": v(-1.02, -6.75) * mm});
            skArc(sketch, "E1117", {"start": v(-1.02, -6.75) * mm, "mid": v(-0.87, -6.45) * mm, "end": v(-0.76, -6.13) * mm});
            skArc(sketch, "E1118", {"start": v(-0.76, -6.13) * mm, "mid": v(-0.73, -6.05) * mm, "end": v(-0.71, -5.97) * mm});
            skArc(sketch, "E1119", {"start": v(-0.71, -5.97) * mm, "mid": v(-0.67, -5.76) * mm, "end": v(-0.63, -5.54) * mm});
            skArc(sketch, "E1120", {"start": v(-0.63, -5.54) * mm, "mid": v(-0.58, -5.29) * mm, "end": v(-0.54, -5.03) * mm});
            skArc(sketch, "E1121", {"start": v(-0.54, -5.03) * mm, "mid": v(-0.49, -4.75) * mm, "end": v(-0.44, -4.47) * mm});
            skArc(sketch, "E1122", {"start": v(-0.44, -4.47) * mm, "mid": v(-0.34, -3.9) * mm, "end": v(-0.23, -3.33) * mm});
            skArc(sketch, "E1123", {"start": v(-0.23, -3.33) * mm, "mid": v(-0.15, -3.02) * mm, "end": v(-0.04, -2.71) * mm});
            skArc(sketch, "E1124", {"start": v(-0.04, -2.71) * mm, "mid": v(0.07, -2.51) * mm, "end": v(0.2, -2.33) * mm});
            skArc(sketch, "E1125", {"start": v(0.2, -2.33) * mm, "mid": v(0.36, -2.19) * mm, "end": v(0.55, -2.07) * mm});
            skArc(sketch, "E1126", {"start": v(0.55, -2.07) * mm, "mid": v(0.68, -2.01) * mm, "end": v(0.82, -1.97) * mm});
            skArc(sketch, "E1127", {"start": v(0.82, -1.97) * mm, "mid": v(0.96, -1.94) * mm, "end": v(1.1, -1.92) * mm});
            skArc(sketch, "E1128", {"start": v(1.1, -1.92) * mm, "mid": v(1.33, -1.9) * mm, "end": v(1.56, -1.9) * mm});
            skArc(sketch, "E1129", {"start": v(1.56, -1.9) * mm, "mid": v(2.2, -1.9) * mm, "end": v(2.83, -1.9) * mm});
            skArc(sketch, "E1130", {"start": v(2.83, -1.9) * mm, "mid": v(3.52, -1.9) * mm, "end": v(4.21, -1.9) * mm});
            skArc(sketch, "E1131", {"start": v(4.21, -1.9) * mm, "mid": v(4.54, -1.92) * mm, "end": v(4.86, -1.96) * mm});
            skArc(sketch, "E1132", {"start": v(4.86, -1.96) * mm, "mid": v(5.04, -2) * mm, "end": v(5.22, -2.06) * mm});
            skArc(sketch, "E1133", {"start": v(5.22, -2.06) * mm, "mid": v(5.33, -2.14) * mm, "end": v(5.4, -2.26) * mm});
            skArc(sketch, "E1134", {"start": v(5.4, -2.26) * mm, "mid": v(5.47, -2.4) * mm, "end": v(5.51, -2.56) * mm});
            skArc(sketch, "E1135", {"start": v(5.51, -2.56) * mm, "mid": v(5.58, -2.83) * mm, "end": v(5.64, -3.11) * mm});
            skArc(sketch, "E1136", {"start": v(5.64, -3.11) * mm, "mid": v(5.71, -3.45) * mm, "end": v(5.78, -3.8) * mm});
            skArc(sketch, "E1137", {"start": v(5.78, -3.8) * mm, "mid": v(5.84, -4.17) * mm, "end": v(5.9, -4.56) * mm});
            skArc(sketch, "E1138", {"start": v(5.9, -4.56) * mm, "mid": v(6.02, -5.26) * mm, "end": v(6.15, -5.96) * mm});
            skArc(sketch, "E1139", {"start": v(6.15, -5.96) * mm, "mid": v(6.25, -6.38) * mm, "end": v(6.4, -6.8) * mm});
            skArc(sketch, "E1140", {"start": v(6.4, -6.8) * mm, "mid": v(6.54, -7.07) * mm, "end": v(6.73, -7.32) * mm});
            skArc(sketch, "E1141", {"start": v(6.73, -7.32) * mm, "mid": v(6.94, -7.52) * mm, "end": v(7.19, -7.68) * mm});
            skArc(sketch, "E1142", {"start": v(7.19, -7.68) * mm, "mid": v(7.43, -7.79) * mm, "end": v(7.68, -7.86) * mm});
            skArc(sketch, "E1143", {"start": v(7.68, -7.86) * mm, "mid": v(8.01, -7.93) * mm, "end": v(8.34, -7.97) * mm});
            skArc(sketch, "E1144", {"start": v(8.34, -7.97) * mm, "mid": v(8.84, -8) * mm, "end": v(9.35, -8.03) * mm});
            skArc(sketch, "E1145", {"start": v(9.35, -8.03) * mm, "mid": v(10.25, -8.05) * mm, "end": v(11.16, -8.07) * mm});
            skArc(sketch, "E1146", {"start": v(11.16, -8.07) * mm, "mid": v(12, -8.08) * mm, "end": v(12.84, -8.09) * mm});
            skArc(sketch, "E1147", {"start": v(12.84, -8.09) * mm, "mid": v(13.16, -8.09) * mm, "end": v(13.48, -8.08) * mm});
            skArc(sketch, "E1148", {"start": v(13.48, -8.08) * mm, "mid": v(13.67, -8.07) * mm, "end": v(13.86, -8.04) * mm});
            skArc(sketch, "E1149", {"start": v(13.86, -8.04) * mm, "mid": v(14.02, -8) * mm, "end": v(14.18, -7.96) * mm});
            skArc(sketch, "E1150", {"start": v(14.18, -7.96) * mm, "mid": v(14.43, -7.83) * mm, "end": v(14.67, -7.67) * mm});
            skArc(sketch, "E1151", {"start": v(14.67, -7.67) * mm, "mid": v(14.89, -7.47) * mm, "end": v(15.07, -7.24) * mm});
            skArc(sketch, "E1152", {"start": v(15.07, -7.24) * mm, "mid": v(15.22, -6.98) * mm, "end": v(15.33, -6.7) * mm});
            skArc(sketch, "E1153", {"start": v(15.33, -6.7) * mm, "mid": v(15.4, -6.42) * mm, "end": v(15.43, -6.14) * mm});
            skArc(sketch, "E1154", {"start": v(15.43, -6.14) * mm, "mid": v(15.4, -5.47) * mm, "end": v(15.3, -4.8) * mm});
            skArc(sketch, "E1155", {"start": v(15.3, -4.8) * mm, "mid": v(14.4, -0.03) * mm, "end": v(13.5, 4.74) * mm});
            skArc(sketch, "E1156", {"start": v(13.5, 4.74) * mm, "mid": v(12.65, 9.16) * mm, "end": v(11.79, 13.57) * mm});
            skArc(sketch, "E1157", {"start": v(11.79, 13.57) * mm, "mid": v(11.35, 15.69) * mm, "end": v(10.87, 17.8) * mm});
            skArc(sketch, "E1158", {"start": v(10.87, 17.8) * mm, "mid": v(10.74, 18.21) * mm, "end": v(10.56, 18.6) * mm});
            skArc(sketch, "E1159", {"start": v(10.56, 18.6) * mm, "mid": v(10.35, 18.89) * mm, "end": v(10.08, 19.1) * mm});
            skArc(sketch, "E1160", {"start": v(10.08, 19.1) * mm, "mid": v(9.7, 19.28) * mm, "end": v(9.3, 19.39) * mm});
            skArc(sketch, "E1161", {"start": v(9.3, 19.39) * mm, "mid": v(8.62, 19.49) * mm, "end": v(7.93, 19.56) * mm});
            skArc(sketch, "E1162", {"start": v(7.93, 19.56) * mm, "mid": v(7.23, 19.6) * mm, "end": v(6.52, 19.61) * mm});
            skArc(sketch, "E1163", {"start": v(6.52, 19.61) * mm, "mid": v(4.55, 19.62) * mm, "end": v(2.58, 19.63) * mm});
            skArc(sketch, "E1164", {"start": v(2.58, 19.63) * mm, "mid": v(0.6, 19.62) * mm, "end": v(-1.38, 19.62) * mm});
            skArc(sketch, "E1165", {"start": v(-1.38, 19.62) * mm, "mid": v(-2.03, 19.6) * mm, "end": v(-2.67, 19.56) * mm});
            skArc(sketch, "E1166", {"start": v(-2.67, 19.56) * mm, "mid": v(-3.16, 19.51) * mm, "end": v(-3.66, 19.44) * mm});
            skArc(sketch, "E1167", {"start": v(-3.66, 19.44) * mm, "mid": v(-3.97, 19.36) * mm, "end": v(-4.28, 19.25) * mm});
            skArc(sketch, "E1168", {"start": v(-4.28, 19.25) * mm, "mid": v(-4.51, 19.12) * mm, "end": v(-4.71, 18.94) * mm});
            skArc(sketch, "E1169", {"start": v(-4.71, 18.94) * mm, "mid": v(-4.9, 18.72) * mm, "end": v(-5.06, 18.47) * mm});
            skArc(sketch, "E1170", {"start": v(-5.06, 18.47) * mm, "mid": v(-5.24, 18.08) * mm, "end": v(-5.37, 17.68) * mm});
            skArc(sketch, "E1171", {"start": v(-5.37, 17.68) * mm, "mid": v(-5.62, 16.63) * mm, "end": v(-5.86, 15.59) * mm});
            skArc(sketch, "E1172", {"start": v(-5.86, 15.59) * mm, "mid": v(-6.19, 14.1) * mm, "end": v(-6.5, 12.6) * mm});
            skArc(sketch, "E1173", {"start": v(-6.5, 12.6) * mm, "mid": v(-6.93, 10.41) * mm, "end": v(-7.36, 8.22) * mm});
            skArc(sketch, "E1174", {"start": v(-7.36, 8.22) * mm, "mid": v(-7.93, 5.24) * mm, "end": v(-8.51, 2.27) * mm});
            skArc(sketch, "E1175", {"start": v(-8.51, 2.27) * mm, "mid": v(-8.9, 0.36) * mm, "end": v(-9.28, -1.55) * mm});
            skArc(sketch, "E1176", {"start": v(-9.28, -1.55) * mm, "mid": v(-9.58, -2.97) * mm, "end": v(-9.87, -4.39) * mm});
            skArc(sketch, "E1177", {"start": v(-9.87, -4.39) * mm, "mid": v(-9.92, -4.53) * mm, "end": v(-10.01, -4.65) * mm});
            skArc(sketch, "E1178", {"start": v(-10.01, -4.65) * mm, "mid": v(-10.08, -4.7) * mm, "end": v(-10.17, -4.72) * mm});
            skArc(sketch, "E1179", {"start": v(-10.17, -4.72) * mm, "mid": v(-10.26, -4.7) * mm, "end": v(-10.34, -4.66) * mm});
            skArc(sketch, "E1180", {"start": v(-10.34, -4.66) * mm, "mid": v(-10.46, -4.57) * mm, "end": v(-10.55, -4.46) * mm});
            skArc(sketch, "E1181", {"start": v(-10.55, -4.46) * mm, "mid": v(-10.7, -4.25) * mm, "end": v(-10.84, -4.05) * mm});
            skArc(sketch, "E1182", {"start": v(-10.84, -4.05) * mm, "mid": v(-11.5, -3) * mm, "end": v(-12.14, -1.93) * mm});
            skArc(sketch, "E1183", {"start": v(-12.14, -1.93) * mm, "mid": v(-13.03, -0.43) * mm, "end": v(-13.91, 1.07) * mm});
            skArc(sketch, "E1184", {"start": v(-13.91, 1.07) * mm, "mid": v(-14.8, 2.6) * mm, "end": v(-15.67, 4.13) * mm});
            skArc(sketch, "E1185", {"start": v(-15.67, 4.13) * mm, "mid": v(-15.9, 4.56) * mm, "end": v(-16.08, 5) * mm});
            skArc(sketch, "E1186", {"start": v(-16.08, 5) * mm, "mid": v(-16.14, 5.2) * mm, "end": v(-16.2, 5.39) * mm});
            skArc(sketch, "E1187", {"start": v(-16.2, 5.39) * mm, "mid": v(-16.21, 5.57) * mm, "end": v(-16.22, 5.76) * mm});
            skArc(sketch, "E1188", {"start": v(-16.22, 5.76) * mm, "mid": v(-16.2, 5.95) * mm, "end": v(-16.17, 6.14) * mm});
            skArc(sketch, "E1189", {"start": v(-16.17, 6.14) * mm, "mid": v(-16.12, 6.34) * mm, "end": v(-16.05, 6.54) * mm});
            skArc(sketch, "E1190", {"start": v(-16.05, 6.54) * mm, "mid": v(-15.9, 6.87) * mm, "end": v(-15.74, 7.2) * mm});
            skArc(sketch, "E1191", {"start": v(-15.74, 7.2) * mm, "mid": v(-15.33, 8) * mm, "end": v(-14.91, 8.8) * mm});
            skArc(sketch, "E1192", {"start": v(-14.91, 8.8) * mm, "mid": v(-14.44, 9.69) * mm, "end": v(-13.97, 10.58) * mm});
            skArc(sketch, "E1193", {"start": v(-13.97, 10.58) * mm, "mid": v(-13.5, 11.43) * mm, "end": v(-13.03, 12.28) * mm});
            skArc(sketch, "E1194", {"start": v(-13.03, 12.28) * mm, "mid": v(-12.62, 13.02) * mm, "end": v(-12.22, 13.77) * mm});
            skArc(sketch, "E1195", {"start": v(-12.22, 13.77) * mm, "mid": v(-11.86, 14.45) * mm, "end": v(-11.5, 15.13) * mm});
            skArc(sketch, "E1196", {"start": v(-11.5, 15.13) * mm, "mid": v(-11.22, 15.7) * mm, "end": v(-10.95, 16.27) * mm});
            skArc(sketch, "E1197", {"start": v(-10.95, 16.27) * mm, "mid": v(-10.8, 16.58) * mm, "end": v(-10.69, 16.9) * mm});
            skArc(sketch, "E1198", {"start": v(-10.69, 16.9) * mm, "mid": v(-10.62, 17.12) * mm, "end": v(-10.57, 17.35) * mm});
            skArc(sketch, "E1199", {"start": v(-10.57, 17.35) * mm, "mid": v(-10.54, 17.58) * mm, "end": v(-10.52, 17.8) * mm});
            skArc(sketch, "E1200", {"start": v(-10.52, 17.8) * mm, "mid": v(-10.53, 18.01) * mm, "end": v(-10.56, 18.22) * mm});
            skArc(sketch, "E1201", {"start": v(-10.56, 18.22) * mm, "mid": v(-10.6, 18.4) * mm, "end": v(-10.67, 18.56) * mm});
            skArc(sketch, "E1202", {"start": v(-10.67, 18.56) * mm, "mid": v(-10.84, 18.8) * mm, "end": v(-11.07, 18.96) * mm});
            skArc(sketch, "E1203", {"start": v(-11.07, 18.96) * mm, "mid": v(-11.44, 19.13) * mm, "end": v(-11.82, 19.26) * mm});
            skArc(sketch, "E1204", {"start": v(-11.82, 19.26) * mm, "mid": v(-12.45, 19.4) * mm, "end": v(-13.09, 19.5) * mm});
            skArc(sketch, "E1205", {"start": v(-13.09, 19.5) * mm, "mid": v(-14.27, 19.66) * mm, "end": v(-15.44, 19.8) * mm});
            skArc(sketch, "E1206", {"start": v(-15.44, 19.8) * mm, "mid": v(-16.1, 19.87) * mm, "end": v(-16.75, 19.93) * mm});
            skArc(sketch, "E1207", {"start": v(-16.75, 19.93) * mm, "mid": v(-17.27, 19.96) * mm, "end": v(-17.8, 19.97) * mm});
            skArc(sketch, "E1208", {"start": v(-17.8, 19.97) * mm, "mid": v(-18.2, 19.97) * mm, "end": v(-18.61, 19.95) * mm});
            skArc(sketch, "E1209", {"start": v(-18.61, 19.95) * mm, "mid": v(-18.87, 19.92) * mm, "end": v(-19.13, 19.85) * mm});
            skArc(sketch, "E1210", {"start": v(-36.04, 16.78) * mm, "mid": v(-35.7, 16.32) * mm, "end": v(-35.4, 15.84) * mm});
            skArc(sketch, "E1211", {"start": v(-35.4, 15.84) * mm, "mid": v(-34.6, 14.47) * mm, "end": v(-33.82, 13.09) * mm});
            skArc(sketch, "E1212", {"start": v(-33.82, 13.09) * mm, "mid": v(-33.02, 11.69) * mm, "end": v(-32.24, 10.28) * mm});
            skArc(sketch, "E1213", {"start": v(-32.24, 10.28) * mm, "mid": v(-31.69, 9.26) * mm, "end": v(-31.16, 8.22) * mm});
            skArc(sketch, "E1214", {"start": v(-31.16, 8.22) * mm, "mid": v(-30.84, 7.58) * mm, "end": v(-30.53, 6.92) * mm});
            skArc(sketch, "E1215", {"start": v(-30.53, 6.92) * mm, "mid": v(-30.4, 6.56) * mm, "end": v(-30.3, 6.2) * mm});
            skArc(sketch, "E1216", {"start": v(-30.3, 6.2) * mm, "mid": v(-30.28, 5.9) * mm, "end": v(-30.31, 5.6) * mm});
            skArc(sketch, "E1217", {"start": v(-30.31, 5.6) * mm, "mid": v(-30.4, 5.24) * mm, "end": v(-30.53, 4.89) * mm});
            skArc(sketch, "E1218", {"start": v(-30.53, 4.89) * mm, "mid": v(-30.85, 4.2) * mm, "end": v(-31.2, 3.52) * mm});
            skArc(sketch, "E1219", {"start": v(-31.2, 3.52) * mm, "mid": v(-31.87, 2.3) * mm, "end": v(-32.56, 1.08) * mm});
            skArc(sketch, "E1220", {"start": v(-32.56, 1.08) * mm, "mid": v(-33.28, -0.17) * mm, "end": v(-34, -1.4) * mm});
            skArc(sketch, "E1221", {"start": v(-34, -1.4) * mm, "mid": v(-34.57, -2.32) * mm, "end": v(-35.15, -3.22) * mm});
            skArc(sketch, "E1222", {"start": v(-35.15, -3.22) * mm, "mid": v(-35.37, -3.54) * mm, "end": v(-35.61, -3.84) * mm});
            skArc(sketch, "E1223", {"start": v(-35.61, -3.84) * mm, "mid": v(-35.74, -3.9) * mm, "end": v(-35.88, -3.88) * mm});
            skArc(sketch, "E1224", {"start": v(-35.88, -3.88) * mm, "mid": v(-36, -3.75) * mm, "end": v(-36.07, -3.58) * mm});
            skArc(sketch, "E1225", {"start": v(-36.07, -3.58) * mm, "mid": v(-36.12, -3.09) * mm, "end": v(-36.16, -2.59) * mm});
            skArc(sketch, "E1226", {"start": v(-36.16, -2.59) * mm, "mid": v(-36.22, -1.98) * mm, "end": v(-36.32, -1.38) * mm});
            skArc(sketch, "E1227", {"start": v(-36.32, -1.38) * mm, "mid": v(-36.44, -0.95) * mm, "end": v(-36.63, -0.55) * mm});
            skArc(sketch, "E1228", {"start": v(-36.63, -0.55) * mm, "mid": v(-36.84, -0.25) * mm, "end": v(-37.12, 0) * mm});
            skArc(sketch, "E1229", {"start": v(-37.12, 0) * mm, "mid": v(-37.47, 0.21) * mm, "end": v(-37.84, 0.36) * mm});
            skArc(sketch, "E1230", {"start": v(-37.84, 0.36) * mm, "mid": v(-38.04, 0.41) * mm, "end": v(-38.23, 0.43) * mm});
            skArc(sketch, "E1231", {"start": v(-38.23, 0.43) * mm, "mid": v(-38.62, 0.45) * mm, "end": v(-39, 0.46) * mm});
            skArc(sketch, "E1232", {"start": v(-39, 0.46) * mm, "mid": v(-39.7, 0.47) * mm, "end": v(-40.37, 0.47) * mm});
            skArc(sketch, "E1233", {"start": v(-40.37, 0.47) * mm, "mid": v(-41.99, 0.47) * mm, "end": v(-43.6, 0.46) * mm});
            skArc(sketch, "E1234", {"start": v(-43.6, 0.46) * mm, "mid": v(-44.63, 0.46) * mm, "end": v(-45.67, 0.45) * mm});
            skArc(sketch, "E1235", {"start": v(-45.67, 0.45) * mm, "mid": v(-46.57, 0.45) * mm, "end": v(-47.47, 0.46) * mm});
            skArc(sketch, "E1236", {"start": v(-47.47, 0.46) * mm, "mid": v(-48.25, 0.46) * mm, "end": v(-49.03, 0.46) * mm});
            skArc(sketch, "E1237", {"start": v(-49.03, 0.46) * mm, "mid": v(-49.14, 0.47) * mm, "end": v(-49.24, 0.48) * mm});
            skArc(sketch, "E1238", {"start": v(-49.24, 0.48) * mm, "mid": v(-49.32, 0.5) * mm, "end": v(-49.4, 0.52) * mm});
            skArc(sketch, "E1239", {"start": v(-49.4, 0.52) * mm, "mid": v(-49.45, 0.54) * mm, "end": v(-49.5, 0.56) * mm});
            skArc(sketch, "E1240", {"start": v(-49.5, 0.56) * mm, "mid": v(-49.52, 0.6) * mm, "end": v(-49.55, 0.64) * mm});
            skArc(sketch, "E1241", {"start": v(-49.55, 0.64) * mm, "mid": v(-49.58, 0.7) * mm, "end": v(-49.6, 0.76) * mm});
            skArc(sketch, "E1242", {"start": v(-49.6, 0.76) * mm, "mid": v(-49.63, 0.88) * mm, "end": v(-49.65, 1) * mm});
            skArc(sketch, "E1243", {"start": v(-49.65, 1) * mm, "mid": v(-49.64, 1.1) * mm, "end": v(-49.6, 1.19) * mm});
            skArc(sketch, "E1244", {"start": v(-49.6, 1.19) * mm, "mid": v(-49.55, 1.27) * mm, "end": v(-49.48, 1.33) * mm});
            skArc(sketch, "E1245", {"start": v(-49.48, 1.33) * mm, "mid": v(-49.38, 1.39) * mm, "end": v(-49.28, 1.43) * mm});
            skArc(sketch, "E1246", {"start": v(-49.28, 1.43) * mm, "mid": v(-49.16, 1.46) * mm, "end": v(-49.04, 1.47) * mm});
            skArc(sketch, "E1247", {"start": v(-49.04, 1.47) * mm, "mid": v(-48.57, 1.49) * mm, "end": v(-48.1, 1.5) * mm});
            skArc(sketch, "E1248", {"start": v(-48.1, 1.5) * mm, "mid": v(-47.47, 1.52) * mm, "end": v(-46.85, 1.54) * mm});
            skArc(sketch, "E1249", {"start": v(-46.85, 1.54) * mm, "mid": v(-45.99, 1.55) * mm, "end": v(-45.12, 1.57) * mm});
            skArc(sketch, "E1250", {"start": v(-45.12, 1.57) * mm, "mid": v(-44.24, 1.58) * mm, "end": v(-43.36, 1.6) * mm});
            skArc(sketch, "E1251", {"start": v(-43.36, 1.6) * mm, "mid": v(-42.72, 1.61) * mm, "end": v(-42.1, 1.63) * mm});
            skArc(sketch, "E1252", {"start": v(-42.1, 1.63) * mm, "mid": v(-41.64, 1.65) * mm, "end": v(-41.18, 1.67) * mm});
            skArc(sketch, "E1253", {"start": v(-41.18, 1.67) * mm, "mid": v(-41.02, 1.68) * mm, "end": v(-40.86, 1.71) * mm});
            skArc(sketch, "E1254", {"start": v(-40.86, 1.71) * mm, "mid": v(-40.75, 1.74) * mm, "end": v(-40.64, 1.78) * mm});
            skArc(sketch, "E1255", {"start": v(-40.64, 1.78) * mm, "mid": v(-40.55, 1.81) * mm, "end": v(-40.47, 1.86) * mm});
            skArc(sketch, "E1256", {"start": v(-40.47, 1.86) * mm, "mid": v(-40.37, 1.92) * mm, "end": v(-40.3, 2) * mm});
            skArc(sketch, "E1257", {"start": v(-40.3, 2) * mm, "mid": v(-40.17, 2.1) * mm, "end": v(-40.05, 2.23) * mm});
            skArc(sketch, "E1258", {"start": v(-40.05, 2.23) * mm, "mid": v(-39.94, 2.34) * mm, "end": v(-39.83, 2.45) * mm});
            skArc(sketch, "E1259", {"start": v(-39.83, 2.45) * mm, "mid": v(-39.76, 2.54) * mm, "end": v(-39.7, 2.63) * mm});
            skArc(sketch, "E1260", {"start": v(-39.7, 2.63) * mm, "mid": v(-39.64, 2.71) * mm, "end": v(-39.6, 2.8) * mm});
            skArc(sketch, "E1261", {"start": v(-39.6, 2.8) * mm, "mid": v(-39.57, 2.88) * mm, "end": v(-39.54, 2.97) * mm});
            skArc(sketch, "E1262", {"start": v(-39.54, 2.97) * mm, "mid": v(-39.5, 3.24) * mm, "end": v(-39.46, 3.51) * mm});
            skArc(sketch, "E1263", {"start": v(-39.46, 3.51) * mm, "mid": v(-39.44, 4.13) * mm, "end": v(-39.42, 4.76) * mm});
            skArc(sketch, "E1264", {"start": v(-39.42, 4.76) * mm, "mid": v(-39.41, 5.41) * mm, "end": v(-39.4, 6.07) * mm});
            skArc(sketch, "E1265", {"start": v(-39.4, 6.07) * mm, "mid": v(-39.42, 6.6) * mm, "end": v(-39.44, 7.15) * mm});
            skArc(sketch, "E1266", {"start": v(-39.44, 7.15) * mm, "mid": v(-39.47, 7.57) * mm, "end": v(-39.51, 8) * mm});
            skArc(sketch, "E1267", {"start": v(-39.51, 8) * mm, "mid": v(-39.55, 8.24) * mm, "end": v(-39.61, 8.47) * mm});
            skArc(sketch, "E1268", {"start": v(-39.61, 8.47) * mm, "mid": v(-39.7, 8.66) * mm, "end": v(-39.8, 8.84) * mm});
            skArc(sketch, "E1269", {"start": v(-39.8, 8.84) * mm, "mid": v(-40, 9.08) * mm, "end": v(-40.19, 9.31) * mm});
            skLineSegment(sketch, "E1270", {"start": v(-40.19, 9.31) * mm, "end": v(-40.57, 9.74) * mm});
            skLineSegment(sketch, "E1271", {"start": v(-40.57, 9.74) * mm, "end": v(-44.4, 9.78) * mm});
            skArc(sketch, "E1272", {"start": v(-44.4, 9.78) * mm, "mid": v(-45.82, 9.8) * mm, "end": v(-47.24, 9.82) * mm});
            skArc(sketch, "E1273", {"start": v(-47.24, 9.82) * mm, "mid": v(-47.89, 9.84) * mm, "end": v(-48.53, 9.88) * mm});
            skArc(sketch, "E1274", {"start": v(-48.53, 9.88) * mm, "mid": v(-48.9, 9.9) * mm, "end": v(-49.27, 9.95) * mm});
            skArc(sketch, "E1275", {"start": v(-49.27, 9.95) * mm, "mid": v(-49.43, 10) * mm, "end": v(-49.55, 10.1) * mm});
            skArc(sketch, "E1276", {"start": v(-49.55, 10.1) * mm, "mid": v(-49.6, 10.2) * mm, "end": v(-49.64, 10.3) * mm});
            skArc(sketch, "E1277", {"start": v(-49.64, 10.3) * mm, "mid": v(-49.67, 10.4) * mm, "end": v(-49.67, 10.5) * mm});
            skArc(sketch, "E1278", {"start": v(-49.67, 10.5) * mm, "mid": v(-49.66, 10.62) * mm, "end": v(-49.63, 10.73) * mm});
            skArc(sketch, "E1279", {"start": v(-49.63, 10.73) * mm, "mid": v(-49.58, 10.83) * mm, "end": v(-49.52, 10.91) * mm});
            skArc(sketch, "E1280", {"start": v(-49.52, 10.91) * mm, "mid": v(-49.46, 10.97) * mm, "end": v(-49.4, 11.02) * mm});
            skArc(sketch, "E1281", {"start": v(-49.4, 11.02) * mm, "mid": v(-49.34, 11.05) * mm, "end": v(-49.28, 11.08) * mm});
            skArc(sketch, "E1282", {"start": v(-49.28, 11.08) * mm, "mid": v(-49.18, 11.1) * mm, "end": v(-49.09, 11.1) * mm});
            skArc(sketch, "E1283", {"start": v(-49.09, 11.1) * mm, "mid": v(-48.89, 11.13) * mm, "end": v(-48.69, 11.14) * mm});
            skArc(sketch, "E1284", {"start": v(-48.69, 11.14) * mm, "mid": v(-48.47, 11.15) * mm, "end": v(-48.25, 11.15) * mm});
            skArc(sketch, "E1285", {"start": v(-48.25, 11.15) * mm, "mid": v(-47.64, 11.15) * mm, "end": v(-47.02, 11.14) * mm});
            skArc(sketch, "E1286", {"start": v(-47.02, 11.14) * mm, "mid": v(-46.3, 11.13) * mm, "end": v(-45.57, 11.12) * mm});
            skArc(sketch, "E1287", {"start": v(-45.57, 11.12) * mm, "mid": v(-44.77, 11.11) * mm, "end": v(-43.96, 11.1) * mm});
            skArc(sketch, "E1288", {"start": v(-43.96, 11.1) * mm, "mid": v(-42.2, 11.06) * mm, "end": v(-40.42, 11.04) * mm});
            skArc(sketch, "E1289", {"start": v(-40.42, 11.04) * mm, "mid": v(-39.68, 11.05) * mm, "end": v(-38.94, 11.1) * mm});
            skArc(sketch, "E1290", {"start": v(-38.94, 11.1) * mm, "mid": v(-38.52, 11.16) * mm, "end": v(-38.1, 11.28) * mm});
            skArc(sketch, "E1291", {"start": v(-38.1, 11.28) * mm, "mid": v(-37.78, 11.43) * mm, "end": v(-37.51, 11.65) * mm});
            skArc(sketch, "E1292", {"start": v(-37.51, 11.65) * mm, "mid": v(-37.34, 11.86) * mm, "end": v(-37.2, 12.1) * mm});
            skArc(sketch, "E1293", {"start": v(-37.2, 12.1) * mm, "mid": v(-37.07, 12.38) * mm, "end": v(-36.98, 12.67) * mm});
            skArc(sketch, "E1294", {"start": v(-36.98, 12.67) * mm, "mid": v(-36.89, 13.08) * mm, "end": v(-36.82, 13.5) * mm});
            skArc(sketch, "E1295", {"start": v(-36.82, 13.5) * mm, "mid": v(-36.75, 14.14) * mm, "end": v(-36.7, 14.79) * mm});
            skArc(sketch, "E1296", {"start": v(-36.7, 14.79) * mm, "mid": v(-36.66, 15.2) * mm, "end": v(-36.62, 15.62) * mm});
            skArc(sketch, "E1297", {"start": v(-36.62, 15.62) * mm, "mid": v(-36.58, 15.96) * mm, "end": v(-36.54, 16.3) * mm});
            skArc(sketch, "E1298", {"start": v(-36.54, 16.3) * mm, "mid": v(-36.5, 16.56) * mm, "end": v(-36.46, 16.82) * mm});
            skArc(sketch, "E1299", {"start": v(-36.46, 16.82) * mm, "mid": v(-36.44, 16.9) * mm, "end": v(-36.4, 16.99) * mm});
            skArc(sketch, "E1300", {"start": v(-36.4, 16.99) * mm, "mid": v(-36.37, 17.01) * mm, "end": v(-36.34, 17.03) * mm});
            skArc(sketch, "E1301", {"start": v(-36.34, 17.03) * mm, "mid": v(-36.3, 17.03) * mm, "end": v(-36.27, 17.02) * mm});
            skArc(sketch, "E1302", {"start": v(-36.27, 17.02) * mm, "mid": v(-36.22, 16.98) * mm, "end": v(-36.18, 16.94) * mm});
            skArc(sketch, "E1303", {"start": v(-36.18, 16.94) * mm, "mid": v(-36.1, 16.86) * mm, "end": v(-36.04, 16.78) * mm});
            skArc(sketch, "E1304", {"start": v(3.17, 10.55) * mm, "mid": v(3.37, 10.29) * mm, "end": v(3.5, 9.99) * mm});
            skArc(sketch, "E1305", {"start": v(3.5, 9.99) * mm, "mid": v(3.66, 9.48) * mm, "end": v(3.77, 8.96) * mm});
            skArc(sketch, "E1306", {"start": v(3.77, 8.96) * mm, "mid": v(3.86, 8.44) * mm, "end": v(3.9, 7.9) * mm});
            skArc(sketch, "E1307", {"start": v(3.9, 7.9) * mm, "mid": v(3.9, 7.59) * mm, "end": v(3.8, 7.28) * mm});
            skArc(sketch, "E1308", {"start": v(3.8, 7.28) * mm, "mid": v(3.67, 7.1) * mm, "end": v(3.5, 7) * mm});
            skArc(sketch, "E1309", {"start": v(3.5, 7) * mm, "mid": v(3.2, 6.9) * mm, "end": v(2.88, 6.84) * mm});
            skArc(sketch, "E1310", {"start": v(2.88, 6.84) * mm, "mid": v(2.56, 6.82) * mm, "end": v(2.24, 6.84) * mm});
            skArc(sketch, "E1311", {"start": v(2.24, 6.84) * mm, "mid": v(2.02, 6.9) * mm, "end": v(1.84, 7.03) * mm});
            skArc(sketch, "E1312", {"start": v(1.84, 7.03) * mm, "mid": v(1.75, 7.17) * mm, "end": v(1.7, 7.33) * mm});
            skArc(sketch, "E1313", {"start": v(1.7, 7.33) * mm, "mid": v(1.7, 7.67) * mm, "end": v(1.7, 8) * mm});
            skArc(sketch, "E1314", {"start": v(1.7, 8) * mm, "mid": v(1.73, 8.43) * mm, "end": v(1.79, 8.85) * mm});
            skArc(sketch, "E1315", {"start": v(1.79, 8.85) * mm, "mid": v(1.86, 9.31) * mm, "end": v(1.96, 9.77) * mm});
            skArc(sketch, "E1316", {"start": v(1.96, 9.77) * mm, "mid": v(2.04, 10.06) * mm, "end": v(2.16, 10.33) * mm});
            skArc(sketch, "E1317", {"start": v(2.16, 10.33) * mm, "mid": v(2.3, 10.52) * mm, "end": v(2.47, 10.67) * mm});
            skArc(sketch, "E1318", {"start": v(2.47, 10.67) * mm, "mid": v(2.64, 10.73) * mm, "end": v(2.82, 10.73) * mm});
            skArc(sketch, "E1319", {"start": v(2.82, 10.73) * mm, "mid": v(3, 10.67) * mm, "end": v(3.17, 10.55) * mm});
            skArc(sketch, "E1320", {"start": v(18.26, 19.56) * mm, "mid": v(17.9, 19.54) * mm, "end": v(17.55, 19.5) * mm});
            skArc(sketch, "E1321", {"start": v(17.55, 19.5) * mm, "mid": v(17.27, 19.48) * mm, "end": v(17, 19.44) * mm});
            skArc(sketch, "E1322", {"start": v(17, 19.44) * mm, "mid": v(16.76, 19.4) * mm, "end": v(16.52, 19.34) * mm});
            skArc(sketch, "E1323", {"start": v(16.52, 19.34) * mm, "mid": v(16.3, 19.28) * mm, "end": v(16.09, 19.2) * mm});
            skArc(sketch, "E1324", {"start": v(16.09, 19.2) * mm, "mid": v(15.75, 19.03) * mm, "end": v(15.47, 18.78) * mm});
            skArc(sketch, "E1325", {"start": v(15.47, 18.78) * mm, "mid": v(15.24, 18.44) * mm, "end": v(15.06, 18.06) * mm});
            skArc(sketch, "E1326", {"start": v(15.06, 18.06) * mm, "mid": v(14.92, 17.53) * mm, "end": v(14.84, 16.97) * mm});
            skArc(sketch, "E1327", {"start": v(14.84, 16.97) * mm, "mid": v(14.79, 16.17) * mm, "end": v(14.77, 15.36) * mm});
            skArc(sketch, "E1328", {"start": v(14.77, 15.36) * mm, "mid": v(14.79, 14.61) * mm, "end": v(14.83, 13.87) * mm});
            skArc(sketch, "E1329", {"start": v(14.83, 13.87) * mm, "mid": v(14.9, 13.31) * mm, "end": v(15.02, 12.77) * mm});
            skArc(sketch, "E1330", {"start": v(15.02, 12.77) * mm, "mid": v(15.16, 12.38) * mm, "end": v(15.34, 12) * mm});
            skArc(sketch, "E1331", {"start": v(15.34, 12) * mm, "mid": v(15.53, 11.76) * mm, "end": v(15.8, 11.57) * mm});
            skArc(sketch, "E1332", {"start": v(15.8, 11.57) * mm, "mid": v(15.97, 11.5) * mm, "end": v(16.15, 11.45) * mm});
            skArc(sketch, "E1333", {"start": v(16.15, 11.45) * mm, "mid": v(16.48, 11.4) * mm, "end": v(16.8, 11.37) * mm});
            skArc(sketch, "E1334", {"start": v(16.8, 11.37) * mm, "mid": v(17.3, 11.33) * mm, "end": v(17.8, 11.3) * mm});
            skArc(sketch, "E1335", {"start": v(17.8, 11.3) * mm, "mid": v(18.64, 11.26) * mm, "end": v(19.49, 11.23) * mm});
            skArc(sketch, "E1336", {"start": v(19.49, 11.23) * mm, "mid": v(20.47, 11.19) * mm, "end": v(21.46, 11.14) * mm});
            skArc(sketch, "E1337", {"start": v(21.46, 11.14) * mm, "mid": v(21.95, 11.1) * mm, "end": v(22.44, 11.04) * mm});
            skArc(sketch, "E1338", {"start": v(22.44, 11.04) * mm, "mid": v(22.72, 10.97) * mm, "end": v(23, 10.88) * mm});
            skArc(sketch, "E1339", {"start": v(23, 10.88) * mm, "mid": v(23.15, 10.77) * mm, "end": v(23.26, 10.61) * mm});
            skArc(sketch, "E1340", {"start": v(23.26, 10.61) * mm, "mid": v(23.38, 10.28) * mm, "end": v(23.42, 9.92) * mm});
            skArc(sketch, "E1341", {"start": v(23.42, 9.92) * mm, "mid": v(23.44, 8.7) * mm, "end": v(23.46, 7.49) * mm});
            skArc(sketch, "E1342", {"start": v(23.46, 7.49) * mm, "mid": v(23.46, 5.63) * mm, "end": v(23.44, 3.77) * mm});
            skArc(sketch, "E1343", {"start": v(23.44, 3.77) * mm, "mid": v(23.39, 0.47) * mm, "end": v(23.33, -2.83) * mm});
            skLineSegment(sketch, "E1344", {"start": v(23.33, -2.83) * mm, "end": v(23.26, -6.63) * mm});
            skLineSegment(sketch, "E1345", {"start": v(23.26, -6.63) * mm, "end": v(23.98, -7.4) * mm});
            skLineSegment(sketch, "E1346", {"start": v(23.98, -7.4) * mm, "end": v(24.7, -8.16) * mm});
            skLineSegment(sketch, "E1347", {"start": v(24.7, -8.16) * mm, "end": v(28, -8.16) * mm});
            skLineSegment(sketch, "E1348", {"start": v(28, -8.16) * mm, "end": v(31.28, -8.16) * mm});
            skLineSegment(sketch, "E1349", {"start": v(31.28, -8.16) * mm, "end": v(32.03, -7.4) * mm});
            skLineSegment(sketch, "E1350", {"start": v(32.03, -7.4) * mm, "end": v(32.77, -6.66) * mm});
            skLineSegment(sketch, "E1351", {"start": v(32.77, -6.66) * mm, "end": v(32.67, -1.97) * mm});
            skArc(sketch, "E1352", {"start": v(32.67, -1.97) * mm, "mid": v(32.63, 0.35) * mm, "end": v(32.6, 2.66) * mm});
            skArc(sketch, "E1353", {"start": v(32.6, 2.66) * mm, "mid": v(32.57, 4.62) * mm, "end": v(32.56, 6.58) * mm});
            skArc(sketch, "E1354", {"start": v(32.56, 6.58) * mm, "mid": v(32.55, 8.24) * mm, "end": v(32.55, 9.9) * mm});
            skArc(sketch, "E1355", {"start": v(32.55, 9.9) * mm, "mid": v(32.57, 10.18) * mm, "end": v(32.63, 10.44) * mm});
            skArc(sketch, "E1356", {"start": v(32.63, 10.44) * mm, "mid": v(32.73, 10.64) * mm, "end": v(32.89, 10.78) * mm});
            skArc(sketch, "E1357", {"start": v(32.89, 10.78) * mm, "mid": v(33.13, 10.91) * mm, "end": v(33.4, 11) * mm});
            skArc(sketch, "E1358", {"start": v(33.4, 11) * mm, "mid": v(33.87, 11.07) * mm, "end": v(34.34, 11.12) * mm});
            skArc(sketch, "E1359", {"start": v(34.34, 11.12) * mm, "mid": v(35.35, 11.18) * mm, "end": v(36.36, 11.23) * mm});
            skArc(sketch, "E1360", {"start": v(36.36, 11.23) * mm, "mid": v(36.93, 11.26) * mm, "end": v(37.5, 11.29) * mm});
            skArc(sketch, "E1361", {"start": v(37.5, 11.29) * mm, "mid": v(38, 11.32) * mm, "end": v(38.5, 11.35) * mm});
            skArc(sketch, "E1362", {"start": v(38.5, 11.35) * mm, "mid": v(38.93, 11.38) * mm, "end": v(39.34, 11.42) * mm});
            skArc(sketch, "E1363", {"start": v(39.34, 11.42) * mm, "mid": v(39.63, 11.45) * mm, "end": v(39.91, 11.48) * mm});
            skArc(sketch, "E1364", {"start": v(39.91, 11.48) * mm, "mid": v(40.16, 11.55) * mm, "end": v(40.37, 11.69) * mm});
            skArc(sketch, "E1365", {"start": v(40.37, 11.69) * mm, "mid": v(40.56, 11.88) * mm, "end": v(40.7, 12.12) * mm});
            skArc(sketch, "E1366", {"start": v(40.7, 12.12) * mm, "mid": v(40.83, 12.47) * mm, "end": v(40.92, 12.84) * mm});
            skArc(sketch, "E1367", {"start": v(40.92, 12.84) * mm, "mid": v(41, 13.4) * mm, "end": v(41.05, 13.98) * mm});
            skArc(sketch, "E1368", {"start": v(41.05, 13.98) * mm, "mid": v(41.1, 14.68) * mm, "end": v(41.1, 15.39) * mm});
            skArc(sketch, "E1369", {"start": v(41.1, 15.39) * mm, "mid": v(41.1, 16.06) * mm, "end": v(41.05, 16.74) * mm});
            skArc(sketch, "E1370", {"start": v(41.05, 16.74) * mm, "mid": v(40.99, 17.31) * mm, "end": v(40.9, 17.89) * mm});
            skArc(sketch, "E1371", {"start": v(40.9, 17.89) * mm, "mid": v(40.8, 18.26) * mm, "end": v(40.66, 18.63) * mm});
            skArc(sketch, "E1372", {"start": v(40.66, 18.63) * mm, "mid": v(40.54, 18.83) * mm, "end": v(40.4, 19.03) * mm});
            skArc(sketch, "E1373", {"start": v(40.4, 19.03) * mm, "mid": v(40.26, 19.15) * mm, "end": v(40.1, 19.24) * mm});
            skArc(sketch, "E1374", {"start": v(40.1, 19.24) * mm, "mid": v(39.87, 19.31) * mm, "end": v(39.63, 19.35) * mm});
            skArc(sketch, "E1375", {"start": v(39.63, 19.35) * mm, "mid": v(39.1, 19.39) * mm, "end": v(38.59, 19.42) * mm});
            skArc(sketch, "E1376", {"start": v(38.59, 19.42) * mm, "mid": v(36.77, 19.5) * mm, "end": v(34.94, 19.53) * mm});
            skArc(sketch, "E1377", {"start": v(34.94, 19.53) * mm, "mid": v(31.5, 19.57) * mm, "end": v(28.07, 19.6) * mm});
            skArc(sketch, "E1378", {"start": v(28.07, 19.6) * mm, "mid": v(24.61, 19.62) * mm, "end": v(21.16, 19.63) * mm});
            skArc(sketch, "E1379", {"start": v(21.16, 19.63) * mm, "mid": v(19.7, 19.61) * mm, "end": v(18.26, 19.56) * mm});
            skArc(sketch, "E1380", {"start": v(70.9, 19.56) * mm, "mid": v(68.82, 19.51) * mm, "end": v(66.75, 19.46) * mm});
            skArc(sketch, "E1381", {"start": v(66.75, 19.46) * mm, "mid": v(65.13, 19.4) * mm, "end": v(63.52, 19.35) * mm});
            skArc(sketch, "E1382", {"start": v(63.52, 19.35) * mm, "mid": v(62.24, 19.3) * mm, "end": v(60.95, 19.24) * mm});
            skArc(sketch, "E1383", {"start": v(60.95, 19.24) * mm, "mid": v(60.7, 19.2) * mm, "end": v(60.45, 19.13) * mm});
            skArc(sketch, "E1384", {"start": v(60.45, 19.13) * mm, "mid": v(60.35, 19.09) * mm, "end": v(60.26, 19.03) * mm});
            skArc(sketch, "E1385", {"start": v(60.26, 19.03) * mm, "mid": v(60.16, 18.96) * mm, "end": v(60.07, 18.87) * mm});
            skArc(sketch, "E1386", {"start": v(60.07, 18.87) * mm, "mid": v(59.97, 18.78) * mm, "end": v(59.89, 18.68) * mm});
            skArc(sketch, "E1387", {"start": v(59.89, 18.68) * mm, "mid": v(59.82, 18.59) * mm, "end": v(59.76, 18.49) * mm});
            skArc(sketch, "E1388", {"start": v(59.76, 18.49) * mm, "mid": v(59.7, 18.33) * mm, "end": v(59.64, 18.17) * mm});
            skArc(sketch, "E1389", {"start": v(59.64, 18.17) * mm, "mid": v(59.59, 17.9) * mm, "end": v(59.54, 17.63) * mm});
            skArc(sketch, "E1390", {"start": v(59.54, 17.63) * mm, "mid": v(59.5, 17.3) * mm, "end": v(59.45, 16.95) * mm});
            skArc(sketch, "E1391", {"start": v(59.45, 16.95) * mm, "mid": v(59.42, 16.53) * mm, "end": v(59.39, 16.1) * mm});
            skArc(sketch, "E1392", {"start": v(59.39, 16.1) * mm, "mid": v(59.36, 15.55) * mm, "end": v(59.33, 14.98) * mm});
            skArc(sketch, "E1393", {"start": v(59.33, 14.98) * mm, "mid": v(59.3, 13.83) * mm, "end": v(59.26, 12.68) * mm});
            skArc(sketch, "E1394", {"start": v(59.26, 12.68) * mm, "mid": v(59.22, 11.52) * mm, "end": v(59.2, 10.37) * mm});
            skArc(sketch, "E1395", {"start": v(59.2, 10.37) * mm, "mid": v(59.18, 9.82) * mm, "end": v(59.18, 9.26) * mm});
            skLineSegment(sketch, "E1396", {"start": v(59.18, 9.26) * mm, "end": v(59.18, 8.83) * mm});
            skLineSegment(sketch, "E1397", {"start": v(59.18, 8.83) * mm, "end": v(52.44, 8.88) * mm});
            skArc(sketch, "E1398", {"start": v(52.44, 8.88) * mm, "mid": v(49.76, 8.9) * mm, "end": v(47.08, 8.9) * mm});
            skArc(sketch, "E1399", {"start": v(47.08, 8.9) * mm, "mid": v(45.72, 8.9) * mm, "end": v(44.36, 8.86) * mm});
            skArc(sketch, "E1400", {"start": v(44.36, 8.86) * mm, "mid": v(43.54, 8.81) * mm, "end": v(42.72, 8.74) * mm});
            skArc(sketch, "E1401", {"start": v(42.72, 8.74) * mm, "mid": v(42.29, 8.66) * mm, "end": v(41.87, 8.5) * mm});
            skArc(sketch, "E1402", {"start": v(41.87, 8.5) * mm, "mid": v(41.62, 8.32) * mm, "end": v(41.42, 8.08) * mm});
            skArc(sketch, "E1403", {"start": v(41.42, 8.08) * mm, "mid": v(41.24, 7.75) * mm, "end": v(41.12, 7.4) * mm});
            skArc(sketch, "E1404", {"start": v(41.12, 7.4) * mm, "mid": v(41, 6.9) * mm, "end": v(40.95, 6.38) * mm});
            skArc(sketch, "E1405", {"start": v(40.95, 6.38) * mm, "mid": v(40.9, 5.64) * mm, "end": v(40.9, 4.9) * mm});
            skArc(sketch, "E1406", {"start": v(40.9, 4.9) * mm, "mid": v(40.9, 4.28) * mm, "end": v(40.94, 3.68) * mm});
            skArc(sketch, "E1407", {"start": v(40.94, 3.68) * mm, "mid": v(40.98, 3.2) * mm, "end": v(41.06, 2.72) * mm});
            skArc(sketch, "E1408", {"start": v(41.06, 2.72) * mm, "mid": v(41.15, 2.36) * mm, "end": v(41.26, 2.01) * mm});
            skArc(sketch, "E1409", {"start": v(41.26, 2.01) * mm, "mid": v(41.38, 1.78) * mm, "end": v(41.54, 1.57) * mm});
            skArc(sketch, "E1410", {"start": v(41.54, 1.57) * mm, "mid": v(41.83, 1.36) * mm, "end": v(42.17, 1.24) * mm});
            skArc(sketch, "E1411", {"start": v(42.17, 1.24) * mm, "mid": v(42.77, 1.14) * mm, "end": v(43.37, 1.09) * mm});
            skArc(sketch, "E1412", {"start": v(43.37, 1.09) * mm, "mid": v(44.49, 1.04) * mm, "end": v(45.6, 1.02) * mm});
            skArc(sketch, "E1413", {"start": v(45.6, 1.02) * mm, "mid": v(48.57, 1.01) * mm, "end": v(51.53, 1) * mm});
            skLineSegment(sketch, "E1414", {"start": v(51.53, 1) * mm, "end": v(59.18, 1) * mm});
            skLineSegment(sketch, "E1415", {"start": v(59.18, 1) * mm, "end": v(59.18, 0.71) * mm});
            skArc(sketch, "E1416", {"start": v(59.18, 0.71) * mm, "mid": v(59.18, 0) * mm, "end": v(59.2, -0.73) * mm});
            skArc(sketch, "E1417", {"start": v(59.2, -0.73) * mm, "mid": v(59.27, -2.03) * mm, "end": v(59.33, -3.32) * mm});
            skArc(sketch, "E1418", {"start": v(59.33, -3.32) * mm, "mid": v(59.4, -4.65) * mm, "end": v(59.47, -5.97) * mm});
            skArc(sketch, "E1419", {"start": v(59.47, -5.97) * mm, "mid": v(59.5, -6.4) * mm, "end": v(59.56, -6.84) * mm});
            skArc(sketch, "E1420", {"start": v(59.56, -6.84) * mm, "mid": v(59.6, -6.96) * mm, "end": v(59.65, -7.07) * mm});
            skArc(sketch, "E1421", {"start": v(59.65, -7.07) * mm, "mid": v(59.74, -7.2) * mm, "end": v(59.84, -7.33) * mm});
            skArc(sketch, "E1422", {"start": v(59.84, -7.33) * mm, "mid": v(59.96, -7.45) * mm, "end": v(60.1, -7.56) * mm});
            skArc(sketch, "E1423", {"start": v(60.1, -7.56) * mm, "mid": v(60.23, -7.66) * mm, "end": v(60.37, -7.74) * mm});
            skArc(sketch, "E1424", {"start": v(60.37, -7.74) * mm, "mid": v(60.72, -7.89) * mm, "end": v(61.09, -7.97) * mm});
            skArc(sketch, "E1425", {"start": v(61.09, -7.97) * mm, "mid": v(61.78, -8.05) * mm, "end": v(62.48, -8.1) * mm});
            skArc(sketch, "E1426", {"start": v(62.48, -8.1) * mm, "mid": v(63.28, -8.14) * mm, "end": v(64.07, -8.16) * mm});
            skArc(sketch, "E1427", {"start": v(64.07, -8.16) * mm, "mid": v(64.83, -8.14) * mm, "end": v(65.6, -8.1) * mm});
            skArc(sketch, "E1428", {"start": v(65.6, -8.1) * mm, "mid": v(66.25, -8.03) * mm, "end": v(66.9, -7.94) * mm});
            skArc(sketch, "E1429", {"start": v(66.9, -7.94) * mm, "mid": v(67.27, -7.85) * mm, "end": v(67.62, -7.7) * mm});
            skArc(sketch, "E1430", {"start": v(67.62, -7.7) * mm, "mid": v(67.86, -7.51) * mm, "end": v(68.04, -7.27) * mm});
            skArc(sketch, "E1431", {"start": v(68.04, -7.27) * mm, "mid": v(68.19, -6.95) * mm, "end": v(68.28, -6.6) * mm});
            skArc(sketch, "E1432", {"start": v(68.28, -6.6) * mm, "mid": v(68.3, -6.48) * mm, "end": v(68.3, -6.36) * mm});
            skArc(sketch, "E1433", {"start": v(68.3, -6.36) * mm, "mid": v(68.32, -6) * mm, "end": v(68.34, -5.63) * mm});
            skArc(sketch, "E1434", {"start": v(68.34, -5.63) * mm, "mid": v(68.36, -5.2) * mm, "end": v(68.38, -4.77) * mm});
            skArc(sketch, "E1435", {"start": v(68.38, -4.77) * mm, "mid": v(68.4, -4.3) * mm, "end": v(68.41, -3.82) * mm});
            skArc(sketch, "E1436", {"start": v(68.41, -3.82) * mm, "mid": v(68.45, -2.65) * mm, "end": v(68.49, -1.48) * mm});
            skArc(sketch, "E1437", {"start": v(68.49, -1.48) * mm, "mid": v(68.52, -0.9) * mm, "end": v(68.56, -0.3) * mm});
            skArc(sketch, "E1438", {"start": v(68.56, -0.3) * mm, "mid": v(68.6, 0.05) * mm, "end": v(68.65, 0.4) * mm});
            skArc(sketch, "E1439", {"start": v(68.65, 0.4) * mm, "mid": v(68.7, 0.55) * mm, "end": v(68.81, 0.67) * mm});
            skArc(sketch, "E1440", {"start": v(68.81, 0.67) * mm, "mid": v(68.93, 0.74) * mm, "end": v(69.07, 0.78) * mm});
            skArc(sketch, "E1441", {"start": v(69.07, 0.78) * mm, "mid": v(69.4, 0.81) * mm, "end": v(69.75, 0.84) * mm});
            skArc(sketch, "E1442", {"start": v(69.75, 0.84) * mm, "mid": v(70.32, 0.87) * mm, "end": v(70.9, 0.88) * mm});
            skArc(sketch, "E1443", {"start": v(70.9, 0.88) * mm, "mid": v(72.09, 0.91) * mm, "end": v(73.28, 0.93) * mm});
            skArc(sketch, "E1444", {"start": v(73.28, 0.93) * mm, "mid": v(74.05, 0.95) * mm, "end": v(74.83, 0.97) * mm});
            skArc(sketch, "E1445", {"start": v(74.83, 0.97) * mm, "mid": v(75.44, 0.98) * mm, "end": v(76.05, 1) * mm});
            skArc(sketch, "E1446", {"start": v(76.05, 1) * mm, "mid": v(76.53, 1.02) * mm, "end": v(77, 1.04) * mm});
            skArc(sketch, "E1447", {"start": v(77, 1.04) * mm, "mid": v(77.15, 1.06) * mm, "end": v(77.3, 1.08) * mm});
            skArc(sketch, "E1448", {"start": v(77.3, 1.08) * mm, "mid": v(77.54, 1.16) * mm, "end": v(77.77, 1.28) * mm});
            skArc(sketch, "E1449", {"start": v(77.77, 1.28) * mm, "mid": v(77.98, 1.44) * mm, "end": v(78.15, 1.64) * mm});
            skArc(sketch, "E1450", {"start": v(78.15, 1.64) * mm, "mid": v(78.32, 1.9) * mm, "end": v(78.45, 2.18) * mm});
            skArc(sketch, "E1451", {"start": v(78.45, 2.18) * mm, "mid": v(78.58, 2.55) * mm, "end": v(78.68, 2.93) * mm});
            skArc(sketch, "E1452", {"start": v(78.68, 2.93) * mm, "mid": v(78.75, 3.32) * mm, "end": v(78.79, 3.71) * mm});
            skArc(sketch, "E1453", {"start": v(78.79, 3.71) * mm, "mid": v(78.81, 4.35) * mm, "end": v(78.82, 4.98) * mm});
            skArc(sketch, "E1454", {"start": v(78.82, 4.98) * mm, "mid": v(78.81, 5.63) * mm, "end": v(78.79, 6.27) * mm});
            skArc(sketch, "E1455", {"start": v(78.79, 6.27) * mm, "mid": v(78.75, 6.7) * mm, "end": v(78.68, 7.13) * mm});
            skArc(sketch, "E1456", {"start": v(78.68, 7.13) * mm, "mid": v(78.5, 7.74) * mm, "end": v(78.24, 8.31) * mm});
            skArc(sketch, "E1457", {"start": v(78.24, 8.31) * mm, "mid": v(77.92, 8.7) * mm, "end": v(77.5, 8.95) * mm});
            skArc(sketch, "E1458", {"start": v(77.5, 8.95) * mm, "mid": v(76.84, 9.15) * mm, "end": v(76.17, 9.23) * mm});
            skArc(sketch, "E1459", {"start": v(76.17, 9.23) * mm, "mid": v(74.8, 9.24) * mm, "end": v(73.42, 9.23) * mm});
            skArc(sketch, "E1460", {"start": v(73.42, 9.23) * mm, "mid": v(72.48, 9.2) * mm, "end": v(71.54, 9.18) * mm});
            skArc(sketch, "E1461", {"start": v(71.54, 9.18) * mm, "mid": v(70.9, 9.17) * mm, "end": v(70.25, 9.17) * mm});
            skArc(sketch, "E1462", {"start": v(70.25, 9.17) * mm, "mid": v(69.8, 9.18) * mm, "end": v(69.34, 9.2) * mm});
            skArc(sketch, "E1463", {"start": v(69.34, 9.2) * mm, "mid": v(69.18, 9.21) * mm, "end": v(69.03, 9.26) * mm});
            skArc(sketch, "E1464", {"start": v(69.03, 9.26) * mm, "mid": v(68.93, 9.3) * mm, "end": v(68.85, 9.38) * mm});
            skArc(sketch, "E1465", {"start": v(68.85, 9.38) * mm, "mid": v(68.76, 9.47) * mm, "end": v(68.7, 9.58) * mm});
            skArc(sketch, "E1466", {"start": v(68.7, 9.58) * mm, "mid": v(68.63, 9.7) * mm, "end": v(68.6, 9.83) * mm});
            skArc(sketch, "E1467", {"start": v(68.6, 9.83) * mm, "mid": v(68.56, 9.95) * mm, "end": v(68.56, 10.09) * mm});
            skArc(sketch, "E1468", {"start": v(68.56, 10.09) * mm, "mid": v(68.57, 10.22) * mm, "end": v(68.6, 10.35) * mm});
            skArc(sketch, "E1469", {"start": v(68.6, 10.35) * mm, "mid": v(68.65, 10.47) * mm, "end": v(68.73, 10.58) * mm});
            skArc(sketch, "E1470", {"start": v(68.73, 10.58) * mm, "mid": v(68.82, 10.68) * mm, "end": v(68.92, 10.76) * mm});
            skArc(sketch, "E1471", {"start": v(68.92, 10.76) * mm, "mid": v(69.04, 10.83) * mm, "end": v(69.17, 10.88) * mm});
            skArc(sketch, "E1472", {"start": v(69.17, 10.88) * mm, "mid": v(69.28, 10.9) * mm, "end": v(69.4, 10.9) * mm});
            skArc(sketch, "E1473", {"start": v(69.4, 10.9) * mm, "mid": v(70.04, 10.92) * mm, "end": v(70.68, 10.93) * mm});
            skArc(sketch, "E1474", {"start": v(70.68, 10.93) * mm, "mid": v(71.5, 10.94) * mm, "end": v(72.32, 10.94) * mm});
            skArc(sketch, "E1475", {"start": v(72.32, 10.94) * mm, "mid": v(73.41, 10.95) * mm, "end": v(74.5, 10.95) * mm});
            skArc(sketch, "E1476", {"start": v(74.5, 10.95) * mm, "mid": v(75.5, 10.95) * mm, "end": v(76.5, 10.95) * mm});
            skArc(sketch, "E1477", {"start": v(76.5, 10.95) * mm, "mid": v(77.39, 10.96) * mm, "end": v(78.27, 10.97) * mm});
            skArc(sketch, "E1478", {"start": v(78.27, 10.97) * mm, "mid": v(79.01, 10.98) * mm, "end": v(79.75, 11) * mm});
            skArc(sketch, "E1479", {"start": v(79.75, 11) * mm, "mid": v(79.96, 11) * mm, "end": v(80.17, 11.02) * mm});
            skArc(sketch, "E1480", {"start": v(80.17, 11.02) * mm, "mid": v(80.56, 11.07) * mm, "end": v(80.95, 11.16) * mm});
            skArc(sketch, "E1481", {"start": v(80.95, 11.16) * mm, "mid": v(81.2, 11.24) * mm, "end": v(81.43, 11.37) * mm});
            skArc(sketch, "E1482", {"start": v(81.43, 11.37) * mm, "mid": v(81.6, 11.53) * mm, "end": v(81.75, 11.72) * mm});
            skArc(sketch, "E1483", {"start": v(81.75, 11.72) * mm, "mid": v(81.88, 12) * mm, "end": v(81.97, 12.27) * mm});
            skArc(sketch, "E1484", {"start": v(81.97, 12.27) * mm, "mid": v(82.01, 12.44) * mm, "end": v(82.04, 12.61) * mm});
            skArc(sketch, "E1485", {"start": v(82.04, 12.61) * mm, "mid": v(82.06, 12.82) * mm, "end": v(82.08, 13.03) * mm});
            skArc(sketch, "E1486", {"start": v(82.08, 13.03) * mm, "mid": v(82.1, 13.35) * mm, "end": v(82.1, 13.68) * mm});
            skArc(sketch, "E1487", {"start": v(82.1, 13.68) * mm, "mid": v(82.1, 14.3) * mm, "end": v(82.1, 14.9) * mm});
            skArc(sketch, "E1488", {"start": v(82.1, 14.9) * mm, "mid": v(82.09, 16.15) * mm, "end": v(82.04, 17.39) * mm});
            skArc(sketch, "E1489", {"start": v(82.04, 17.39) * mm, "mid": v(81.96, 17.96) * mm, "end": v(81.78, 18.51) * mm});
            skArc(sketch, "E1490", {"start": v(81.78, 18.51) * mm, "mid": v(81.54, 18.87) * mm, "end": v(81.2, 19.12) * mm});
            skArc(sketch, "E1491", {"start": v(81.2, 19.12) * mm, "mid": v(80.67, 19.33) * mm, "end": v(80.1, 19.47) * mm});
            skArc(sketch, "E1492", {"start": v(80.1, 19.47) * mm, "mid": v(79.65, 19.52) * mm, "end": v(79.18, 19.55) * mm});
            skArc(sketch, "E1493", {"start": v(79.18, 19.55) * mm, "mid": v(77.91, 19.57) * mm, "end": v(76.64, 19.59) * mm});
            skArc(sketch, "E1494", {"start": v(76.64, 19.59) * mm, "mid": v(75.2, 19.6) * mm, "end": v(73.77, 19.6) * mm});
            skArc(sketch, "E1495", {"start": v(73.77, 19.6) * mm, "mid": v(72.33, 19.58) * mm, "end": v(70.9, 19.56) * mm});
            skArc(sketch, "E1496", {"start": v(37.99, -13.94) * mm, "mid": v(37.96, -14.05) * mm, "end": v(37.97, -14.17) * mm});
            skArc(sketch, "E1497", {"start": v(37.97, -14.17) * mm, "mid": v(38.02, -14.33) * mm, "end": v(38.08, -14.48) * mm});
            skArc(sketch, "E1498", {"start": v(38.08, -14.48) * mm, "mid": v(38.16, -14.6) * mm, "end": v(38.25, -14.73) * mm});
            skArc(sketch, "E1499", {"start": v(38.25, -14.73) * mm, "mid": v(38.33, -14.79) * mm, "end": v(38.43, -14.81) * mm});
            skArc(sketch, "E1500", {"start": v(38.43, -14.81) * mm, "mid": v(38.5, -14.79) * mm, "end": v(38.57, -14.73) * mm});
            skArc(sketch, "E1501", {"start": v(38.57, -14.73) * mm, "mid": v(38.6, -14.62) * mm, "end": v(38.6, -14.52) * mm});
            skArc(sketch, "E1502", {"start": v(38.6, -14.52) * mm, "mid": v(38.59, -14.37) * mm, "end": v(38.54, -14.24) * mm});
            skArc(sketch, "E1503", {"start": v(38.54, -14.24) * mm, "mid": v(38.47, -14.11) * mm, "end": v(38.37, -14) * mm});
            skArc(sketch, "E1504", {"start": v(38.37, -14) * mm, "mid": v(38.31, -13.94) * mm, "end": v(38.25, -13.88) * mm});
            skArc(sketch, "E1505", {"start": v(38.25, -13.88) * mm, "mid": v(38.2, -13.85) * mm, "end": v(38.14, -13.84) * mm});
            skArc(sketch, "E1506", {"start": v(38.14, -13.84) * mm, "mid": v(38.1, -13.84) * mm, "end": v(38.05, -13.86) * mm});
            skArc(sketch, "E1507", {"start": v(38.05, -13.86) * mm, "mid": v(38.01, -13.9) * mm, "end": v(37.99, -13.94) * mm});
            skArc(sketch, "E1508", {"start": v(37.07, -14.12) * mm, "mid": v(37.05, -14.15) * mm, "end": v(37.04, -14.17) * mm});
            skArc(sketch, "E1509", {"start": v(37.04, -14.17) * mm, "mid": v(37.02, -14.2) * mm, "end": v(37, -14.23) * mm});
            skArc(sketch, "E1510", {"start": v(37, -14.23) * mm, "mid": v(37, -14.26) * mm, "end": v(37, -14.3) * mm});
            skArc(sketch, "E1511", {"start": v(37, -14.3) * mm, "mid": v(36.99, -14.33) * mm, "end": v(36.99, -14.36) * mm});
            skArc(sketch, "E1512", {"start": v(36.99, -14.36) * mm, "mid": v(36.96, -14.44) * mm, "end": v(36.9, -14.5) * mm});
            skArc(sketch, "E1513", {"start": v(36.9, -14.5) * mm, "mid": v(36.76, -14.54) * mm, "end": v(36.62, -14.57) * mm});
            skArc(sketch, "E1514", {"start": v(36.62, -14.57) * mm, "mid": v(36.34, -14.6) * mm, "end": v(36.06, -14.62) * mm});
            skArc(sketch, "E1515", {"start": v(36.06, -14.62) * mm, "mid": v(35.35, -14.64) * mm, "end": v(34.65, -14.67) * mm});
            skArc(sketch, "E1516", {"start": v(34.65, -14.67) * mm, "mid": v(34.05, -14.7) * mm, "end": v(33.46, -14.72) * mm});
            skArc(sketch, "E1517", {"start": v(33.46, -14.72) * mm, "mid": v(33.13, -14.74) * mm, "end": v(32.8, -14.78) * mm});
            skArc(sketch, "E1518", {"start": v(32.8, -14.78) * mm, "mid": v(32.66, -14.8) * mm, "end": v(32.53, -14.86) * mm});
            skArc(sketch, "E1519", {"start": v(32.53, -14.86) * mm, "mid": v(32.5, -14.91) * mm, "end": v(32.53, -14.96) * mm});
            skArc(sketch, "E1520", {"start": v(32.53, -14.96) * mm, "mid": v(32.65, -15.01) * mm, "end": v(32.78, -15.04) * mm});
            skArc(sketch, "E1521", {"start": v(32.78, -15.04) * mm, "mid": v(33.1, -15.07) * mm, "end": v(33.43, -15.1) * mm});
            skArc(sketch, "E1522", {"start": v(33.43, -15.1) * mm, "mid": v(33.83, -15.13) * mm, "end": v(34.24, -15.14) * mm});
            skArc(sketch, "E1523", {"start": v(34.24, -15.14) * mm, "mid": v(34.71, -15.15) * mm, "end": v(35.19, -15.16) * mm});
            skLineSegment(sketch, "E1524", {"start": v(35.19, -15.16) * mm, "end": v(36.44, -15.16) * mm});
            skLineSegment(sketch, "E1525", {"start": v(36.44, -15.16) * mm, "end": v(36.17, -15.63) * mm});
            skArc(sketch, "E1526", {"start": v(36.17, -15.63) * mm, "mid": v(35.91, -16.08) * mm, "end": v(35.62, -16.51) * mm});
            skArc(sketch, "E1527", {"start": v(35.62, -16.51) * mm, "mid": v(35.33, -16.9) * mm, "end": v(35.02, -17.26) * mm});
            skArc(sketch, "E1528", {"start": v(35.02, -17.26) * mm, "mid": v(34.67, -17.62) * mm, "end": v(34.3, -17.95) * mm});
            skArc(sketch, "E1529", {"start": v(34.3, -17.95) * mm, "mid": v(33.84, -18.31) * mm, "end": v(33.38, -18.66) * mm});
            skArc(sketch, "E1530", {"start": v(33.38, -18.66) * mm, "mid": v(33.02, -18.9) * mm, "end": v(32.67, -19.16) * mm});
            skArc(sketch, "E1531", {"start": v(32.67, -19.16) * mm, "mid": v(32.46, -19.32) * mm, "end": v(32.25, -19.48) * mm});
            skArc(sketch, "E1532", {"start": v(32.25, -19.48) * mm, "mid": v(32.12, -19.6) * mm, "end": v(32, -19.7) * mm});
            skArc(sketch, "E1533", {"start": v(32, -19.7) * mm, "mid": v(31.96, -19.76) * mm, "end": v(31.95, -19.82) * mm});
            skArc(sketch, "E1534", {"start": v(31.95, -19.82) * mm, "mid": v(32, -19.92) * mm, "end": v(32.1, -19.93) * mm});
            skArc(sketch, "E1535", {"start": v(32.1, -19.93) * mm, "mid": v(32.37, -19.83) * mm, "end": v(32.64, -19.7) * mm});
            skArc(sketch, "E1536", {"start": v(32.64, -19.7) * mm, "mid": v(33.03, -19.5) * mm, "end": v(33.4, -19.27) * mm});
            skArc(sketch, "E1537", {"start": v(33.4, -19.27) * mm, "mid": v(33.87, -18.95) * mm, "end": v(34.33, -18.63) * mm});
            skArc(sketch, "E1538", {"start": v(34.33, -18.63) * mm, "mid": v(34.62, -18.41) * mm, "end": v(34.92, -18.2) * mm});
            skArc(sketch, "E1539", {"start": v(34.92, -18.2) * mm, "mid": v(35.05, -18.11) * mm, "end": v(35.2, -18.04) * mm});
            skArc(sketch, "E1540", {"start": v(35.2, -18.04) * mm, "mid": v(35.28, -18) * mm, "end": v(35.38, -18) * mm});
            skArc(sketch, "E1541", {"start": v(35.38, -18) * mm, "mid": v(35.47, -18) * mm, "end": v(35.55, -18.03) * mm});
            skArc(sketch, "E1542", {"start": v(35.55, -18.03) * mm, "mid": v(35.6, -18.06) * mm, "end": v(35.66, -18.1) * mm});
            skArc(sketch, "E1543", {"start": v(35.66, -18.1) * mm, "mid": v(35.79, -18.22) * mm, "end": v(35.92, -18.33) * mm});
            skArc(sketch, "E1544", {"start": v(35.92, -18.33) * mm, "mid": v(36.08, -18.47) * mm, "end": v(36.23, -18.6) * mm});
            skArc(sketch, "E1545", {"start": v(36.23, -18.6) * mm, "mid": v(36.4, -18.76) * mm, "end": v(36.57, -18.92) * mm});
            skArc(sketch, "E1546", {"start": v(36.57, -18.92) * mm, "mid": v(36.9, -19.23) * mm, "end": v(37.25, -19.53) * mm});
            skArc(sketch, "E1547", {"start": v(37.25, -19.53) * mm, "mid": v(37.45, -19.7) * mm, "end": v(37.67, -19.84) * mm});
            skArc(sketch, "E1548", {"start": v(37.67, -19.84) * mm, "mid": v(37.8, -19.9) * mm, "end": v(37.93, -19.91) * mm});
            skArc(sketch, "E1549", {"start": v(37.93, -19.91) * mm, "mid": v(38.02, -19.89) * mm, "end": v(38.08, -19.81) * mm});
            skArc(sketch, "E1550", {"start": v(38.08, -19.81) * mm, "mid": v(38.1, -19.72) * mm, "end": v(38.06, -19.63) * mm});
            skArc(sketch, "E1551", {"start": v(38.06, -19.63) * mm, "mid": v(37.95, -19.47) * mm, "end": v(37.83, -19.32) * mm});
            skArc(sketch, "E1552", {"start": v(37.83, -19.32) * mm, "mid": v(37.64, -19.11) * mm, "end": v(37.43, -18.92) * mm});
            skArc(sketch, "E1553", {"start": v(37.43, -18.92) * mm, "mid": v(37.13, -18.64) * mm, "end": v(36.82, -18.37) * mm});
            skArc(sketch, "E1554", {"start": v(36.82, -18.37) * mm, "mid": v(36.64, -18.22) * mm, "end": v(36.46, -18.06) * mm});
            skArc(sketch, "E1555", {"start": v(36.46, -18.06) * mm, "mid": v(36.3, -17.93) * mm, "end": v(36.14, -17.8) * mm});
            skArc(sketch, "E1556", {"start": v(36.14, -17.8) * mm, "mid": v(36, -17.67) * mm, "end": v(35.87, -17.56) * mm});
            skArc(sketch, "E1557", {"start": v(35.87, -17.56) * mm, "mid": v(35.84, -17.53) * mm, "end": v(35.8, -17.5) * mm});
            skArc(sketch, "E1558", {"start": v(35.8, -17.5) * mm, "mid": v(35.78, -17.46) * mm, "end": v(35.77, -17.42) * mm});
            skArc(sketch, "E1559", {"start": v(35.77, -17.42) * mm, "mid": v(35.78, -17.37) * mm, "end": v(35.8, -17.31) * mm});
            skArc(sketch, "E1560", {"start": v(35.8, -17.31) * mm, "mid": v(35.84, -17.22) * mm, "end": v(35.89, -17.13) * mm});
            skArc(sketch, "E1561", {"start": v(35.89, -17.13) * mm, "mid": v(36, -16.96) * mm, "end": v(36.1, -16.8) * mm});
            skArc(sketch, "E1562", {"start": v(36.1, -16.8) * mm, "mid": v(36.19, -16.66) * mm, "end": v(36.28, -16.52) * mm});
            skArc(sketch, "E1563", {"start": v(36.28, -16.52) * mm, "mid": v(36.38, -16.36) * mm, "end": v(36.48, -16.2) * mm});
            skArc(sketch, "E1564", {"start": v(36.48, -16.2) * mm, "mid": v(36.57, -16.03) * mm, "end": v(36.67, -15.88) * mm});
            skArc(sketch, "E1565", {"start": v(36.67, -15.88) * mm, "mid": v(36.75, -15.75) * mm, "end": v(36.83, -15.62) * mm});
            skArc(sketch, "E1566", {"start": v(36.83, -15.62) * mm, "mid": v(36.92, -15.46) * mm, "end": v(37.02, -15.3) * mm});
            skArc(sketch, "E1567", {"start": v(37.02, -15.3) * mm, "mid": v(37.08, -15.22) * mm, "end": v(37.15, -15.14) * mm});
            skArc(sketch, "E1568", {"start": v(37.15, -15.14) * mm, "mid": v(37.2, -15.09) * mm, "end": v(37.27, -15.05) * mm});
            skArc(sketch, "E1569", {"start": v(37.27, -15.05) * mm, "mid": v(37.36, -15) * mm, "end": v(37.44, -14.98) * mm});
            skArc(sketch, "E1570", {"start": v(37.44, -14.98) * mm, "mid": v(37.5, -14.96) * mm, "end": v(37.55, -14.95) * mm});
            skArc(sketch, "E1571", {"start": v(37.55, -14.95) * mm, "mid": v(37.6, -14.93) * mm, "end": v(37.64, -14.9) * mm});
            skArc(sketch, "E1572", {"start": v(37.64, -14.9) * mm, "mid": v(37.67, -14.88) * mm, "end": v(37.7, -14.86) * mm});
            skArc(sketch, "E1573", {"start": v(37.7, -14.86) * mm, "mid": v(37.71, -14.84) * mm, "end": v(37.71, -14.82) * mm});
            skArc(sketch, "E1574", {"start": v(37.71, -14.82) * mm, "mid": v(37.71, -14.8) * mm, "end": v(37.7, -14.78) * mm});
            skArc(sketch, "E1575", {"start": v(37.7, -14.78) * mm, "mid": v(37.7, -14.76) * mm, "end": v(37.7, -14.73) * mm});
            skArc(sketch, "E1576", {"start": v(37.7, -14.73) * mm, "mid": v(37.7, -14.7) * mm, "end": v(37.7, -14.68) * mm});
            skArc(sketch, "E1577", {"start": v(37.7, -14.68) * mm, "mid": v(37.7, -14.66) * mm, "end": v(37.7, -14.64) * mm});
            skArc(sketch, "E1578", {"start": v(37.7, -14.64) * mm, "mid": v(37.68, -14.58) * mm, "end": v(37.65, -14.53) * mm});
            skArc(sketch, "E1579", {"start": v(37.65, -14.53) * mm, "mid": v(37.56, -14.41) * mm, "end": v(37.47, -14.3) * mm});
            skArc(sketch, "E1580", {"start": v(37.47, -14.3) * mm, "mid": v(37.38, -14.19) * mm, "end": v(37.28, -14.08) * mm});
            skArc(sketch, "E1581", {"start": v(37.28, -14.08) * mm, "mid": v(37.25, -14.05) * mm, "end": v(37.2, -14.04) * mm});
            skArc(sketch, "E1582", {"start": v(37.2, -14.04) * mm, "mid": v(37.19, -14.04) * mm, "end": v(37.18, -14.05) * mm});
            skArc(sketch, "E1583", {"start": v(37.18, -14.05) * mm, "mid": v(37.16, -14.06) * mm, "end": v(37.14, -14.07) * mm});
            skArc(sketch, "E1584", {"start": v(37.14, -14.07) * mm, "mid": v(37.12, -14.08) * mm, "end": v(37.1, -14.1) * mm});
            skArc(sketch, "E1585", {"start": v(37.1, -14.1) * mm, "mid": v(37.09, -14.1) * mm, "end": v(37.07, -14.12) * mm});
            skArc(sketch, "E1586", {"start": v(-24.85, -14.54) * mm, "mid": v(-24.87, -14.57) * mm, "end": v(-24.9, -14.61) * mm});
            skArc(sketch, "E1587", {"start": v(-24.9, -14.61) * mm, "mid": v(-24.91, -14.66) * mm, "end": v(-24.93, -14.7) * mm});
            skArc(sketch, "E1588", {"start": v(-24.93, -14.7) * mm, "mid": v(-24.94, -14.75) * mm, "end": v(-24.96, -14.8) * mm});
            skArc(sketch, "E1589", {"start": v(-24.96, -14.8) * mm, "mid": v(-24.96, -14.84) * mm, "end": v(-24.96, -14.88) * mm});
            skArc(sketch, "E1590", {"start": v(-24.96, -14.88) * mm, "mid": v(-24.97, -14.98) * mm, "end": v(-25, -15.08) * mm});
            skArc(sketch, "E1591", {"start": v(-25, -15.08) * mm, "mid": v(-25.03, -15.15) * mm, "end": v(-25.1, -15.21) * mm});
            skArc(sketch, "E1592", {"start": v(-25.1, -15.21) * mm, "mid": v(-25.17, -15.27) * mm, "end": v(-25.26, -15.3) * mm});
            skArc(sketch, "E1593", {"start": v(-25.26, -15.3) * mm, "mid": v(-25.4, -15.34) * mm, "end": v(-25.54, -15.36) * mm});
            skArc(sketch, "E1594", {"start": v(-25.54, -15.36) * mm, "mid": v(-25.77, -15.4) * mm, "end": v(-26, -15.46) * mm});
            skArc(sketch, "E1595", {"start": v(-26, -15.46) * mm, "mid": v(-26.08, -15.51) * mm, "end": v(-26.12, -15.6) * mm});
            skArc(sketch, "E1596", {"start": v(-26.12, -15.6) * mm, "mid": v(-26.09, -15.7) * mm, "end": v(-26, -15.75) * mm});
            skArc(sketch, "E1597", {"start": v(-26, -15.75) * mm, "mid": v(-25.78, -15.8) * mm, "end": v(-25.56, -15.84) * mm});
            skArc(sketch, "E1598", {"start": v(-25.56, -15.84) * mm, "mid": v(-25.44, -15.86) * mm, "end": v(-25.32, -15.88) * mm});
            skArc(sketch, "E1599", {"start": v(-25.32, -15.88) * mm, "mid": v(-25.26, -15.9) * mm, "end": v(-25.2, -15.91) * mm});
            skArc(sketch, "E1600", {"start": v(-25.2, -15.91) * mm, "mid": v(-25.17, -15.94) * mm, "end": v(-25.15, -15.97) * mm});
            skArc(sketch, "E1601", {"start": v(-25.15, -15.97) * mm, "mid": v(-25.13, -16.01) * mm, "end": v(-25.12, -16.06) * mm});
            skArc(sketch, "E1602", {"start": v(-25.12, -16.06) * mm, "mid": v(-25.11, -16.18) * mm, "end": v(-25.13, -16.3) * mm});
            skArc(sketch, "E1603", {"start": v(-25.13, -16.3) * mm, "mid": v(-25.2, -16.52) * mm, "end": v(-25.27, -16.74) * mm});
            skArc(sketch, "E1604", {"start": v(-25.27, -16.74) * mm, "mid": v(-25.38, -17.03) * mm, "end": v(-25.49, -17.3) * mm});
            skArc(sketch, "E1605", {"start": v(-25.49, -17.3) * mm, "mid": v(-25.63, -17.64) * mm, "end": v(-25.78, -17.96) * mm});
            skArc(sketch, "E1606", {"start": v(-25.78, -17.96) * mm, "mid": v(-25.91, -18.26) * mm, "end": v(-26.05, -18.57) * mm});
            skArc(sketch, "E1607", {"start": v(-26.05, -18.57) * mm, "mid": v(-26.12, -18.75) * mm, "end": v(-26.18, -18.94) * mm});
            skArc(sketch, "E1608", {"start": v(-26.18, -18.94) * mm, "mid": v(-26.2, -19.04) * mm, "end": v(-26.2, -19.15) * mm});
            skArc(sketch, "E1609", {"start": v(-26.2, -19.15) * mm, "mid": v(-26.19, -19.2) * mm, "end": v(-26.13, -19.22) * mm});
            skArc(sketch, "E1610", {"start": v(-26.13, -19.22) * mm, "mid": v(-26, -19.19) * mm, "end": v(-25.9, -19.1) * mm});
            skArc(sketch, "E1611", {"start": v(-25.9, -19.1) * mm, "mid": v(-25.73, -18.86) * mm, "end": v(-25.57, -18.6) * mm});
            skArc(sketch, "E1612", {"start": v(-25.57, -18.6) * mm, "mid": v(-25.39, -18.25) * mm, "end": v(-25.22, -17.9) * mm});
            skArc(sketch, "E1613", {"start": v(-25.22, -17.9) * mm, "mid": v(-25.03, -17.45) * mm, "end": v(-24.86, -17) * mm});
            skArc(sketch, "E1614", {"start": v(-24.86, -17) * mm, "mid": v(-24.75, -16.71) * mm, "end": v(-24.63, -16.44) * mm});
            skArc(sketch, "E1615", {"start": v(-24.63, -16.44) * mm, "mid": v(-24.54, -16.28) * mm, "end": v(-24.43, -16.14) * mm});
            skArc(sketch, "E1616", {"start": v(-24.43, -16.14) * mm, "mid": v(-24.3, -16.05) * mm, "end": v(-24.17, -15.98) * mm});
            skArc(sketch, "E1617", {"start": v(-24.17, -15.98) * mm, "mid": v(-23.97, -15.93) * mm, "end": v(-23.76, -15.9) * mm});
            skArc(sketch, "E1618", {"start": v(-23.76, -15.9) * mm, "mid": v(-23.53, -15.86) * mm, "end": v(-23.3, -15.82) * mm});
            skArc(sketch, "E1619", {"start": v(-23.3, -15.82) * mm, "mid": v(-23.15, -15.78) * mm, "end": v(-23, -15.7) * mm});
            skArc(sketch, "E1620", {"start": v(-23, -15.7) * mm, "mid": v(-22.94, -15.66) * mm, "end": v(-22.9, -15.59) * mm});
            skArc(sketch, "E1621", {"start": v(-22.9, -15.59) * mm, "mid": v(-22.9, -15.52) * mm, "end": v(-22.95, -15.47) * mm});
            skArc(sketch, "E1622", {"start": v(-22.95, -15.47) * mm, "mid": v(-22.98, -15.45) * mm, "end": v(-23, -15.45) * mm});
            skArc(sketch, "E1623", {"start": v(-23, -15.45) * mm, "mid": v(-23.1, -15.43) * mm, "end": v(-23.19, -15.42) * mm});
            skArc(sketch, "E1624", {"start": v(-23.19, -15.42) * mm, "mid": v(-23.3, -15.4) * mm, "end": v(-23.4, -15.39) * mm});
            skArc(sketch, "E1625", {"start": v(-23.4, -15.39) * mm, "mid": v(-23.53, -15.38) * mm, "end": v(-23.65, -15.37) * mm});
            skArc(sketch, "E1626", {"start": v(-23.65, -15.37) * mm, "mid": v(-23.77, -15.35) * mm, "end": v(-23.9, -15.34) * mm});
            skArc(sketch, "E1627", {"start": v(-23.9, -15.34) * mm, "mid": v(-24, -15.32) * mm, "end": v(-24.12, -15.3) * mm});
            skArc(sketch, "E1628", {"start": v(-24.12, -15.3) * mm, "mid": v(-24.2, -15.29) * mm, "end": v(-24.3, -15.27) * mm});
            skArc(sketch, "E1629", {"start": v(-24.3, -15.27) * mm, "mid": v(-24.34, -15.25) * mm, "end": v(-24.37, -15.23) * mm});
            skArc(sketch, "E1630", {"start": v(-24.37, -15.23) * mm, "mid": v(-24.4, -15.2) * mm, "end": v(-24.41, -15.18) * mm});
            skArc(sketch, "E1631", {"start": v(-24.41, -15.18) * mm, "mid": v(-24.43, -15.14) * mm, "end": v(-24.44, -15.1) * mm});
            skArc(sketch, "E1632", {"start": v(-24.44, -15.1) * mm, "mid": v(-24.46, -15.06) * mm, "end": v(-24.47, -15) * mm});
            skArc(sketch, "E1633", {"start": v(-24.47, -15) * mm, "mid": v(-24.47, -14.96) * mm, "end": v(-24.47, -14.92) * mm});
            skArc(sketch, "E1634", {"start": v(-24.47, -14.92) * mm, "mid": v(-24.48, -14.87) * mm, "end": v(-24.48, -14.82) * mm});
            skArc(sketch, "E1635", {"start": v(-24.48, -14.82) * mm, "mid": v(-24.5, -14.76) * mm, "end": v(-24.51, -14.7) * mm});
            skArc(sketch, "E1636", {"start": v(-24.51, -14.7) * mm, "mid": v(-24.53, -14.66) * mm, "end": v(-24.55, -14.6) * mm});
            skArc(sketch, "E1637", {"start": v(-24.55, -14.6) * mm, "mid": v(-24.58, -14.57) * mm, "end": v(-24.6, -14.53) * mm});
            skLineSegment(sketch, "E1638", {"start": v(-24.6, -14.53) * mm, "end": v(-24.73, -14.37) * mm});
            skLineSegment(sketch, "E1639", {"start": v(-24.73, -14.37) * mm, "end": v(-24.85, -14.54) * mm});
            skArc(sketch, "E1640", {"start": v(-21.74, -14.77) * mm, "mid": v(-21.73, -14.85) * mm, "end": v(-21.7, -14.92) * mm});
            skArc(sketch, "E1641", {"start": v(-21.7, -14.92) * mm, "mid": v(-21.55, -15.1) * mm, "end": v(-21.4, -15.27) * mm});
            skArc(sketch, "E1642", {"start": v(-21.4, -15.27) * mm, "mid": v(-21.24, -15.45) * mm, "end": v(-21.07, -15.63) * mm});
            skArc(sketch, "E1643", {"start": v(-21.07, -15.63) * mm, "mid": v(-20.9, -15.8) * mm, "end": v(-20.72, -15.95) * mm});
            skArc(sketch, "E1644", {"start": v(-20.72, -15.95) * mm, "mid": v(-20.59, -16.05) * mm, "end": v(-20.45, -16.16) * mm});
            skArc(sketch, "E1645", {"start": v(-20.45, -16.16) * mm, "mid": v(-20.34, -16.23) * mm, "end": v(-20.22, -16.3) * mm});
            skArc(sketch, "E1646", {"start": v(-20.22, -16.3) * mm, "mid": v(-20.13, -16.33) * mm, "end": v(-20.05, -16.35) * mm});
            skArc(sketch, "E1647", {"start": v(-20.05, -16.35) * mm, "mid": v(-20, -16.35) * mm, "end": v(-19.95, -16.33) * mm});
            skArc(sketch, "E1648", {"start": v(-19.95, -16.33) * mm, "mid": v(-19.91, -16.25) * mm, "end": v(-19.94, -16.17) * mm});
            skArc(sketch, "E1649", {"start": v(-19.94, -16.17) * mm, "mid": v(-20.16, -15.92) * mm, "end": v(-20.38, -15.67) * mm});
            skArc(sketch, "E1650", {"start": v(-20.38, -15.67) * mm, "mid": v(-20.63, -15.42) * mm, "end": v(-20.88, -15.18) * mm});
            skArc(sketch, "E1651", {"start": v(-20.88, -15.18) * mm, "mid": v(-21.1, -15) * mm, "end": v(-21.34, -14.84) * mm});
            skArc(sketch, "E1652", {"start": v(-21.34, -14.84) * mm, "mid": v(-21.44, -14.78) * mm, "end": v(-21.54, -14.72) * mm});
            skArc(sketch, "E1653", {"start": v(-21.54, -14.72) * mm, "mid": v(-21.6, -14.7) * mm, "end": v(-21.65, -14.68) * mm});
            skArc(sketch, "E1654", {"start": v(-21.65, -14.68) * mm, "mid": v(-21.69, -14.68) * mm, "end": v(-21.72, -14.7) * mm});
            skArc(sketch, "E1655", {"start": v(-21.72, -14.7) * mm, "mid": v(-21.74, -14.73) * mm, "end": v(-21.74, -14.77) * mm});
            skArc(sketch, "E1656", {"start": v(-21.82, -16.46) * mm, "mid": v(-21.84, -16.52) * mm, "end": v(-21.85, -16.58) * mm});
            skArc(sketch, "E1657", {"start": v(-21.85, -16.58) * mm, "mid": v(-21.87, -16.69) * mm, "end": v(-21.89, -16.8) * mm});
            skArc(sketch, "E1658", {"start": v(-21.89, -16.8) * mm, "mid": v(-21.9, -16.92) * mm, "end": v(-21.92, -17.05) * mm});
            skArc(sketch, "E1659", {"start": v(-21.92, -17.05) * mm, "mid": v(-21.93, -17.18) * mm, "end": v(-21.94, -17.32) * mm});
            skArc(sketch, "E1660", {"start": v(-21.94, -17.32) * mm, "mid": v(-21.96, -17.57) * mm, "end": v(-21.99, -17.81) * mm});
            skArc(sketch, "E1661", {"start": v(-21.99, -17.81) * mm, "mid": v(-22.02, -17.93) * mm, "end": v(-22.09, -18.03) * mm});
            skArc(sketch, "E1662", {"start": v(-22.09, -18.03) * mm, "mid": v(-22.17, -18.1) * mm, "end": v(-22.28, -18.14) * mm});
            skArc(sketch, "E1663", {"start": v(-22.28, -18.14) * mm, "mid": v(-22.47, -18.16) * mm, "end": v(-22.66, -18.17) * mm});
            skArc(sketch, "E1664", {"start": v(-22.66, -18.17) * mm, "mid": v(-22.92, -18.18) * mm, "end": v(-23.19, -18.23) * mm});
            skArc(sketch, "E1665", {"start": v(-23.19, -18.23) * mm, "mid": v(-23.43, -18.3) * mm, "end": v(-23.66, -18.39) * mm});
            skArc(sketch, "E1666", {"start": v(-23.66, -18.39) * mm, "mid": v(-23.87, -18.5) * mm, "end": v(-24.06, -18.64) * mm});
            skArc(sketch, "E1667", {"start": v(-24.06, -18.64) * mm, "mid": v(-24.21, -18.8) * mm, "end": v(-24.34, -18.97) * mm});
            skArc(sketch, "E1668", {"start": v(-24.34, -18.97) * mm, "mid": v(-24.43, -19.18) * mm, "end": v(-24.46, -19.4) * mm});
            skArc(sketch, "E1669", {"start": v(-24.46, -19.4) * mm, "mid": v(-24.42, -19.62) * mm, "end": v(-24.32, -19.8) * mm});
            skArc(sketch, "E1670", {"start": v(-24.32, -19.8) * mm, "mid": v(-24.12, -19.98) * mm, "end": v(-23.89, -20.1) * mm});
            skArc(sketch, "E1671", {"start": v(-23.89, -20.1) * mm, "mid": v(-23.56, -20.19) * mm, "end": v(-23.23, -20.25) * mm});
            skArc(sketch, "E1672", {"start": v(-23.23, -20.25) * mm, "mid": v(-22.97, -20.26) * mm, "end": v(-22.7, -20.24) * mm});
            skArc(sketch, "E1673", {"start": v(-22.7, -20.24) * mm, "mid": v(-22.42, -20.18) * mm, "end": v(-22.15, -20.1) * mm});
            skArc(sketch, "E1674", {"start": v(-22.15, -20.1) * mm, "mid": v(-21.92, -20.01) * mm, "end": v(-21.7, -19.9) * mm});
            skArc(sketch, "E1675", {"start": v(-21.7, -19.9) * mm, "mid": v(-21.58, -19.8) * mm, "end": v(-21.51, -19.66) * mm});
            skArc(sketch, "E1676", {"start": v(-21.51, -19.66) * mm, "mid": v(-21.5, -19.63) * mm, "end": v(-21.5, -19.6) * mm});
            skArc(sketch, "E1677", {"start": v(-21.5, -19.6) * mm, "mid": v(-21.48, -19.56) * mm, "end": v(-21.47, -19.51) * mm});
            skArc(sketch, "E1678", {"start": v(-21.47, -19.51) * mm, "mid": v(-21.46, -19.47) * mm, "end": v(-21.45, -19.43) * mm});
            skArc(sketch, "E1679", {"start": v(-21.45, -19.43) * mm, "mid": v(-21.44, -19.38) * mm, "end": v(-21.43, -19.34) * mm});
            skArc(sketch, "E1680", {"start": v(-21.43, -19.34) * mm, "mid": v(-21.4, -19.27) * mm, "end": v(-21.35, -19.2) * mm});
            skArc(sketch, "E1681", {"start": v(-21.35, -19.2) * mm, "mid": v(-21.3, -19.17) * mm, "end": v(-21.22, -19.16) * mm});
            skArc(sketch, "E1682", {"start": v(-21.22, -19.16) * mm, "mid": v(-21.11, -19.17) * mm, "end": v(-21, -19.21) * mm});
            skArc(sketch, "E1683", {"start": v(-21, -19.21) * mm, "mid": v(-20.85, -19.3) * mm, "end": v(-20.7, -19.4) * mm});
            skArc(sketch, "E1684", {"start": v(-20.7, -19.4) * mm, "mid": v(-20.56, -19.47) * mm, "end": v(-20.43, -19.55) * mm});
            skArc(sketch, "E1685", {"start": v(-20.43, -19.55) * mm, "mid": v(-20.32, -19.6) * mm, "end": v(-20.21, -19.62) * mm});
            skArc(sketch, "E1686", {"start": v(-20.21, -19.62) * mm, "mid": v(-20.13, -19.63) * mm, "end": v(-20.05, -19.63) * mm});
            skArc(sketch, "E1687", {"start": v(-20.05, -19.63) * mm, "mid": v(-20, -19.6) * mm, "end": v(-19.96, -19.57) * mm});
            skArc(sketch, "E1688", {"start": v(-19.96, -19.57) * mm, "mid": v(-19.94, -19.5) * mm, "end": v(-19.95, -19.45) * mm});
            skArc(sketch, "E1689", {"start": v(-19.95, -19.45) * mm, "mid": v(-20, -19.36) * mm, "end": v(-20.07, -19.28) * mm});
            skArc(sketch, "E1690", {"start": v(-20.07, -19.28) * mm, "mid": v(-20.18, -19.17) * mm, "end": v(-20.3, -19.08) * mm});
            skArc(sketch, "E1691", {"start": v(-20.3, -19.08) * mm, "mid": v(-20.46, -18.95) * mm, "end": v(-20.63, -18.83) * mm});
            skArc(sketch, "E1692", {"start": v(-20.63, -18.83) * mm, "mid": v(-20.86, -18.66) * mm, "end": v(-21.1, -18.49) * mm});
            skArc(sketch, "E1693", {"start": v(-21.1, -18.49) * mm, "mid": v(-21.2, -18.38) * mm, "end": v(-21.3, -18.24) * mm});
            skArc(sketch, "E1694", {"start": v(-21.3, -18.24) * mm, "mid": v(-21.36, -18.1) * mm, "end": v(-21.4, -17.93) * mm});
            skArc(sketch, "E1695", {"start": v(-21.4, -17.93) * mm, "mid": v(-21.44, -17.61) * mm, "end": v(-21.46, -17.3) * mm});
            skArc(sketch, "E1696", {"start": v(-21.46, -17.3) * mm, "mid": v(-21.48, -17.1) * mm, "end": v(-21.5, -16.9) * mm});
            skArc(sketch, "E1697", {"start": v(-21.5, -16.9) * mm, "mid": v(-21.5, -16.77) * mm, "end": v(-21.53, -16.64) * mm});
            skArc(sketch, "E1698", {"start": v(-21.53, -16.64) * mm, "mid": v(-21.55, -16.55) * mm, "end": v(-21.57, -16.46) * mm});
            skArc(sketch, "E1699", {"start": v(-21.57, -16.46) * mm, "mid": v(-21.6, -16.41) * mm, "end": v(-21.63, -16.37) * mm});
            skArc(sketch, "E1700", {"start": v(-21.63, -16.37) * mm, "mid": v(-21.66, -16.34) * mm, "end": v(-21.7, -16.31) * mm});
            skArc(sketch, "E1701", {"start": v(-21.7, -16.31) * mm, "mid": v(-21.71, -16.3) * mm, "end": v(-21.73, -16.3) * mm});
            skArc(sketch, "E1702", {"start": v(-21.73, -16.3) * mm, "mid": v(-21.75, -16.32) * mm, "end": v(-21.77, -16.34) * mm});
            skArc(sketch, "E1703", {"start": v(-21.77, -16.34) * mm, "mid": v(-21.8, -16.4) * mm, "end": v(-21.82, -16.46) * mm});
            skArc(sketch, "E1704", {"start": v(-22.04, -18.74) * mm, "mid": v(-22, -18.8) * mm, "end": v(-21.98, -18.84) * mm});
            skArc(sketch, "E1705", {"start": v(-21.98, -18.84) * mm, "mid": v(-21.96, -18.9) * mm, "end": v(-21.96, -18.98) * mm});
            skArc(sketch, "E1706", {"start": v(-21.96, -18.98) * mm, "mid": v(-21.96, -19.06) * mm, "end": v(-21.98, -19.15) * mm});
            skArc(sketch, "E1707", {"start": v(-21.98, -19.15) * mm, "mid": v(-22, -19.25) * mm, "end": v(-22.03, -19.35) * mm});
            skArc(sketch, "E1708", {"start": v(-22.03, -19.35) * mm, "mid": v(-22.05, -19.4) * mm, "end": v(-22.08, -19.45) * mm});
            skArc(sketch, "E1709", {"start": v(-22.08, -19.45) * mm, "mid": v(-22.1, -19.5) * mm, "end": v(-22.14, -19.53) * mm});
            skArc(sketch, "E1710", {"start": v(-22.14, -19.53) * mm, "mid": v(-22.18, -19.56) * mm, "end": v(-22.22, -19.59) * mm});
            skArc(sketch, "E1711", {"start": v(-22.22, -19.59) * mm, "mid": v(-22.27, -19.61) * mm, "end": v(-22.33, -19.63) * mm});
            skArc(sketch, "E1712", {"start": v(-22.33, -19.63) * mm, "mid": v(-22.57, -19.7) * mm, "end": v(-22.82, -19.74) * mm});
            skArc(sketch, "E1713", {"start": v(-22.82, -19.74) * mm, "mid": v(-23.07, -19.75) * mm, "end": v(-23.31, -19.75) * mm});
            skArc(sketch, "E1714", {"start": v(-23.31, -19.75) * mm, "mid": v(-23.52, -19.72) * mm, "end": v(-23.72, -19.67) * mm});
            skArc(sketch, "E1715", {"start": v(-23.72, -19.67) * mm, "mid": v(-23.83, -19.6) * mm, "end": v(-23.91, -19.5) * mm});
            skArc(sketch, "E1716", {"start": v(-23.91, -19.5) * mm, "mid": v(-23.96, -19.4) * mm, "end": v(-23.98, -19.27) * mm});
            skArc(sketch, "E1717", {"start": v(-23.98, -19.27) * mm, "mid": v(-23.98, -19.17) * mm, "end": v(-23.94, -19.07) * mm});
            skArc(sketch, "E1718", {"start": v(-23.94, -19.07) * mm, "mid": v(-23.88, -18.97) * mm, "end": v(-23.79, -18.9) * mm});
            skArc(sketch, "E1719", {"start": v(-23.79, -18.9) * mm, "mid": v(-23.66, -18.82) * mm, "end": v(-23.53, -18.77) * mm});
            skArc(sketch, "E1720", {"start": v(-23.53, -18.77) * mm, "mid": v(-23.37, -18.72) * mm, "end": v(-23.2, -18.7) * mm});
            skArc(sketch, "E1721", {"start": v(-23.2, -18.7) * mm, "mid": v(-22.95, -18.67) * mm, "end": v(-22.7, -18.67) * mm});
            skArc(sketch, "E1722", {"start": v(-22.7, -18.67) * mm, "mid": v(-22.45, -18.67) * mm, "end": v(-22.2, -18.67) * mm});
            skArc(sketch, "E1723", {"start": v(-22.2, -18.67) * mm, "mid": v(-22.11, -18.7) * mm, "end": v(-22.04, -18.74) * mm});
            skArc(sketch, "E1724", {"start": v(-36.5, -14.52) * mm, "mid": v(-36.55, -14.59) * mm, "end": v(-36.52, -14.66) * mm});
            skArc(sketch, "E1725", {"start": v(-36.52, -14.66) * mm, "mid": v(-36.41, -14.74) * mm, "end": v(-36.3, -14.8) * mm});
            skArc(sketch, "E1726", {"start": v(-36.3, -14.8) * mm, "mid": v(-36, -14.88) * mm, "end": v(-35.7, -14.95) * mm});
            skArc(sketch, "E1727", {"start": v(-35.7, -14.95) * mm, "mid": v(-35.17, -15.06) * mm, "end": v(-34.63, -15.16) * mm});
            skArc(sketch, "E1728", {"start": v(-34.63, -15.16) * mm, "mid": v(-34.28, -15.22) * mm, "end": v(-33.93, -15.28) * mm});
            skArc(sketch, "E1729", {"start": v(-33.93, -15.28) * mm, "mid": v(-33.78, -15.3) * mm, "end": v(-33.63, -15.32) * mm});
            skArc(sketch, "E1730", {"start": v(-33.63, -15.32) * mm, "mid": v(-33.55, -15.32) * mm, "end": v(-33.47, -15.31) * mm});
            skArc(sketch, "E1731", {"start": v(-33.47, -15.31) * mm, "mid": v(-33.4, -15.3) * mm, "end": v(-33.35, -15.25) * mm});
            skArc(sketch, "E1732", {"start": v(-33.35, -15.25) * mm, "mid": v(-33.29, -15.16) * mm, "end": v(-33.27, -15.06) * mm});
            skArc(sketch, "E1733", {"start": v(-33.27, -15.06) * mm, "mid": v(-33.3, -14.96) * mm, "end": v(-33.38, -14.89) * mm});
            skArc(sketch, "E1734", {"start": v(-33.38, -14.89) * mm, "mid": v(-33.58, -14.8) * mm, "end": v(-33.8, -14.75) * mm});
            skArc(sketch, "E1735", {"start": v(-33.8, -14.75) * mm, "mid": v(-34.23, -14.67) * mm, "end": v(-34.67, -14.6) * mm});
            skArc(sketch, "E1736", {"start": v(-34.67, -14.6) * mm, "mid": v(-35.02, -14.56) * mm, "end": v(-35.37, -14.51) * mm});
            skArc(sketch, "E1737", {"start": v(-35.37, -14.51) * mm, "mid": v(-35.64, -14.49) * mm, "end": v(-35.92, -14.47) * mm});
            skArc(sketch, "E1738", {"start": v(-35.92, -14.47) * mm, "mid": v(-36.12, -14.46) * mm, "end": v(-36.32, -14.47) * mm});
            skArc(sketch, "E1739", {"start": v(-36.32, -14.47) * mm, "mid": v(-36.42, -14.48) * mm, "end": v(-36.5, -14.52) * mm});
            skArc(sketch, "E1740", {"start": v(-35.17, -15.42) * mm, "mid": v(-35.22, -15.45) * mm, "end": v(-35.26, -15.51) * mm});
            skArc(sketch, "E1741", {"start": v(-35.26, -15.51) * mm, "mid": v(-35.3, -15.63) * mm, "end": v(-35.33, -15.76) * mm});
            skArc(sketch, "E1742", {"start": v(-35.33, -15.76) * mm, "mid": v(-35.36, -15.9) * mm, "end": v(-35.37, -16.05) * mm});
            skArc(sketch, "E1743", {"start": v(-35.37, -16.05) * mm, "mid": v(-35.37, -16.18) * mm, "end": v(-35.36, -16.3) * mm});
            skArc(sketch, "E1744", {"start": v(-35.36, -16.3) * mm, "mid": v(-35.33, -16.47) * mm, "end": v(-35.3, -16.62) * mm});
            skArc(sketch, "E1745", {"start": v(-35.3, -16.62) * mm, "mid": v(-35.25, -16.8) * mm, "end": v(-35.2, -16.97) * mm});
            skArc(sketch, "E1746", {"start": v(-35.2, -16.97) * mm, "mid": v(-35.14, -17.14) * mm, "end": v(-35.07, -17.32) * mm});
            skArc(sketch, "E1747", {"start": v(-35.07, -17.32) * mm, "mid": v(-35, -17.47) * mm, "end": v(-34.93, -17.63) * mm});
            skArc(sketch, "E1748", {"start": v(-34.93, -17.63) * mm, "mid": v(-34.9, -17.7) * mm, "end": v(-34.86, -17.79) * mm});
            skArc(sketch, "E1749", {"start": v(-34.86, -17.79) * mm, "mid": v(-34.82, -17.89) * mm, "end": v(-34.78, -18) * mm});
            skArc(sketch, "E1750", {"start": v(-34.78, -18) * mm, "mid": v(-34.74, -18.1) * mm, "end": v(-34.7, -18.2) * mm});
            skArc(sketch, "E1751", {"start": v(-34.7, -18.2) * mm, "mid": v(-34.68, -18.3) * mm, "end": v(-34.65, -18.4) * mm});
            skArc(sketch, "E1752", {"start": v(-34.65, -18.4) * mm, "mid": v(-34.6, -18.7) * mm, "end": v(-34.58, -19) * mm});
            skArc(sketch, "E1753", {"start": v(-34.58, -19) * mm, "mid": v(-34.62, -19.2) * mm, "end": v(-34.73, -19.37) * mm});
            skArc(sketch, "E1754", {"start": v(-34.73, -19.37) * mm, "mid": v(-34.9, -19.48) * mm, "end": v(-35.1, -19.5) * mm});
            skArc(sketch, "E1755", {"start": v(-35.1, -19.5) * mm, "mid": v(-35.37, -19.45) * mm, "end": v(-35.64, -19.36) * mm});
            skArc(sketch, "E1756", {"start": v(-35.64, -19.36) * mm, "mid": v(-35.77, -19.3) * mm, "end": v(-35.9, -19.26) * mm});
            skArc(sketch, "E1757", {"start": v(-35.9, -19.26) * mm, "mid": v(-36, -19.24) * mm, "end": v(-36.09, -19.23) * mm});
            skArc(sketch, "E1758", {"start": v(-36.09, -19.23) * mm, "mid": v(-36.15, -19.23) * mm, "end": v(-36.2, -19.25) * mm});
            skArc(sketch, "E1759", {"start": v(-36.2, -19.25) * mm, "mid": v(-36.25, -19.28) * mm, "end": v(-36.28, -19.33) * mm});
            skArc(sketch, "E1760", {"start": v(-36.28, -19.33) * mm, "mid": v(-36.29, -19.44) * mm, "end": v(-36.23, -19.54) * mm});
            skArc(sketch, "E1761", {"start": v(-36.23, -19.54) * mm, "mid": v(-36.07, -19.66) * mm, "end": v(-35.9, -19.76) * mm});
            skArc(sketch, "E1762", {"start": v(-35.9, -19.76) * mm, "mid": v(-35.68, -19.86) * mm, "end": v(-35.44, -19.93) * mm});
            skArc(sketch, "E1763", {"start": v(-35.44, -19.93) * mm, "mid": v(-35.2, -19.98) * mm, "end": v(-34.97, -20) * mm});
            skArc(sketch, "E1764", {"start": v(-34.97, -20) * mm, "mid": v(-34.86, -19.99) * mm, "end": v(-34.76, -19.98) * mm});
            skArc(sketch, "E1765", {"start": v(-34.76, -19.98) * mm, "mid": v(-34.7, -19.97) * mm, "end": v(-34.63, -19.95) * mm});
            skArc(sketch, "E1766", {"start": v(-34.63, -19.95) * mm, "mid": v(-34.57, -19.92) * mm, "end": v(-34.52, -19.88) * mm});
            skArc(sketch, "E1767", {"start": v(-34.52, -19.88) * mm, "mid": v(-34.45, -19.82) * mm, "end": v(-34.38, -19.76) * mm});
            skArc(sketch, "E1768", {"start": v(-34.38, -19.76) * mm, "mid": v(-34.23, -19.56) * mm, "end": v(-34.13, -19.33) * mm});
            skArc(sketch, "E1769", {"start": v(-34.13, -19.33) * mm, "mid": v(-34.08, -19.05) * mm, "end": v(-34.07, -18.76) * mm});
            skArc(sketch, "E1770", {"start": v(-34.07, -18.76) * mm, "mid": v(-34.12, -18.4) * mm, "end": v(-34.2, -18.06) * mm});
            skArc(sketch, "E1771", {"start": v(-34.2, -18.06) * mm, "mid": v(-34.35, -17.66) * mm, "end": v(-34.53, -17.27) * mm});
            skArc(sketch, "E1772", {"start": v(-34.53, -17.27) * mm, "mid": v(-34.64, -17.06) * mm, "end": v(-34.74, -16.84) * mm});
            skArc(sketch, "E1773", {"start": v(-34.74, -16.84) * mm, "mid": v(-34.78, -16.73) * mm, "end": v(-34.82, -16.6) * mm});
            skArc(sketch, "E1774", {"start": v(-34.82, -16.6) * mm, "mid": v(-34.85, -16.5) * mm, "end": v(-34.86, -16.37) * mm});
            skArc(sketch, "E1775", {"start": v(-34.86, -16.37) * mm, "mid": v(-34.87, -16.19) * mm, "end": v(-34.87, -16) * mm});
            skArc(sketch, "E1776", {"start": v(-34.87, -16) * mm, "mid": v(-34.87, -15.8) * mm, "end": v(-34.88, -15.6) * mm});
            skArc(sketch, "E1777", {"start": v(-34.88, -15.6) * mm, "mid": v(-34.9, -15.52) * mm, "end": v(-34.92, -15.44) * mm});
            skArc(sketch, "E1778", {"start": v(-34.92, -15.44) * mm, "mid": v(-34.96, -15.4) * mm, "end": v(-35.01, -15.39) * mm});
            skArc(sketch, "E1779", {"start": v(-35.01, -15.39) * mm, "mid": v(-35.1, -15.4) * mm, "end": v(-35.17, -15.42) * mm});
            skArc(sketch, "E1780", {"start": v(-33.32, -16.6) * mm, "mid": v(-33.34, -16.66) * mm, "end": v(-33.33, -16.7) * mm});
            skArc(sketch, "E1781", {"start": v(-33.33, -16.7) * mm, "mid": v(-33.06, -17.24) * mm, "end": v(-32.79, -17.77) * mm});
            skArc(sketch, "E1782", {"start": v(-32.79, -17.77) * mm, "mid": v(-32.54, -18.25) * mm, "end": v(-32.28, -18.72) * mm});
            skArc(sketch, "E1783", {"start": v(-32.28, -18.72) * mm, "mid": v(-32.14, -18.96) * mm, "end": v(-31.98, -19.19) * mm});
            skArc(sketch, "E1784", {"start": v(-31.98, -19.19) * mm, "mid": v(-31.86, -19.33) * mm, "end": v(-31.74, -19.48) * mm});
            skArc(sketch, "E1785", {"start": v(-31.74, -19.48) * mm, "mid": v(-31.69, -19.53) * mm, "end": v(-31.62, -19.56) * mm});
            skArc(sketch, "E1786", {"start": v(-31.62, -19.56) * mm, "mid": v(-31.58, -19.55) * mm, "end": v(-31.56, -19.5) * mm});
            skArc(sketch, "E1787", {"start": v(-31.56, -19.5) * mm, "mid": v(-31.55, -19.4) * mm, "end": v(-31.56, -19.29) * mm});
            skArc(sketch, "E1788", {"start": v(-31.56, -19.29) * mm, "mid": v(-31.6, -19.12) * mm, "end": v(-31.65, -18.96) * mm});
            skArc(sketch, "E1789", {"start": v(-31.65, -18.96) * mm, "mid": v(-31.74, -18.73) * mm, "end": v(-31.85, -18.5) * mm});
            skArc(sketch, "E1790", {"start": v(-31.85, -18.5) * mm, "mid": v(-31.98, -18.24) * mm, "end": v(-32.12, -17.98) * mm});
            skArc(sketch, "E1791", {"start": v(-32.12, -17.98) * mm, "mid": v(-32.29, -17.7) * mm, "end": v(-32.46, -17.43) * mm});
            skArc(sketch, "E1792", {"start": v(-32.46, -17.43) * mm, "mid": v(-32.63, -17.17) * mm, "end": v(-32.8, -16.92) * mm});
            skArc(sketch, "E1793", {"start": v(-32.8, -16.92) * mm, "mid": v(-32.9, -16.79) * mm, "end": v(-33.02, -16.66) * mm});
            skArc(sketch, "E1794", {"start": v(-33.02, -16.66) * mm, "mid": v(-33.1, -16.6) * mm, "end": v(-33.18, -16.57) * mm});
            skArc(sketch, "E1795", {"start": v(-33.18, -16.57) * mm, "mid": v(-33.26, -16.57) * mm, "end": v(-33.32, -16.6) * mm});
            skArc(sketch, "E1796", {"start": v(-36.8, -17) * mm, "mid": v(-36.9, -17.16) * mm, "end": v(-36.98, -17.33) * mm});
            skArc(sketch, "E1797", {"start": v(-36.98, -17.33) * mm, "mid": v(-37.11, -17.6) * mm, "end": v(-37.24, -17.86) * mm});
            skArc(sketch, "E1798", {"start": v(-37.24, -17.86) * mm, "mid": v(-37.37, -18.14) * mm, "end": v(-37.5, -18.42) * mm});
            skArc(sketch, "E1799", {"start": v(-37.5, -18.42) * mm, "mid": v(-37.6, -18.64) * mm, "end": v(-37.68, -18.85) * mm});
            skArc(sketch, "E1800", {"start": v(-37.68, -18.85) * mm, "mid": v(-37.77, -19.1) * mm, "end": v(-37.85, -19.33) * mm});
            skArc(sketch, "E1801", {"start": v(-37.85, -19.33) * mm, "mid": v(-37.85, -19.41) * mm, "end": v(-37.83, -19.48) * mm});
            skArc(sketch, "E1802", {"start": v(-37.83, -19.48) * mm, "mid": v(-37.78, -19.51) * mm, "end": v(-37.72, -19.5) * mm});
            skArc(sketch, "E1803", {"start": v(-37.72, -19.5) * mm, "mid": v(-37.57, -19.36) * mm, "end": v(-37.43, -19.22) * mm});
            skArc(sketch, "E1804", {"start": v(-37.43, -19.22) * mm, "mid": v(-37.3, -19.06) * mm, "end": v(-37.17, -18.89) * mm});
            skArc(sketch, "E1805", {"start": v(-37.17, -18.89) * mm, "mid": v(-37.03, -18.64) * mm, "end": v(-36.9, -18.38) * mm});
            skArc(sketch, "E1806", {"start": v(-36.9, -18.38) * mm, "mid": v(-36.76, -18.12) * mm, "end": v(-36.65, -17.84) * mm});
            skArc(sketch, "E1807", {"start": v(-36.65, -17.84) * mm, "mid": v(-36.57, -17.62) * mm, "end": v(-36.51, -17.39) * mm});
            skArc(sketch, "E1808", {"start": v(-36.51, -17.39) * mm, "mid": v(-36.47, -17.2) * mm, "end": v(-36.45, -17) * mm});
            skArc(sketch, "E1809", {"start": v(-36.45, -17) * mm, "mid": v(-36.46, -16.9) * mm, "end": v(-36.5, -16.8) * mm});
            skArc(sketch, "E1810", {"start": v(-36.5, -16.8) * mm, "mid": v(-36.56, -16.77) * mm, "end": v(-36.62, -16.79) * mm});
            skArc(sketch, "E1811", {"start": v(-36.62, -16.79) * mm, "mid": v(-36.72, -16.89) * mm, "end": v(-36.8, -17) * mm});
            skArc(sketch, "E1812", {"start": v(9.73, -14.62) * mm, "mid": v(9.71, -14.67) * mm, "end": v(9.7, -14.73) * mm});
            skArc(sketch, "E1813", {"start": v(9.7, -14.73) * mm, "mid": v(9.7, -14.94) * mm, "end": v(9.68, -15.15) * mm});
            skArc(sketch, "E1814", {"start": v(9.68, -15.15) * mm, "mid": v(9.66, -15.4) * mm, "end": v(9.64, -15.65) * mm});
            skArc(sketch, "E1815", {"start": v(9.64, -15.65) * mm, "mid": v(9.63, -15.93) * mm, "end": v(9.61, -16.21) * mm});
            skArc(sketch, "E1816", {"start": v(9.61, -16.21) * mm, "mid": v(9.6, -16.81) * mm, "end": v(9.58, -17.41) * mm});
            skArc(sketch, "E1817", {"start": v(9.58, -17.41) * mm, "mid": v(9.58, -18) * mm, "end": v(9.6, -18.59) * mm});
            skArc(sketch, "E1818", {"start": v(9.6, -18.59) * mm, "mid": v(9.62, -19.1) * mm, "end": v(9.65, -19.63) * mm});
            skArc(sketch, "E1819", {"start": v(9.65, -19.63) * mm, "mid": v(9.68, -19.76) * mm, "end": v(9.75, -19.88) * mm});
            skArc(sketch, "E1820", {"start": v(9.75, -19.88) * mm, "mid": v(9.92, -20) * mm, "end": v(10.12, -20.01) * mm});
            skArc(sketch, "E1821", {"start": v(10.12, -20.01) * mm, "mid": v(10.55, -19.91) * mm, "end": v(10.97, -19.78) * mm});
            skArc(sketch, "E1822", {"start": v(10.97, -19.78) * mm, "mid": v(11.49, -19.58) * mm, "end": v(11.99, -19.34) * mm});
            skArc(sketch, "E1823", {"start": v(11.99, -19.34) * mm, "mid": v(12.53, -19.05) * mm, "end": v(13.05, -18.73) * mm});
            skArc(sketch, "E1824", {"start": v(13.05, -18.73) * mm, "mid": v(13.4, -18.47) * mm, "end": v(13.76, -18.2) * mm});
            skArc(sketch, "E1825", {"start": v(13.76, -18.2) * mm, "mid": v(14.12, -17.88) * mm, "end": v(14.47, -17.55) * mm});
            skArc(sketch, "E1826", {"start": v(14.47, -17.55) * mm, "mid": v(14.77, -17.24) * mm, "end": v(15.05, -16.93) * mm});
            skArc(sketch, "E1827", {"start": v(15.05, -16.93) * mm, "mid": v(15.1, -16.82) * mm, "end": v(15.05, -16.72) * mm});
            skArc(sketch, "E1828", {"start": v(15.05, -16.72) * mm, "mid": v(15, -16.7) * mm, "end": v(14.95, -16.7) * mm});
            skArc(sketch, "E1829", {"start": v(14.95, -16.7) * mm, "mid": v(14.85, -16.73) * mm, "end": v(14.76, -16.78) * mm});
            skArc(sketch, "E1830", {"start": v(14.76, -16.78) * mm, "mid": v(14.62, -16.85) * mm, "end": v(14.5, -16.94) * mm});
            skArc(sketch, "E1831", {"start": v(14.5, -16.94) * mm, "mid": v(14.33, -17.07) * mm, "end": v(14.17, -17.2) * mm});
            skArc(sketch, "E1832", {"start": v(14.17, -17.2) * mm, "mid": v(13.68, -17.58) * mm, "end": v(13.17, -17.94) * mm});
            skArc(sketch, "E1833", {"start": v(13.17, -17.94) * mm, "mid": v(12.64, -18.29) * mm, "end": v(12.1, -18.61) * mm});
            skArc(sketch, "E1834", {"start": v(12.1, -18.61) * mm, "mid": v(11.6, -18.88) * mm, "end": v(11.11, -19.12) * mm});
            skArc(sketch, "E1835", {"start": v(11.11, -19.12) * mm, "mid": v(10.83, -19.22) * mm, "end": v(10.53, -19.25) * mm});
            skArc(sketch, "E1836", {"start": v(10.53, -19.25) * mm, "mid": v(10.44, -19.25) * mm, "end": v(10.35, -19.25) * mm});
            skArc(sketch, "E1837", {"start": v(10.35, -19.25) * mm, "mid": v(10.3, -19.24) * mm, "end": v(10.26, -19.22) * mm});
            skArc(sketch, "E1838", {"start": v(10.26, -19.22) * mm, "mid": v(10.23, -19.2) * mm, "end": v(10.2, -19.17) * mm});
            skArc(sketch, "E1839", {"start": v(10.2, -19.17) * mm, "mid": v(10.18, -19.1) * mm, "end": v(10.16, -19.05) * mm});
            skArc(sketch, "E1840", {"start": v(10.16, -19.05) * mm, "mid": v(10.15, -18.97) * mm, "end": v(10.14, -18.9) * mm});
            skArc(sketch, "E1841", {"start": v(10.14, -18.9) * mm, "mid": v(10.12, -18.6) * mm, "end": v(10.1, -18.3) * mm});
            skArc(sketch, "E1842", {"start": v(10.1, -18.3) * mm, "mid": v(10.08, -17.95) * mm, "end": v(10.07, -17.6) * mm});
            skArc(sketch, "E1843", {"start": v(10.07, -17.6) * mm, "mid": v(10.05, -17.2) * mm, "end": v(10.04, -16.8) * mm});
            skArc(sketch, "E1844", {"start": v(10.04, -16.8) * mm, "mid": v(10.02, -16.17) * mm, "end": v(10, -15.53) * mm});
            skArc(sketch, "E1845", {"start": v(10, -15.53) * mm, "mid": v(9.98, -15.22) * mm, "end": v(9.95, -14.9) * mm});
            skArc(sketch, "E1846", {"start": v(9.95, -14.9) * mm, "mid": v(9.93, -14.71) * mm, "end": v(9.9, -14.53) * mm});
            skArc(sketch, "E1847", {"start": v(9.9, -14.53) * mm, "mid": v(9.88, -14.48) * mm, "end": v(9.83, -14.46) * mm});
            skArc(sketch, "E1848", {"start": v(9.83, -14.46) * mm, "mid": v(9.81, -14.46) * mm, "end": v(9.8, -14.47) * mm});
            skArc(sketch, "E1849", {"start": v(9.8, -14.47) * mm, "mid": v(9.79, -14.49) * mm, "end": v(9.77, -14.5) * mm});
            skArc(sketch, "E1850", {"start": v(9.77, -14.5) * mm, "mid": v(9.76, -14.53) * mm, "end": v(9.75, -14.56) * mm});
            skArc(sketch, "E1851", {"start": v(9.75, -14.56) * mm, "mid": v(9.74, -14.59) * mm, "end": v(9.73, -14.62) * mm});
            skArc(sketch, "E1852", {"start": v(20.99, -14.82) * mm, "mid": v(20.97, -14.88) * mm, "end": v(21, -14.93) * mm});
            skArc(sketch, "E1853", {"start": v(21, -14.93) * mm, "mid": v(21.08, -15.03) * mm, "end": v(21.17, -15.12) * mm});
            skArc(sketch, "E1854", {"start": v(21.17, -15.12) * mm, "mid": v(21.31, -15.24) * mm, "end": v(21.46, -15.35) * mm});
            skArc(sketch, "E1855", {"start": v(21.46, -15.35) * mm, "mid": v(21.66, -15.48) * mm, "end": v(21.86, -15.6) * mm});
            skArc(sketch, "E1856", {"start": v(21.86, -15.6) * mm, "mid": v(22.15, -15.77) * mm, "end": v(22.45, -15.94) * mm});
            skArc(sketch, "E1857", {"start": v(22.45, -15.94) * mm, "mid": v(22.65, -16.04) * mm, "end": v(22.86, -16.14) * mm});
            skArc(sketch, "E1858", {"start": v(22.86, -16.14) * mm, "mid": v(23, -16.2) * mm, "end": v(23.16, -16.23) * mm});
            skArc(sketch, "E1859", {"start": v(23.16, -16.23) * mm, "mid": v(23.25, -16.24) * mm, "end": v(23.33, -16.21) * mm});
            skArc(sketch, "E1860", {"start": v(23.33, -16.21) * mm, "mid": v(23.36, -16.2) * mm, "end": v(23.39, -16.18) * mm});
            skArc(sketch, "E1861", {"start": v(23.39, -16.18) * mm, "mid": v(23.41, -16.15) * mm, "end": v(23.43, -16.13) * mm});
            skArc(sketch, "E1862", {"start": v(23.43, -16.13) * mm, "mid": v(23.45, -16.1) * mm, "end": v(23.46, -16.08) * mm});
            skArc(sketch, "E1863", {"start": v(23.46, -16.08) * mm, "mid": v(23.47, -16.06) * mm, "end": v(23.48, -16.03) * mm});
            skArc(sketch, "E1864", {"start": v(23.48, -16.03) * mm, "mid": v(23.45, -15.92) * mm, "end": v(23.37, -15.83) * mm});
            skArc(sketch, "E1865", {"start": v(23.37, -15.83) * mm, "mid": v(23.06, -15.63) * mm, "end": v(22.75, -15.45) * mm});
            skArc(sketch, "E1866", {"start": v(22.75, -15.45) * mm, "mid": v(22.4, -15.26) * mm, "end": v(22.06, -15.09) * mm});
            skArc(sketch, "E1867", {"start": v(22.06, -15.09) * mm, "mid": v(21.76, -14.96) * mm, "end": v(21.45, -14.85) * mm});
            skArc(sketch, "E1868", {"start": v(21.45, -14.85) * mm, "mid": v(21.3, -14.8) * mm, "end": v(21.14, -14.76) * mm});
            skArc(sketch, "E1869", {"start": v(21.14, -14.76) * mm, "mid": v(21.1, -14.75) * mm, "end": v(21.07, -14.75) * mm});
            skArc(sketch, "E1870", {"start": v(21.07, -14.75) * mm, "mid": v(21.05, -14.75) * mm, "end": v(21.03, -14.76) * mm});
            skArc(sketch, "E1871", {"start": v(21.03, -14.76) * mm, "mid": v(21, -14.79) * mm, "end": v(20.99, -14.82) * mm});
            skArc(sketch, "E1872", {"start": v(26.16, -16.84) * mm, "mid": v(26.1, -16.88) * mm, "end": v(26.03, -16.93) * mm});
            skArc(sketch, "E1873", {"start": v(26.03, -16.93) * mm, "mid": v(25.92, -17.02) * mm, "end": v(25.8, -17.12) * mm});
            skArc(sketch, "E1874", {"start": v(25.8, -17.12) * mm, "mid": v(25.67, -17.23) * mm, "end": v(25.54, -17.35) * mm});
            skArc(sketch, "E1875", {"start": v(25.54, -17.35) * mm, "mid": v(25.4, -17.47) * mm, "end": v(25.27, -17.6) * mm});
            skArc(sketch, "E1876", {"start": v(25.27, -17.6) * mm, "mid": v(24.9, -17.92) * mm, "end": v(24.5, -18.23) * mm});
            skArc(sketch, "E1877", {"start": v(24.5, -18.23) * mm, "mid": v(24.1, -18.5) * mm, "end": v(23.7, -18.73) * mm});
            skArc(sketch, "E1878", {"start": v(23.7, -18.73) * mm, "mid": v(23.27, -18.94) * mm, "end": v(22.83, -19.12) * mm});
            skArc(sketch, "E1879", {"start": v(22.83, -19.12) * mm, "mid": v(22.36, -19.27) * mm, "end": v(21.89, -19.4) * mm});
            skArc(sketch, "E1880", {"start": v(21.89, -19.4) * mm, "mid": v(21.64, -19.45) * mm, "end": v(21.4, -19.52) * mm});
            skArc(sketch, "E1881", {"start": v(21.4, -19.52) * mm, "mid": v(21.24, -19.57) * mm, "end": v(21.07, -19.63) * mm});
            skArc(sketch, "E1882", {"start": v(21.07, -19.63) * mm, "mid": v(20.97, -19.68) * mm, "end": v(20.87, -19.74) * mm});
            skArc(sketch, "E1883", {"start": v(20.87, -19.74) * mm, "mid": v(20.84, -19.78) * mm, "end": v(20.83, -19.84) * mm});
            skArc(sketch, "E1884", {"start": v(20.83, -19.84) * mm, "mid": v(20.93, -20) * mm, "end": v(21.12, -20.04) * mm});
            skArc(sketch, "E1885", {"start": v(21.12, -20.04) * mm, "mid": v(21.71, -19.93) * mm, "end": v(22.3, -19.8) * mm});
            skArc(sketch, "E1886", {"start": v(22.3, -19.8) * mm, "mid": v(22.94, -19.6) * mm, "end": v(23.57, -19.37) * mm});
            skArc(sketch, "E1887", {"start": v(23.57, -19.37) * mm, "mid": v(24.1, -19.13) * mm, "end": v(24.59, -18.84) * mm});
            skArc(sketch, "E1888", {"start": v(24.59, -18.84) * mm, "mid": v(24.95, -18.6) * mm, "end": v(25.3, -18.32) * mm});
            skArc(sketch, "E1889", {"start": v(25.3, -18.32) * mm, "mid": v(25.62, -18.05) * mm, "end": v(25.92, -17.76) * mm});
            skArc(sketch, "E1890", {"start": v(25.92, -17.76) * mm, "mid": v(26.15, -17.5) * mm, "end": v(26.37, -17.23) * mm});
            skArc(sketch, "E1891", {"start": v(26.37, -17.23) * mm, "mid": v(26.45, -17.06) * mm, "end": v(26.49, -16.86) * mm});
            skArc(sketch, "E1892", {"start": v(26.49, -16.86) * mm, "mid": v(26.48, -16.8) * mm, "end": v(26.47, -16.75) * mm});
            skArc(sketch, "E1893", {"start": v(26.47, -16.75) * mm, "mid": v(26.46, -16.72) * mm, "end": v(26.43, -16.71) * mm});
            skArc(sketch, "E1894", {"start": v(26.43, -16.71) * mm, "mid": v(26.39, -16.71) * mm, "end": v(26.35, -16.73) * mm});
            skArc(sketch, "E1895", {"start": v(26.35, -16.73) * mm, "mid": v(26.25, -16.78) * mm, "end": v(26.16, -16.84) * mm});
            skArc(sketch, "E1896", {"start": v(-1.79, -14.74) * mm, "mid": v(-1.91, -14.79) * mm, "end": v(-2, -14.88) * mm});
            skArc(sketch, "E1897", {"start": v(-2, -14.88) * mm, "mid": v(-2.01, -14.97) * mm, "end": v(-1.95, -15.02) * mm});
            skArc(sketch, "E1898", {"start": v(-1.95, -15.02) * mm, "mid": v(-1.42, -15.09) * mm, "end": v(-0.9, -15.13) * mm});
            skArc(sketch, "E1899", {"start": v(-0.9, -15.13) * mm, "mid": v(-0.1, -15.15) * mm, "end": v(0.7, -15.16) * mm});
            skArc(sketch, "E1900", {"start": v(0.7, -15.16) * mm, "mid": v(1.3, -15.17) * mm, "end": v(1.9, -15.18) * mm});
            skArc(sketch, "E1901", {"start": v(1.9, -15.18) * mm, "mid": v(2.12, -15.22) * mm, "end": v(2.33, -15.3) * mm});
            skArc(sketch, "E1902", {"start": v(2.33, -15.3) * mm, "mid": v(2.45, -15.4) * mm, "end": v(2.5, -15.56) * mm});
            skArc(sketch, "E1903", {"start": v(2.5, -15.56) * mm, "mid": v(2.5, -15.83) * mm, "end": v(2.46, -16.1) * mm});
            skArc(sketch, "E1904", {"start": v(2.46, -16.1) * mm, "mid": v(2.3, -16.65) * mm, "end": v(2.07, -17.17) * mm});
            skArc(sketch, "E1905", {"start": v(2.07, -17.17) * mm, "mid": v(1.78, -17.64) * mm, "end": v(1.42, -18.05) * mm});
            skArc(sketch, "E1906", {"start": v(1.42, -18.05) * mm, "mid": v(0.97, -18.43) * mm, "end": v(0.46, -18.74) * mm});
            skArc(sketch, "E1907", {"start": v(0.46, -18.74) * mm, "mid": v(-0.18, -19.04) * mm, "end": v(-0.85, -19.3) * mm});
            skArc(sketch, "E1908", {"start": v(-0.85, -19.3) * mm, "mid": v(-1.13, -19.39) * mm, "end": v(-1.4, -19.48) * mm});
            skArc(sketch, "E1909", {"start": v(-1.4, -19.48) * mm, "mid": v(-1.6, -19.56) * mm, "end": v(-1.78, -19.64) * mm});
            skArc(sketch, "E1910", {"start": v(-1.78, -19.64) * mm, "mid": v(-1.9, -19.7) * mm, "end": v(-2.02, -19.78) * mm});
            skArc(sketch, "E1911", {"start": v(-2.02, -19.78) * mm, "mid": v(-2.06, -19.82) * mm, "end": v(-2.06, -19.87) * mm});
            skArc(sketch, "E1912", {"start": v(-2.06, -19.87) * mm, "mid": v(-1.98, -19.97) * mm, "end": v(-1.86, -20) * mm});
            skArc(sketch, "E1913", {"start": v(-1.86, -20) * mm, "mid": v(-1.5, -19.96) * mm, "end": v(-1.14, -19.9) * mm});
            skArc(sketch, "E1914", {"start": v(-1.14, -19.9) * mm, "mid": v(-0.73, -19.8) * mm, "end": v(-0.33, -19.7) * mm});
            skArc(sketch, "E1915", {"start": v(-0.33, -19.7) * mm, "mid": v(0.04, -19.56) * mm, "end": v(0.4, -19.4) * mm});
            skArc(sketch, "E1916", {"start": v(0.4, -19.4) * mm, "mid": v(0.93, -19.1) * mm, "end": v(1.4, -18.71) * mm});
            skArc(sketch, "E1917", {"start": v(1.4, -18.71) * mm, "mid": v(1.86, -18.22) * mm, "end": v(2.26, -17.68) * mm});
            skArc(sketch, "E1918", {"start": v(2.26, -17.68) * mm, "mid": v(2.58, -17.1) * mm, "end": v(2.84, -16.5) * mm});
            skArc(sketch, "E1919", {"start": v(2.84, -16.5) * mm, "mid": v(2.99, -15.92) * mm, "end": v(3.04, -15.33) * mm});
            skArc(sketch, "E1920", {"start": v(3.04, -15.33) * mm, "mid": v(3.03, -15.22) * mm, "end": v(3.03, -15.12) * mm});
            skArc(sketch, "E1921", {"start": v(3.03, -15.12) * mm, "mid": v(3.02, -15.05) * mm, "end": v(3, -14.97) * mm});
            skArc(sketch, "E1922", {"start": v(3, -14.97) * mm, "mid": v(3, -14.92) * mm, "end": v(2.97, -14.87) * mm});
            skArc(sketch, "E1923", {"start": v(2.97, -14.87) * mm, "mid": v(2.95, -14.83) * mm, "end": v(2.92, -14.8) * mm});
            skArc(sketch, "E1924", {"start": v(2.92, -14.8) * mm, "mid": v(2.86, -14.77) * mm, "end": v(2.8, -14.75) * mm});
            skArc(sketch, "E1925", {"start": v(2.8, -14.75) * mm, "mid": v(2.6, -14.73) * mm, "end": v(2.4, -14.72) * mm});
            skArc(sketch, "E1926", {"start": v(2.4, -14.72) * mm, "mid": v(2.1, -14.71) * mm, "end": v(1.8, -14.7) * mm});
            skArc(sketch, "E1927", {"start": v(1.8, -14.7) * mm, "mid": v(1.27, -14.7) * mm, "end": v(0.73, -14.7) * mm});
            skArc(sketch, "E1928", {"start": v(0.73, -14.7) * mm, "mid": v(0.32, -14.7) * mm, "end": v(-0.1, -14.7) * mm});
            skArc(sketch, "E1929", {"start": v(-0.1, -14.7) * mm, "mid": v(-0.48, -14.7) * mm, "end": v(-0.86, -14.7) * mm});
            skArc(sketch, "E1930", {"start": v(-0.86, -14.7) * mm, "mid": v(-1.18, -14.71) * mm, "end": v(-1.5, -14.72) * mm});
            skArc(sketch, "E1931", {"start": v(-1.5, -14.72) * mm, "mid": v(-1.65, -14.73) * mm, "end": v(-1.79, -14.74) * mm});
            skArc(sketch, "E1932", {"start": v(-13.96, -15.07) * mm, "mid": v(-14.07, -15.32) * mm, "end": v(-14.12, -15.58) * mm});
            skArc(sketch, "E1933", {"start": v(-14.12, -15.58) * mm, "mid": v(-14.16, -16.02) * mm, "end": v(-14.18, -16.46) * mm});
            skArc(sketch, "E1934", {"start": v(-14.18, -16.46) * mm, "mid": v(-14.19, -16.92) * mm, "end": v(-14.17, -17.39) * mm});
            skArc(sketch, "E1935", {"start": v(-14.17, -17.39) * mm, "mid": v(-14.12, -17.76) * mm, "end": v(-14.05, -18.12) * mm});
            skArc(sketch, "E1936", {"start": v(-14.05, -18.12) * mm, "mid": v(-13.95, -18.45) * mm, "end": v(-13.83, -18.78) * mm});
            skArc(sketch, "E1937", {"start": v(-13.83, -18.78) * mm, "mid": v(-13.7, -19.05) * mm, "end": v(-13.54, -19.3) * mm});
            skArc(sketch, "E1938", {"start": v(-13.54, -19.3) * mm, "mid": v(-13.4, -19.5) * mm, "end": v(-13.22, -19.67) * mm});
            skArc(sketch, "E1939", {"start": v(-13.22, -19.67) * mm, "mid": v(-13.07, -19.75) * mm, "end": v(-12.9, -19.78) * mm});
            skArc(sketch, "E1940", {"start": v(-12.9, -19.78) * mm, "mid": v(-12.78, -19.76) * mm, "end": v(-12.66, -19.7) * mm});
            skArc(sketch, "E1941", {"start": v(-12.66, -19.7) * mm, "mid": v(-12.5, -19.56) * mm, "end": v(-12.33, -19.4) * mm});
            skArc(sketch, "E1942", {"start": v(-12.33, -19.4) * mm, "mid": v(-12.16, -19.2) * mm, "end": v(-12, -19) * mm});
            skArc(sketch, "E1943", {"start": v(-12, -19) * mm, "mid": v(-11.86, -18.8) * mm, "end": v(-11.74, -18.58) * mm});
            skArc(sketch, "E1944", {"start": v(-11.74, -18.58) * mm, "mid": v(-11.67, -18.43) * mm, "end": v(-11.6, -18.26) * mm});
            skArc(sketch, "E1945", {"start": v(-11.6, -18.26) * mm, "mid": v(-11.56, -18.16) * mm, "end": v(-11.54, -18.06) * mm});
            skArc(sketch, "E1946", {"start": v(-11.54, -18.06) * mm, "mid": v(-11.54, -17.99) * mm, "end": v(-11.55, -17.92) * mm});
            skArc(sketch, "E1947", {"start": v(-11.55, -17.92) * mm, "mid": v(-11.58, -17.88) * mm, "end": v(-11.63, -17.85) * mm});
            skArc(sketch, "E1948", {"start": v(-11.63, -17.85) * mm, "mid": v(-11.7, -17.84) * mm, "end": v(-11.76, -17.85) * mm});
            skArc(sketch, "E1949", {"start": v(-11.76, -17.85) * mm, "mid": v(-11.85, -17.91) * mm, "end": v(-11.92, -17.98) * mm});
            skArc(sketch, "E1950", {"start": v(-11.92, -17.98) * mm, "mid": v(-12.03, -18.1) * mm, "end": v(-12.12, -18.22) * mm});
            skArc(sketch, "E1951", {"start": v(-12.12, -18.22) * mm, "mid": v(-12.27, -18.43) * mm, "end": v(-12.41, -18.64) * mm});
            skArc(sketch, "E1952", {"start": v(-12.41, -18.64) * mm, "mid": v(-12.49, -18.76) * mm, "end": v(-12.56, -18.87) * mm});
            skArc(sketch, "E1953", {"start": v(-12.56, -18.87) * mm, "mid": v(-12.63, -18.96) * mm, "end": v(-12.7, -19.05) * mm});
            skArc(sketch, "E1954", {"start": v(-12.7, -19.05) * mm, "mid": v(-12.77, -19.12) * mm, "end": v(-12.84, -19.2) * mm});
            skArc(sketch, "E1955", {"start": v(-12.84, -19.2) * mm, "mid": v(-12.86, -19.21) * mm, "end": v(-12.9, -19.22) * mm});
            skArc(sketch, "E1956", {"start": v(-12.9, -19.22) * mm, "mid": v(-12.97, -19.2) * mm, "end": v(-13.04, -19.17) * mm});
            skArc(sketch, "E1957", {"start": v(-13.04, -19.17) * mm, "mid": v(-13.13, -19.09) * mm, "end": v(-13.22, -19) * mm});
            skArc(sketch, "E1958", {"start": v(-13.22, -19) * mm, "mid": v(-13.3, -18.9) * mm, "end": v(-13.38, -18.78) * mm});
            skArc(sketch, "E1959", {"start": v(-13.38, -18.78) * mm, "mid": v(-13.44, -18.67) * mm, "end": v(-13.48, -18.55) * mm});
            skArc(sketch, "E1960", {"start": v(-13.48, -18.55) * mm, "mid": v(-13.5, -18.46) * mm, "end": v(-13.52, -18.37) * mm});
            skArc(sketch, "E1961", {"start": v(-13.52, -18.37) * mm, "mid": v(-13.54, -18.14) * mm, "end": v(-13.56, -17.91) * mm});
            skArc(sketch, "E1962", {"start": v(-13.56, -17.91) * mm, "mid": v(-13.58, -17.64) * mm, "end": v(-13.6, -17.37) * mm});
            skArc(sketch, "E1963", {"start": v(-13.6, -17.37) * mm, "mid": v(-13.61, -17.07) * mm, "end": v(-13.63, -16.77) * mm});
            skArc(sketch, "E1964", {"start": v(-13.63, -16.77) * mm, "mid": v(-13.64, -16.48) * mm, "end": v(-13.65, -16.18) * mm});
            skArc(sketch, "E1965", {"start": v(-13.65, -16.18) * mm, "mid": v(-13.67, -15.92) * mm, "end": v(-13.68, -15.66) * mm});
            skArc(sketch, "E1966", {"start": v(-13.68, -15.66) * mm, "mid": v(-13.7, -15.44) * mm, "end": v(-13.71, -15.22) * mm});
            skArc(sketch, "E1967", {"start": v(-13.71, -15.22) * mm, "mid": v(-13.72, -15.16) * mm, "end": v(-13.73, -15.1) * mm});
            skArc(sketch, "E1968", {"start": v(-13.73, -15.1) * mm, "mid": v(-13.75, -15.05) * mm, "end": v(-13.78, -15) * mm});
            skArc(sketch, "E1969", {"start": v(-13.78, -15) * mm, "mid": v(-13.8, -14.97) * mm, "end": v(-13.84, -14.96) * mm});
            skArc(sketch, "E1970", {"start": v(-13.84, -14.96) * mm, "mid": v(-13.87, -14.96) * mm, "end": v(-13.9, -14.98) * mm});
            skArc(sketch, "E1971", {"start": v(-13.9, -14.98) * mm, "mid": v(-13.93, -15.02) * mm, "end": v(-13.96, -15.07) * mm});
            skArc(sketch, "E1972", {"start": v(-9.91, -15.11) * mm, "mid": v(-9.91, -15.17) * mm, "end": v(-9.9, -15.22) * mm});
            skArc(sketch, "E1973", {"start": v(-9.9, -15.22) * mm, "mid": v(-9.86, -15.34) * mm, "end": v(-9.82, -15.45) * mm});
            skArc(sketch, "E1974", {"start": v(-9.82, -15.45) * mm, "mid": v(-9.77, -15.59) * mm, "end": v(-9.72, -15.72) * mm});
            skArc(sketch, "E1975", {"start": v(-9.72, -15.72) * mm, "mid": v(-9.66, -15.86) * mm, "end": v(-9.6, -16) * mm});
            skArc(sketch, "E1976", {"start": v(-9.6, -16) * mm, "mid": v(-9.53, -16.16) * mm, "end": v(-9.47, -16.32) * mm});
            skArc(sketch, "E1977", {"start": v(-9.47, -16.32) * mm, "mid": v(-9.4, -16.5) * mm, "end": v(-9.32, -16.7) * mm});
            skArc(sketch, "E1978", {"start": v(-9.32, -16.7) * mm, "mid": v(-9.26, -16.88) * mm, "end": v(-9.2, -17.07) * mm});
            skArc(sketch, "E1979", {"start": v(-9.2, -17.07) * mm, "mid": v(-9.15, -17.23) * mm, "end": v(-9.1, -17.38) * mm});
            skArc(sketch, "E1980", {"start": v(-9.1, -17.38) * mm, "mid": v(-9, -17.8) * mm, "end": v(-8.88, -18.2) * mm});
            skArc(sketch, "E1981", {"start": v(-8.88, -18.2) * mm, "mid": v(-8.82, -18.4) * mm, "end": v(-8.76, -18.58) * mm});
            skArc(sketch, "E1982", {"start": v(-8.76, -18.58) * mm, "mid": v(-8.71, -18.69) * mm, "end": v(-8.66, -18.8) * mm});
            skArc(sketch, "E1983", {"start": v(-8.66, -18.8) * mm, "mid": v(-8.63, -18.83) * mm, "end": v(-8.57, -18.86) * mm});
            skArc(sketch, "E1984", {"start": v(-8.57, -18.86) * mm, "mid": v(-8.46, -18.83) * mm, "end": v(-8.41, -18.74) * mm});
            skArc(sketch, "E1985", {"start": v(-8.41, -18.74) * mm, "mid": v(-8.4, -18.48) * mm, "end": v(-8.42, -18.22) * mm});
            skArc(sketch, "E1986", {"start": v(-8.42, -18.22) * mm, "mid": v(-8.47, -17.85) * mm, "end": v(-8.55, -17.49) * mm});
            skArc(sketch, "E1987", {"start": v(-8.55, -17.49) * mm, "mid": v(-8.67, -17.07) * mm, "end": v(-8.8, -16.66) * mm});
            skArc(sketch, "E1988", {"start": v(-8.8, -16.66) * mm, "mid": v(-8.9, -16.43) * mm, "end": v(-9, -16.2) * mm});
            skArc(sketch, "E1989", {"start": v(-9, -16.2) * mm, "mid": v(-9.11, -15.98) * mm, "end": v(-9.23, -15.75) * mm});
            skArc(sketch, "E1990", {"start": v(-9.23, -15.75) * mm, "mid": v(-9.36, -15.56) * mm, "end": v(-9.49, -15.37) * mm});
            skArc(sketch, "E1991", {"start": v(-9.49, -15.37) * mm, "mid": v(-9.6, -15.22) * mm, "end": v(-9.73, -15.1) * mm});
            skLineSegment(sketch, "E1992", {"start": v(-9.73, -15.1) * mm, "end": v(-9.91, -14.93) * mm});
            skLineSegment(sketch, "E1993", {"start": v(-9.91, -14.93) * mm, "end": v(-9.91, -15.11) * mm});
            skArc(sketch, "E1994", {"start": v(-35.24, 11.65) * mm, "mid": v(-35.38, 11.23) * mm, "end": v(-35.56, 10.83) * mm});
            skArc(sketch, "E1995", {"start": v(-35.56, 10.83) * mm, "mid": v(-35.76, 10.5) * mm, "end": v(-36.02, 10.22) * mm});
            skArc(sketch, "E1996", {"start": v(-36.02, 10.22) * mm, "mid": v(-36.3, 10) * mm, "end": v(-36.62, 9.82) * mm});
            skArc(sketch, "E1997", {"start": v(-36.62, 9.82) * mm, "mid": v(-36.98, 9.7) * mm, "end": v(-37.36, 9.63) * mm});
            skArc(sketch, "E1998", {"start": v(-37.36, 9.63) * mm, "mid": v(-37.46, 9.62) * mm, "end": v(-37.55, 9.6) * mm});
            skArc(sketch, "E1999", {"start": v(-37.55, 9.6) * mm, "mid": v(-37.64, 9.59) * mm, "end": v(-37.72, 9.57) * mm});
            skArc(sketch, "E2000", {"start": v(-37.72, 9.57) * mm, "mid": v(-37.8, 9.56) * mm, "end": v(-37.86, 9.54) * mm});
            skArc(sketch, "E2001", {"start": v(-37.86, 9.54) * mm, "mid": v(-37.89, 9.53) * mm, "end": v(-37.91, 9.5) * mm});
            skArc(sketch, "E2002", {"start": v(-37.91, 9.5) * mm, "mid": v(-37.93, 9.49) * mm, "end": v(-37.94, 9.46) * mm});
            skArc(sketch, "E2003", {"start": v(-37.94, 9.46) * mm, "mid": v(-37.94, 9.4) * mm, "end": v(-37.94, 9.33) * mm});
            skArc(sketch, "E2004", {"start": v(-37.94, 9.33) * mm, "mid": v(-37.94, 9.25) * mm, "end": v(-37.93, 9.16) * mm});
            skArc(sketch, "E2005", {"start": v(-37.93, 9.16) * mm, "mid": v(-37.92, 9.06) * mm, "end": v(-37.91, 8.95) * mm});
            skArc(sketch, "E2006", {"start": v(-37.91, 8.95) * mm, "mid": v(-37.9, 8.8) * mm, "end": v(-37.88, 8.63) * mm});
            skArc(sketch, "E2007", {"start": v(-37.88, 8.63) * mm, "mid": v(-37.87, 8.16) * mm, "end": v(-37.85, 7.69) * mm});
            skArc(sketch, "E2008", {"start": v(-37.85, 7.69) * mm, "mid": v(-37.84, 7.13) * mm, "end": v(-37.82, 6.57) * mm});
            skArc(sketch, "E2009", {"start": v(-37.82, 6.57) * mm, "mid": v(-37.81, 5.95) * mm, "end": v(-37.8, 5.33) * mm});
            skLineSegment(sketch, "E2010", {"start": v(-37.8, 5.33) * mm, "end": v(-37.75, 2.2) * mm});
            skLineSegment(sketch, "E2011", {"start": v(-37.75, 2.2) * mm, "end": v(-37.36, 2.13) * mm});
            skArc(sketch, "E2012", {"start": v(-37.36, 2.13) * mm, "mid": v(-37, 2.06) * mm, "end": v(-36.64, 1.97) * mm});
            skArc(sketch, "E2013", {"start": v(-36.64, 1.97) * mm, "mid": v(-36.41, 1.9) * mm, "end": v(-36.19, 1.82) * mm});
            skArc(sketch, "E2014", {"start": v(-36.19, 1.82) * mm, "mid": v(-36.02, 1.73) * mm, "end": v(-35.86, 1.63) * mm});
            skArc(sketch, "E2015", {"start": v(-35.86, 1.63) * mm, "mid": v(-35.7, 1.5) * mm, "end": v(-35.54, 1.34) * mm});
            skArc(sketch, "E2016", {"start": v(-35.54, 1.34) * mm, "mid": v(-35.48, 1.27) * mm, "end": v(-35.42, 1.2) * mm});
            skArc(sketch, "E2017", {"start": v(-35.42, 1.2) * mm, "mid": v(-35.35, 1.13) * mm, "end": v(-35.28, 1.05) * mm});
            skArc(sketch, "E2018", {"start": v(-35.28, 1.05) * mm, "mid": v(-35.2, 0.97) * mm, "end": v(-35.14, 0.9) * mm});
            skArc(sketch, "E2019", {"start": v(-35.14, 0.9) * mm, "mid": v(-35.08, 0.83) * mm, "end": v(-35.02, 0.76) * mm});
            skLineSegment(sketch, "E2020", {"start": v(-35.02, 0.76) * mm, "end": v(-34.76, 0.48) * mm});
            skLineSegment(sketch, "E2021", {"start": v(-34.76, 0.48) * mm, "end": v(-34.62, 0.66) * mm});
            skArc(sketch, "E2022", {"start": v(-34.62, 0.66) * mm, "mid": v(-34.46, 0.86) * mm, "end": v(-34.33, 1.07) * mm});
            skArc(sketch, "E2023", {"start": v(-34.33, 1.07) * mm, "mid": v(-33.66, 2.2) * mm, "end": v(-33, 3.35) * mm});
            skArc(sketch, "E2024", {"start": v(-33, 3.35) * mm, "mid": v(-32.3, 4.55) * mm, "end": v(-31.6, 5.75) * mm});
            skArc(sketch, "E2025", {"start": v(-31.6, 5.75) * mm, "mid": v(-31.56, 5.84) * mm, "end": v(-31.54, 5.93) * mm});
            skArc(sketch, "E2026", {"start": v(-31.54, 5.93) * mm, "mid": v(-31.55, 5.96) * mm, "end": v(-31.56, 6) * mm});
            skArc(sketch, "E2027", {"start": v(-31.56, 6) * mm, "mid": v(-32.42, 7.51) * mm, "end": v(-33.27, 9.04) * mm});
            skArc(sketch, "E2028", {"start": v(-33.27, 9.04) * mm, "mid": v(-34.12, 10.55) * mm, "end": v(-34.96, 12.06) * mm});
            skArc(sketch, "E2029", {"start": v(-34.96, 12.06) * mm, "mid": v(-35, 12.11) * mm, "end": v(-35.04, 12.16) * mm});
            skArc(sketch, "E2030", {"start": v(-35.04, 12.16) * mm, "mid": v(-35.05, 12.16) * mm, "end": v(-35.07, 12.15) * mm});
            skArc(sketch, "E2031", {"start": v(-35.07, 12.15) * mm, "mid": v(-35.1, 12.1) * mm, "end": v(-35.12, 12.03) * mm});
            skArc(sketch, "E2032", {"start": v(-35.12, 12.03) * mm, "mid": v(-35.15, 11.95) * mm, "end": v(-35.18, 11.86) * mm});
            skArc(sketch, "E2033", {"start": v(-35.18, 11.86) * mm, "mid": v(-35.21, 11.75) * mm, "end": v(-35.24, 11.65) * mm});
            skSolve(sketch);
        }
        {
            var Q0;
            Q0=qCreatedBy(makeId("Top.planeOp"),FACE);
            var sketch = newSketch(context, id + "F1", { "sketchPlane" : qUnion([Q0])});
            skLineSegment(sketch, "E2034.bottom", {"start": v(85, 25) * mm, "end": v(-85, 25) * mm});
            skLineSegment(sketch, "E2034.top", {"start": v(85, -25) * mm, "end": v(-85, -25) * mm});
            skLineSegment(sketch, "E2034.left", {"start": v(85, 25) * mm, "end": v(85, -25) * mm});
            skLineSegment(sketch, "E2034.right", {"start": v(-85, 25) * mm, "end": v(-85, -25) * mm});
            skPoint(sketch, "E2034.middle", {"position": v(0, 0) * mm});
            skSolve(sketch);
        }
        {
            var Q0;
            Q0 = qSketchRegion(id + "F1", true);
            extrude(context, id + "F2", {"entities" : qUnion([Q0]), "oppositeDirection" : true, "depth" : 0.5 * mm, "offsetDistance" : 25 * mm});
        }
        {
            var Q0;
            Q0 = qSketchRegion(id + "F0", true);
            var Q1;
            Q1=makeQuery(id+"F0.imprint","IMPRINT",FACE,{"disambiguationData":[TD([[makeQuery(id+"F0.imprint","IMPRINT",EDGE,{"derivedFrom":sQuery(id+"F0.wireOp",EDGE,"E1210")}),-1.0]])]});
            var Q2;
            Q2=makeQuery(id+"F0.imprint","IMPRINT",FACE,{"disambiguationData":[TD([[makeQuery(id+"F0.imprint","IMPRINT",EDGE,{"derivedFrom":sQuery(id+"F0.wireOp",EDGE,"E1304")}),-1.0]])]});
            var Q3;
            Q3=makeQuery(id+"F0.imprint","IMPRINT",FACE,{"disambiguationData":[TD([[makeQuery(id+"F0.imprint","IMPRINT",EDGE,{"derivedFrom":sQuery(id+"F0.wireOp",EDGE,"E1704")}),-1.0]])]});
            extrude(context, id + "F3", {"entities" : qUnion([Q0, Q1, Q2, Q3]), "operationType" : NewBodyOperationType.ADD, "depth" : 0.5 * mm, "offsetDistance" : 25 * mm});
        }
        {
            var Q0;
            {var subQ0=sQuery(id+"F1.wireOp",EDGE,"E2034.bottom");var subQ1=sQuery(id+"F1.wireOp",EDGE,"E2034.top");var subQ2=sQuery(id+"F1.wireOp",EDGE,"E2034.left");var subQ3=sQuery(id+"F1.wireOp",EDGE,"E2034.right");Q0=makeQuery(id+"F3.boolean.opBoolean","SPLIT",FACE,{"disambiguationData":[TD([makeQuery(id+"F2.opExtrude","SWEPT_FACE",FACE,{"disambiguationData":[OSD([subQ0])]})])],"derivedFrom":makeQuery(id+"F2.opExtrude","CAP_FACE",FACE,{"disambiguationData":[OSD([subQ0,subQ1,subQ2,subQ3])],"isStart":true})});}
            extrude(context, id + "F4", {"entities" : qUnion([Q0]), "operationType" : NewBodyOperationType.ADD, "depth" : 1.5 * mm, "offsetDistance" : 25 * mm});
        }
        {
            var Q0;
            Q0=makeQuery(id+"F2.opExtrude","CAP_FACE",FACE,{"disambiguationData":[OSD([sQuery(id+"F1.wireOp",EDGE,"E2034.bottom"),sQuery(id+"F1.wireOp",EDGE,"E2034.top"),sQuery(id+"F1.wireOp",EDGE,"E2034.left"),sQuery(id+"F1.wireOp",EDGE,"E2034.right")])],"isStart":false});
            extrude(context, id + "F5", {"entities" : qUnion([Q0]), "operationType" : NewBodyOperationType.REMOVE, "oppositeDirection" : true, "depth" : 0.3 * mm, "offsetDistance" : 25 * mm});
        }
        {
            var Q0;
            Q0=makeQuery(id+"F4.opExtrude","CAP_FACE",FACE,{"disambiguationData":[OSD([sQuery(id+"F1.wireOp",EDGE,"E2034.bottom"),sQuery(id+"F1.wireOp",EDGE,"E2034.top"),sQuery(id+"F1.wireOp",EDGE,"E2034.left"),sQuery(id+"F1.wireOp",EDGE,"E2034.right")])],"isStart":false});
            extrude(context, id + "F6", {"entities" : qUnion([Q0]), "operationType" : NewBodyOperationType.REMOVE, "oppositeDirection" : true, "depth" : 0.2 * mm, "offsetDistance" : 25 * mm});
        }
    });
